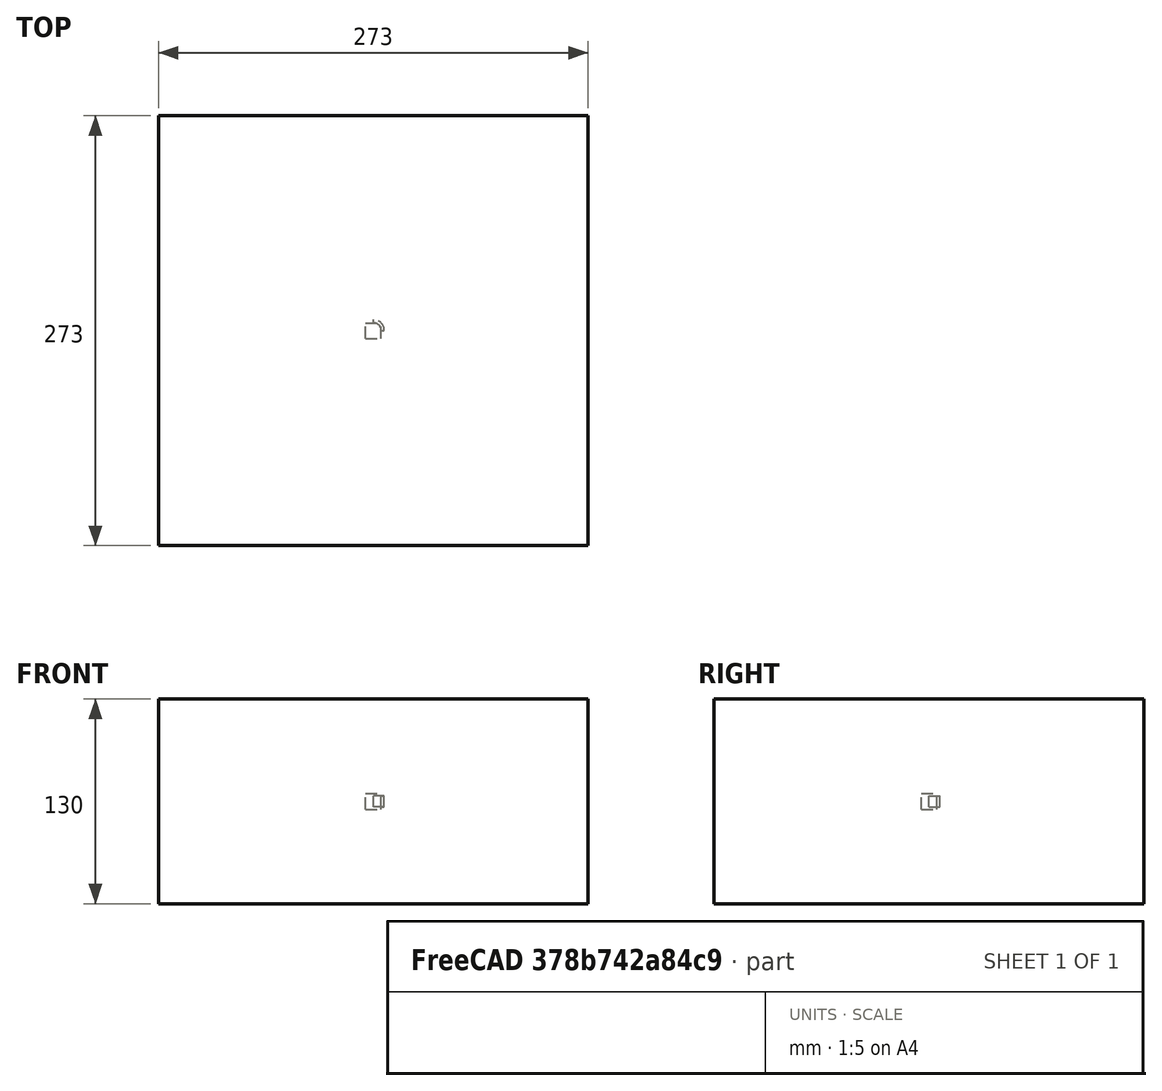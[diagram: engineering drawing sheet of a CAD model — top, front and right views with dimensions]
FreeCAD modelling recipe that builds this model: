
FCSTD DOCUMENT  (FreeCAD 0.20RUnknown)
Label: polarArray-5
License: All rights reserved
LicenseURL: http://en.wikipedia.org/wiki/All_rights_reserved
objects: App::DocumentObjectGroupPython×1251, Part::FeaturePython×4, App::Part×4
note: 3 computed .brp shape members not serialized (recipe doc carries the construction recipe); baked Part::Feature solids carry a one-line shape summary decoded from their .brp

FEATURE [App::DocumentObjectGroupPython] HALFPI  # scripted group (container) (typed FeaturePython)
  name = HALFPI
  value = pi/2.
FEATURE [App::DocumentObjectGroupPython] PI  # scripted group (container) (typed FeaturePython)
  name = PI
  value = 1.*pi
FEATURE [App::DocumentObjectGroupPython] TWOPI  # scripted group (container) (typed FeaturePython)
  name = TWOPI
  value = 2.*pi
FEATURE [App::DocumentObjectGroupPython] Constants  # scripted group (container) (typed FeaturePython)
  Group = -> [HALFPI,PI,TWOPI]
FEATURE [App::DocumentObjectGroupPython] Variables  # scripted group (container) (typed FeaturePython)
FEATURE [App::DocumentObjectGroupPython] Quantities  # scripted group (container) (typed FeaturePython)
FEATURE [App::DocumentObjectGroupPython] Isotopes  # scripted group (container) (typed FeaturePython)
FEATURE [App::DocumentObjectGroupPython] Elements  # scripted group (container) (typed FeaturePython)
FEATURE [App::DocumentObjectGroupPython] Matrix  # scripted group (container) (typed FeaturePython)
FEATURE [App::DocumentObjectGroupPython] Surfaces  # scripted group (container) (typed FeaturePython)
FEATURE [App::DocumentObjectGroupPython] Opticals  # scripted group (container) (typed FeaturePython)
  Group = -> [Matrix,Surfaces]
FEATURE [App::DocumentObjectGroupPython] G4Isotopes  # scripted group (container) (typed FeaturePython)
FEATURE [App::DocumentObjectGroupPython] H_element  # scripted group (container) (typed FeaturePython)
  Z = 1
  atom_value = 1.008
  formula = H
  name = H_element
FEATURE [App::DocumentObjectGroupPython] He_element  # scripted group (container) (typed FeaturePython)
  Z = 2
  atom_value = 4.0026
  formula = He
  name = He_element
FEATURE [App::DocumentObjectGroupPython] Li_element  # scripted group (container) (typed FeaturePython)
  Z = 3
  atom_value = 6.94
  formula = Li
  name = Li_element
FEATURE [App::DocumentObjectGroupPython] Be_element  # scripted group (container) (typed FeaturePython)
  Z = 4
  atom_value = 9.01218
  formula = Be
  name = Be_element
FEATURE [App::DocumentObjectGroupPython] B_element  # scripted group (container) (typed FeaturePython)
  Z = 5
  atom_value = 10.81
  formula = B
  name = B_element
FEATURE [App::DocumentObjectGroupPython] C_element  # scripted group (container) (typed FeaturePython)
  Z = 6
  atom_value = 12.011
  formula = C
  name = C_element
FEATURE [App::DocumentObjectGroupPython] N_element  # scripted group (container) (typed FeaturePython)
  Z = 7
  atom_value = 14.007
  formula = N
  name = N_element
FEATURE [App::DocumentObjectGroupPython] O_element  # scripted group (container) (typed FeaturePython)
  Z = 8
  atom_value = 15.999
  formula = O
  name = O_element
FEATURE [App::DocumentObjectGroupPython] F_element  # scripted group (container) (typed FeaturePython)
  Z = 9
  atom_value = 18.9984
  formula = F
  name = F_element
FEATURE [App::DocumentObjectGroupPython] Ne_element  # scripted group (container) (typed FeaturePython)
  Z = 10
  atom_value = 20.1797
  formula = Ne
  name = Ne_element
FEATURE [App::DocumentObjectGroupPython] Na_element  # scripted group (container) (typed FeaturePython)
  Z = 11
  atom_value = 22.9898
  formula = Na
  name = Na_element
FEATURE [App::DocumentObjectGroupPython] Mg_element  # scripted group (container) (typed FeaturePython)
  Z = 12
  atom_value = 24.305
  formula = Mg
  name = Mg_element
FEATURE [App::DocumentObjectGroupPython] Al_element  # scripted group (container) (typed FeaturePython)
  Z = 13
  atom_value = 26.9815
  formula = Al
  name = Al_element
FEATURE [App::DocumentObjectGroupPython] Si_element  # scripted group (container) (typed FeaturePython)
  Z = 14
  atom_value = 28.085
  formula = Si
  name = Si_element
FEATURE [App::DocumentObjectGroupPython] P_element  # scripted group (container) (typed FeaturePython)
  Z = 15
  atom_value = 30.9738
  formula = P
  name = P_element
FEATURE [App::DocumentObjectGroupPython] S_element  # scripted group (container) (typed FeaturePython)
  Z = 16
  atom_value = 32.06
  formula = S
  name = S_element
FEATURE [App::DocumentObjectGroupPython] Cl_element  # scripted group (container) (typed FeaturePython)
  Z = 17
  atom_value = 35.45
  formula = Cl
  name = Cl_element
FEATURE [App::DocumentObjectGroupPython] Ar_element  # scripted group (container) (typed FeaturePython)
  Z = 18
  atom_value = 39.95
  formula = Ar
  name = Ar_element
FEATURE [App::DocumentObjectGroupPython] K_element  # scripted group (container) (typed FeaturePython)
  Z = 19
  atom_value = 39.0983
  formula = K
  name = K_element
FEATURE [App::DocumentObjectGroupPython] Ca_element  # scripted group (container) (typed FeaturePython)
  Z = 20
  atom_value = 40.078
  formula = Ca
  name = Ca_element
FEATURE [App::DocumentObjectGroupPython] Sc_element  # scripted group (container) (typed FeaturePython)
  Z = 21
  atom_value = 44.9559
  formula = Sc
  name = Sc_element
FEATURE [App::DocumentObjectGroupPython] Ti_element  # scripted group (container) (typed FeaturePython)
  Z = 22
  atom_value = 47.867
  formula = Ti
  name = Ti_element
FEATURE [App::DocumentObjectGroupPython] V_element  # scripted group (container) (typed FeaturePython)
  Z = 23
  atom_value = 50.9415
  formula = V
  name = V_element
FEATURE [App::DocumentObjectGroupPython] Cr_element  # scripted group (container) (typed FeaturePython)
  Z = 24
  atom_value = 51.9961
  formula = Cr
  name = Cr_element
FEATURE [App::DocumentObjectGroupPython] Mn_element  # scripted group (container) (typed FeaturePython)
  Z = 25
  atom_value = 54.938
  formula = Mn
  name = Mn_element
FEATURE [App::DocumentObjectGroupPython] Fe_element  # scripted group (container) (typed FeaturePython)
  Z = 26
  atom_value = 55.845
  formula = Fe
  name = Fe_element
FEATURE [App::DocumentObjectGroupPython] Co_element  # scripted group (container) (typed FeaturePython)
  Z = 27
  atom_value = 58.9332
  formula = Co
  name = Co_element
FEATURE [App::DocumentObjectGroupPython] Ni_element  # scripted group (container) (typed FeaturePython)
  Z = 28
  atom_value = 58.6934
  formula = Ni
  name = Ni_element
FEATURE [App::DocumentObjectGroupPython] Cu_element  # scripted group (container) (typed FeaturePython)
  Z = 29
  atom_value = 63.546
  formula = Cu
  name = Cu_element
FEATURE [App::DocumentObjectGroupPython] Zn_element  # scripted group (container) (typed FeaturePython)
  Z = 30
  atom_value = 65.38
  formula = Zn
  name = Zn_element
FEATURE [App::DocumentObjectGroupPython] Ga_element  # scripted group (container) (typed FeaturePython)
  Z = 31
  atom_value = 69.723
  formula = Ga
  name = Ga_element
FEATURE [App::DocumentObjectGroupPython] Ge_element  # scripted group (container) (typed FeaturePython)
  Z = 32
  atom_value = 72.63
  formula = Ge
  name = Ge_element
FEATURE [App::DocumentObjectGroupPython] As_element  # scripted group (container) (typed FeaturePython)
  Z = 33
  atom_value = 74.9216
  formula = As
  name = As_element
FEATURE [App::DocumentObjectGroupPython] Se_element  # scripted group (container) (typed FeaturePython)
  Z = 34
  atom_value = 78.971
  formula = Se
  name = Se_element
FEATURE [App::DocumentObjectGroupPython] Br_element  # scripted group (container) (typed FeaturePython)
  Z = 35
  atom_value = 79.904
  formula = Br
  name = Br_element
FEATURE [App::DocumentObjectGroupPython] Kr_element  # scripted group (container) (typed FeaturePython)
  Z = 36
  atom_value = 83.798
  formula = Kr
  name = Kr_element
FEATURE [App::DocumentObjectGroupPython] Rb_element  # scripted group (container) (typed FeaturePython)
  Z = 37
  atom_value = 85.4678
  formula = Rb
  name = Rb_element
FEATURE [App::DocumentObjectGroupPython] Sr_element  # scripted group (container) (typed FeaturePython)
  Z = 38
  atom_value = 87.62
  formula = Sr
  name = Sr_element
FEATURE [App::DocumentObjectGroupPython] Y_element  # scripted group (container) (typed FeaturePython)
  Z = 39
  atom_value = 88.9058
  formula = Y
  name = Y_element
FEATURE [App::DocumentObjectGroupPython] Zr_element  # scripted group (container) (typed FeaturePython)
  Z = 40
  atom_value = 91.224
  formula = Zr
  name = Zr_element
FEATURE [App::DocumentObjectGroupPython] Nb_element  # scripted group (container) (typed FeaturePython)
  Z = 41
  atom_value = 92.9064
  formula = Nb
  name = Nb_element
FEATURE [App::DocumentObjectGroupPython] Mo_element  # scripted group (container) (typed FeaturePython)
  Z = 42
  atom_value = 95.95
  formula = Mo
  name = Mo_element
FEATURE [App::DocumentObjectGroupPython] Tc_element  # scripted group (container) (typed FeaturePython)
  Z = 43
  atom_value = 97
  formula = Tc
  name = Tc_element
FEATURE [App::DocumentObjectGroupPython] Ru_element  # scripted group (container) (typed FeaturePython)
  Z = 44
  atom_value = 101.07
  formula = Ru
  name = Ru_element
FEATURE [App::DocumentObjectGroupPython] Rh_element  # scripted group (container) (typed FeaturePython)
  Z = 45
  atom_value = 102.905
  formula = Rh
  name = Rh_element
FEATURE [App::DocumentObjectGroupPython] Pd_element  # scripted group (container) (typed FeaturePython)
  Z = 46
  atom_value = 106.42
  formula = Pd
  name = Pd_element
FEATURE [App::DocumentObjectGroupPython] Ag_element  # scripted group (container) (typed FeaturePython)
  Z = 47
  atom_value = 107.868
  formula = Ag
  name = Ag_element
FEATURE [App::DocumentObjectGroupPython] Cd_element  # scripted group (container) (typed FeaturePython)
  Z = 48
  atom_value = 112.414
  formula = Cd
  name = Cd_element
FEATURE [App::DocumentObjectGroupPython] In_element  # scripted group (container) (typed FeaturePython)
  Z = 49
  atom_value = 114.818
  formula = In
  name = In_element
FEATURE [App::DocumentObjectGroupPython] Sn_element  # scripted group (container) (typed FeaturePython)
  Z = 50
  atom_value = 118.71
  formula = Sn
  name = Sn_element
FEATURE [App::DocumentObjectGroupPython] Sb_element  # scripted group (container) (typed FeaturePython)
  Z = 51
  atom_value = 121.76
  formula = Sb
  name = Sb_element
FEATURE [App::DocumentObjectGroupPython] Te_element  # scripted group (container) (typed FeaturePython)
  Z = 52
  atom_value = 127.6
  formula = Te
  name = Te_element
FEATURE [App::DocumentObjectGroupPython] I_element  # scripted group (container) (typed FeaturePython)
  Z = 53
  atom_value = 126.904
  formula = I
  name = I_element
FEATURE [App::DocumentObjectGroupPython] Xe_element  # scripted group (container) (typed FeaturePython)
  Z = 54
  atom_value = 131.293
  formula = Xe
  name = Xe_element
FEATURE [App::DocumentObjectGroupPython] Cs_element  # scripted group (container) (typed FeaturePython)
  Z = 55
  atom_value = 132.905
  formula = Cs
  name = Cs_element
FEATURE [App::DocumentObjectGroupPython] Ba_element  # scripted group (container) (typed FeaturePython)
  Z = 56
  atom_value = 137.327
  formula = Ba
  name = Ba_element
FEATURE [App::DocumentObjectGroupPython] La_element  # scripted group (container) (typed FeaturePython)
  Z = 57
  atom_value = 138.905
  formula = La
  name = La_element
FEATURE [App::DocumentObjectGroupPython] Ce_element  # scripted group (container) (typed FeaturePython)
  Z = 58
  atom_value = 140.116
  formula = Ce
  name = Ce_element
FEATURE [App::DocumentObjectGroupPython] Pr_element  # scripted group (container) (typed FeaturePython)
  Z = 59
  atom_value = 140.908
  formula = Pr
  name = Pr_element
FEATURE [App::DocumentObjectGroupPython] Nd_element  # scripted group (container) (typed FeaturePython)
  Z = 60
  atom_value = 144.242
  formula = Nd
  name = Nd_element
FEATURE [App::DocumentObjectGroupPython] Pm_element  # scripted group (container) (typed FeaturePython)
  Z = 61
  atom_value = 145
  formula = Pm
  name = Pm_element
FEATURE [App::DocumentObjectGroupPython] Sm_element  # scripted group (container) (typed FeaturePython)
  Z = 62
  atom_value = 150.36
  formula = Sm
  name = Sm_element
FEATURE [App::DocumentObjectGroupPython] Eu_element  # scripted group (container) (typed FeaturePython)
  Z = 63
  atom_value = 151.964
  formula = Eu
  name = Eu_element
FEATURE [App::DocumentObjectGroupPython] Gd_element  # scripted group (container) (typed FeaturePython)
  Z = 64
  atom_value = 157.25
  formula = Gd
  name = Gd_element
FEATURE [App::DocumentObjectGroupPython] Tb_element  # scripted group (container) (typed FeaturePython)
  Z = 65
  atom_value = 158.925
  formula = Tb
  name = Tb_element
FEATURE [App::DocumentObjectGroupPython] Dy_element  # scripted group (container) (typed FeaturePython)
  Z = 66
  atom_value = 162.5
  formula = Dy
  name = Dy_element
FEATURE [App::DocumentObjectGroupPython] Ho_element  # scripted group (container) (typed FeaturePython)
  Z = 67
  atom_value = 164.93
  formula = Ho
  name = Ho_element
FEATURE [App::DocumentObjectGroupPython] Er_element  # scripted group (container) (typed FeaturePython)
  Z = 68
  atom_value = 167.259
  formula = Er
  name = Er_element
FEATURE [App::DocumentObjectGroupPython] Tm_element  # scripted group (container) (typed FeaturePython)
  Z = 69
  atom_value = 168.934
  formula = Tm
  name = Tm_element
FEATURE [App::DocumentObjectGroupPython] Yb_element  # scripted group (container) (typed FeaturePython)
  Z = 70
  atom_value = 173.045
  formula = Yb
  name = Yb_element
FEATURE [App::DocumentObjectGroupPython] Lu_element  # scripted group (container) (typed FeaturePython)
  Z = 71
  atom_value = 174.967
  formula = Lu
  name = Lu_element
FEATURE [App::DocumentObjectGroupPython] Hf_element  # scripted group (container) (typed FeaturePython)
  Z = 72
  atom_value = 178.49
  formula = Hf
  name = Hf_element
FEATURE [App::DocumentObjectGroupPython] Ta_element  # scripted group (container) (typed FeaturePython)
  Z = 73
  atom_value = 180.948
  formula = Ta
  name = Ta_element
FEATURE [App::DocumentObjectGroupPython] W_element  # scripted group (container) (typed FeaturePython)
  Z = 74
  atom_value = 183.84
  formula = W
  name = W_element
FEATURE [App::DocumentObjectGroupPython] Re_element  # scripted group (container) (typed FeaturePython)
  Z = 75
  atom_value = 186.207
  formula = Re
  name = Re_element
FEATURE [App::DocumentObjectGroupPython] Os_element  # scripted group (container) (typed FeaturePython)
  Z = 76
  atom_value = 190.23
  formula = Os
  name = Os_element
FEATURE [App::DocumentObjectGroupPython] Ir_element  # scripted group (container) (typed FeaturePython)
  Z = 77
  atom_value = 192.217
  formula = Ir
  name = Ir_element
FEATURE [App::DocumentObjectGroupPython] Pt_element  # scripted group (container) (typed FeaturePython)
  Z = 78
  atom_value = 195.084
  formula = Pt
  name = Pt_element
FEATURE [App::DocumentObjectGroupPython] Au_element  # scripted group (container) (typed FeaturePython)
  Z = 79
  atom_value = 196.967
  formula = Au
  name = Au_element
FEATURE [App::DocumentObjectGroupPython] Hg_element  # scripted group (container) (typed FeaturePython)
  Z = 80
  atom_value = 200.592
  formula = Hg
  name = Hg_element
FEATURE [App::DocumentObjectGroupPython] Tl_element  # scripted group (container) (typed FeaturePython)
  Z = 81
  atom_value = 204.38
  formula = Tl
  name = Tl_element
FEATURE [App::DocumentObjectGroupPython] Pb_element  # scripted group (container) (typed FeaturePython)
  Z = 82
  atom_value = 207.2
  formula = Pb
  name = Pb_element
FEATURE [App::DocumentObjectGroupPython] Bi_element  # scripted group (container) (typed FeaturePython)
  Z = 83
  atom_value = 208.98
  formula = Bi
  name = Bi_element
FEATURE [App::DocumentObjectGroupPython] Po_element  # scripted group (container) (typed FeaturePython)
  Z = 84
  atom_value = 209
  formula = Po
  name = Po_element
FEATURE [App::DocumentObjectGroupPython] At_element  # scripted group (container) (typed FeaturePython)
  Z = 85
  atom_value = 210
  formula = At
  name = At_element
FEATURE [App::DocumentObjectGroupPython] Rn_element  # scripted group (container) (typed FeaturePython)
  Z = 86
  atom_value = 222
  formula = Rn
  name = Rn_element
FEATURE [App::DocumentObjectGroupPython] Fr_element  # scripted group (container) (typed FeaturePython)
  Z = 87
  atom_value = 223
  formula = Fr
  name = Fr_element
FEATURE [App::DocumentObjectGroupPython] Ra_element  # scripted group (container) (typed FeaturePython)
  Z = 88
  atom_value = 226
  formula = Ra
  name = Ra_element
FEATURE [App::DocumentObjectGroupPython] Ac_element  # scripted group (container) (typed FeaturePython)
  Z = 89
  atom_value = 227
  formula = Ac
  name = Ac_element
FEATURE [App::DocumentObjectGroupPython] Th_element  # scripted group (container) (typed FeaturePython)
  Z = 90
  atom_value = 232.038
  formula = Th
  name = Th_element
FEATURE [App::DocumentObjectGroupPython] Pa_element  # scripted group (container) (typed FeaturePython)
  Z = 91
  atom_value = 231.036
  formula = Pa
  name = Pa_element
FEATURE [App::DocumentObjectGroupPython] U_element  # scripted group (container) (typed FeaturePython)
  Z = 92
  atom_value = 238.029
  formula = U
  name = U_element
FEATURE [App::DocumentObjectGroupPython] Np_element  # scripted group (container) (typed FeaturePython)
  Z = 93
  atom_value = 237
  formula = Np
  name = Np_element
FEATURE [App::DocumentObjectGroupPython] Pu_element  # scripted group (container) (typed FeaturePython)
  Z = 94
  atom_value = 244
  formula = Pu
  name = Pu_element
FEATURE [App::DocumentObjectGroupPython] Am_element  # scripted group (container) (typed FeaturePython)
  Z = 95
  atom_value = 243
  formula = Am
  name = Am_element
FEATURE [App::DocumentObjectGroupPython] Cm_element  # scripted group (container) (typed FeaturePython)
  Z = 96
  atom_value = 247
  formula = Cm
  name = Cm_element
FEATURE [App::DocumentObjectGroupPython] Bk_element  # scripted group (container) (typed FeaturePython)
  Z = 97
  atom_value = 247
  formula = Bk
  name = Bk_element
FEATURE [App::DocumentObjectGroupPython] Cf_element  # scripted group (container) (typed FeaturePython)
  Z = 98
  atom_value = 251
  formula = Cf
  name = Cf_element
FEATURE [App::DocumentObjectGroupPython] G4Elements  # scripted group (container) (typed FeaturePython)
  Group = -> [H_element,He_element,Li_element,Be_element,B_element,C_element,N_element,O_element,F_element,Ne_element,Na_element,Mg_element,Al_element,Si_element,P_element,S_element,Cl_element,Ar_element,K_element,Ca_element,Sc_element,Ti_element,V_element,Cr_element,Mn_element,Fe_element,Co_element,Ni_element,Cu_element,Zn_element,Ga_element,Ge_element,As_element,Se_element,Br_element,Kr_element,Rb_element,+61 more]
FEATURE [App::DocumentObjectGroupPython] H_element001  label="H_element : 0.101"  # scripted group (container) (typed FeaturePython)
  n = 0.101327
FEATURE [App::DocumentObjectGroupPython] C_element001  label="C_element : 0.775"  # scripted group (container) (typed FeaturePython)
  n = 0.7755
FEATURE [App::DocumentObjectGroupPython] N_element001  label="N_element : 0.035"  # scripted group (container) (typed FeaturePython)
  n = 0.035057
FEATURE [App::DocumentObjectGroupPython] O_element001  label="O_element : 0.052"  # scripted group (container) (typed FeaturePython)
  n = 0.0523159
FEATURE [App::DocumentObjectGroupPython] F_element001  label="F_element : 0.017"  # scripted group (container) (typed FeaturePython)
  n = 0.017422
FEATURE [App::DocumentObjectGroupPython] Ca_element001  label="Ca_element : 0.018"  # scripted group (container) (typed FeaturePython)
  n = 0.018378
FEATURE [App::DocumentObjectGroupPython] G4_A_150_TISSUE  label="G4_A-150_TISSUE"  # scripted group (container) (typed FeaturePython)
  Dunit = g/cm3
  Dvalue = 1.127
  Group = -> [H_element001,C_element001,N_element001,O_element001,F_element001,Ca_element001]
  conduct = 2
  density = 1
  expand = 3
  formula = G4_A-150_TISSUE
  name = G4_A-150_TISSUE
  specific = 4
FEATURE [App::DocumentObjectGroupPython] C_element002  label="C_element : 3"  # scripted group (container) (typed FeaturePython)
  n = 3
  ref = C_element
FEATURE [App::DocumentObjectGroupPython] H_element002  label="H_element : 6"  # scripted group (container) (typed FeaturePython)
  n = 6
  ref = H_element
FEATURE [App::DocumentObjectGroupPython] O_element002  label="O_element : 1"  # scripted group (container) (typed FeaturePython)
  n = 1
  ref = O_element
FEATURE [App::DocumentObjectGroupPython] G4_ACETONE  # scripted group (container) (typed FeaturePython)
  Dunit = g/cm3
  Dvalue = 0.7899
  Group = -> [C_element002,H_element002,O_element002]
  conduct = 2
  density = 1
  expand = 3
  formula = G4_ACETONE
  name = G4_ACETONE
  specific = 4
FEATURE [App::DocumentObjectGroupPython] C_element003  label="C_element : 2"  # scripted group (container) (typed FeaturePython)
  n = 2
  ref = C_element
FEATURE [App::DocumentObjectGroupPython] H_element003  label="H_element : 2"  # scripted group (container) (typed FeaturePython)
  n = 2
  ref = H_element
FEATURE [App::DocumentObjectGroupPython] G4_ACETYLENE  # scripted group (container) (typed FeaturePython)
  Dunit = g/cm3
  Dvalue = 0.0010967
  Group = -> [C_element003,H_element003]
  conduct = 2
  density = 1
  expand = 3
  formula = G4_ACETYLENE
  name = G4_ACETYLENE
  specific = 4
FEATURE [App::DocumentObjectGroupPython] C_element004  label="C_element : 5"  # scripted group (container) (typed FeaturePython)
  n = 5
  ref = C_element
FEATURE [App::DocumentObjectGroupPython] H_element004  label="H_element : 5"  # scripted group (container) (typed FeaturePython)
  n = 5
  ref = H_element
FEATURE [App::DocumentObjectGroupPython] N_element002  label="N_element : 5"  # scripted group (container) (typed FeaturePython)
  n = 5
  ref = N_element
FEATURE [App::DocumentObjectGroupPython] G4_ADENINE  # scripted group (container) (typed FeaturePython)
  Dunit = g/cm3
  Dvalue = 1.6
  Group = -> [C_element004,H_element004,N_element002]
  conduct = 2
  density = 1
  expand = 3
  formula = G4_ADENINE
  name = G4_ADENINE
  specific = 4
FEATURE [App::DocumentObjectGroupPython] H_element005  label="H_element : 0.114"  # scripted group (container) (typed FeaturePython)
  n = 0.114
FEATURE [App::DocumentObjectGroupPython] C_element005  label="C_element : 0.598"  # scripted group (container) (typed FeaturePython)
  n = 0.598
FEATURE [App::DocumentObjectGroupPython] N_element003  label="N_element : 0.007"  # scripted group (container) (typed FeaturePython)
  n = 0.007
FEATURE [App::DocumentObjectGroupPython] O_element003  label="O_element : 0.278"  # scripted group (container) (typed FeaturePython)
  n = 0.278
FEATURE [App::DocumentObjectGroupPython] Na_element001  label="Na_element : 0.001"  # scripted group (container) (typed FeaturePython)
  n = 0.001
FEATURE [App::DocumentObjectGroupPython] S_element001  label="S_element : 0.001"  # scripted group (container) (typed FeaturePython)
  n = 0.001
FEATURE [App::DocumentObjectGroupPython] Cl_element001  label="Cl_element : 0.001"  # scripted group (container) (typed FeaturePython)
  n = 0.001
FEATURE [App::DocumentObjectGroupPython] G4_ADIPOSE_TISSUE_ICRP  # scripted group (container) (typed FeaturePython)
  Dunit = g/cm3
  Dvalue = 0.95
  Group = -> [H_element005,C_element005,N_element003,O_element003,Na_element001,S_element001,Cl_element001]
  conduct = 2
  density = 1
  expand = 3
  formula = G4_ADIPOSE_TISSUE_ICRP
  name = G4_ADIPOSE_TISSUE_ICRP
  specific = 4
FEATURE [App::DocumentObjectGroupPython] C_element006  label="C_element : 0.000"  # scripted group (container) (typed FeaturePython)
  n = 0.000124
FEATURE [App::DocumentObjectGroupPython] N_element004  label="N_element : 0.755"  # scripted group (container) (typed FeaturePython)
  n = 0.755268
FEATURE [App::DocumentObjectGroupPython] O_element004  label="O_element : 0.232"  # scripted group (container) (typed FeaturePython)
  n = 0.231781
FEATURE [App::DocumentObjectGroupPython] Ar_element001  label="Ar_element : 0.013"  # scripted group (container) (typed FeaturePython)
  n = 0.012827
FEATURE [App::DocumentObjectGroupPython] G4_AIR  # scripted group (container) (typed FeaturePython)
  Dunit = g/cm3
  Dvalue = 0.00120479
  Group = -> [C_element006,N_element004,O_element004,Ar_element001]
  conduct = 2
  density = 1
  expand = 3
  formula = G4_AIR
  name = G4_AIR
  specific = 4
FEATURE [App::DocumentObjectGroupPython] C_element007  label="C_element : 006"  # scripted group (container) (typed FeaturePython)
  n = 3
  ref = C_element
FEATURE [App::DocumentObjectGroupPython] H_element006  label="H_element : 7"  # scripted group (container) (typed FeaturePython)
  n = 7
  ref = H_element
FEATURE [App::DocumentObjectGroupPython] N_element005  label="N_element : 1"  # scripted group (container) (typed FeaturePython)
  n = 1
  ref = N_element
FEATURE [App::DocumentObjectGroupPython] O_element005  label="O_element : 2"  # scripted group (container) (typed FeaturePython)
  n = 2
  ref = O_element
FEATURE [App::DocumentObjectGroupPython] G4_ALANINE  # scripted group (container) (typed FeaturePython)
  Dunit = g/cm3
  Dvalue = 1.42
  Group = -> [C_element007,H_element006,N_element005,O_element005]
  conduct = 2
  density = 1
  expand = 3
  formula = G4_ALANINE
  name = G4_ALANINE
  specific = 4
FEATURE [App::DocumentObjectGroupPython] Al_element001  label="Al_element : 2"  # scripted group (container) (typed FeaturePython)
  n = 2
  ref = Al_element
FEATURE [App::DocumentObjectGroupPython] O_element006  label="O_element : 3"  # scripted group (container) (typed FeaturePython)
  n = 3
  ref = O_element
FEATURE [App::DocumentObjectGroupPython] G4_ALUMINUM_OXIDE  # scripted group (container) (typed FeaturePython)
  Dunit = g/cm3
  Dvalue = 3.97
  Group = -> [Al_element001,O_element006]
  conduct = 2
  density = 1
  expand = 3
  formula = G4_ALUMINUM_OXIDE
  name = G4_ALUMINUM_OXIDE
  specific = 4
FEATURE [App::DocumentObjectGroupPython] H_element007  label="H_element : 0.106"  # scripted group (container) (typed FeaturePython)
  n = 0.10593
FEATURE [App::DocumentObjectGroupPython] C_element008  label="C_element : 0.789"  # scripted group (container) (typed FeaturePython)
  n = 0.788974
FEATURE [App::DocumentObjectGroupPython] O_element007  label="O_element : 0.105"  # scripted group (container) (typed FeaturePython)
  n = 0.105096
FEATURE [App::DocumentObjectGroupPython] G4_AMBER  # scripted group (container) (typed FeaturePython)
  Dunit = g/cm3
  Dvalue = 1.1
  Group = -> [H_element007,C_element008,O_element007]
  conduct = 2
  density = 1
  expand = 3
  formula = G4_AMBER
  name = G4_AMBER
  specific = 4
FEATURE [App::DocumentObjectGroupPython] N_element006  label="N_element : 006"  # scripted group (container) (typed FeaturePython)
  n = 1
  ref = N_element
FEATURE [App::DocumentObjectGroupPython] H_element008  label="H_element : 3"  # scripted group (container) (typed FeaturePython)
  n = 3
  ref = H_element
FEATURE [App::DocumentObjectGroupPython] G4_AMMONIA  # scripted group (container) (typed FeaturePython)
  Dunit = g/cm3
  Dvalue = 0.000826019
  Group = -> [N_element006,H_element008]
  conduct = 2
  density = 1
  expand = 3
  formula = G4_AMMONIA
  name = G4_AMMONIA
  specific = 4
FEATURE [App::DocumentObjectGroupPython] C_element009  label="C_element : 6"  # scripted group (container) (typed FeaturePython)
  n = 6
  ref = C_element
FEATURE [App::DocumentObjectGroupPython] H_element009  label="H_element : 008"  # scripted group (container) (typed FeaturePython)
  n = 7
  ref = H_element
FEATURE [App::DocumentObjectGroupPython] N_element007  label="N_element : 007"  # scripted group (container) (typed FeaturePython)
  n = 1
  ref = N_element
FEATURE [App::DocumentObjectGroupPython] G4_ANILINE  # scripted group (container) (typed FeaturePython)
  Dunit = g/cm3
  Dvalue = 1.0235
  Group = -> [C_element009,H_element009,N_element007]
  conduct = 2
  density = 1
  expand = 3
  formula = G4_ANILINE
  name = G4_ANILINE
  specific = 4
FEATURE [App::DocumentObjectGroupPython] C_element010  label="C_element : 14"  # scripted group (container) (typed FeaturePython)
  n = 14
  ref = C_element
FEATURE [App::DocumentObjectGroupPython] H_element010  label="H_element : 10"  # scripted group (container) (typed FeaturePython)
  n = 10
  ref = H_element
FEATURE [App::DocumentObjectGroupPython] G4_ANTHRACENE  # scripted group (container) (typed FeaturePython)
  Dunit = g/cm3
  Dvalue = 1.283
  Group = -> [C_element010,H_element010]
  conduct = 2
  density = 1
  expand = 3
  formula = G4_ANTHRACENE
  name = G4_ANTHRACENE
  specific = 4
FEATURE [App::DocumentObjectGroupPython] H_element011  label="H_element : 0.065"  # scripted group (container) (typed FeaturePython)
  n = 0.0654709
FEATURE [App::DocumentObjectGroupPython] C_element011  label="C_element : 0.537"  # scripted group (container) (typed FeaturePython)
  n = 0.536944
FEATURE [App::DocumentObjectGroupPython] N_element008  label="N_element : 0.021"  # scripted group (container) (typed FeaturePython)
  n = 0.0215
FEATURE [App::DocumentObjectGroupPython] O_element008  label="O_element : 0.032"  # scripted group (container) (typed FeaturePython)
  n = 0.032085
FEATURE [App::DocumentObjectGroupPython] F_element002  label="F_element : 0.167"  # scripted group (container) (typed FeaturePython)
  n = 0.167411
FEATURE [App::DocumentObjectGroupPython] Ca_element002  label="Ca_element : 0.177"  # scripted group (container) (typed FeaturePython)
  n = 0.176589
FEATURE [App::DocumentObjectGroupPython] G4_B_100_BONE  label="G4_B-100_BONE"  # scripted group (container) (typed FeaturePython)
  Dunit = g/cm3
  Dvalue = 1.45
  Group = -> [H_element011,C_element011,N_element008,O_element008,F_element002,Ca_element002]
  conduct = 2
  density = 1
  expand = 3
  formula = G4_B-100_BONE
  name = G4_B-100_BONE
  specific = 4
FEATURE [App::DocumentObjectGroupPython] H_element012  label="H_element : 0.057"  # scripted group (container) (typed FeaturePython)
  n = 0.057441
FEATURE [App::DocumentObjectGroupPython] C_element012  label="C_element : 0.790"  # scripted group (container) (typed FeaturePython)
  n = 0.774591
FEATURE [App::DocumentObjectGroupPython] O_element009  label="O_element : 0.168"  # scripted group (container) (typed FeaturePython)
  n = 0.167968
FEATURE [App::DocumentObjectGroupPython] G4_BAKELITE  # scripted group (container) (typed FeaturePython)
  Dunit = g/cm3
  Dvalue = 1.25
  Group = -> [H_element012,C_element012,O_element009]
  conduct = 2
  density = 1
  expand = 3
  formula = G4_BAKELITE
  name = G4_BAKELITE
  specific = 4
FEATURE [App::DocumentObjectGroupPython] Ba_element001  label="Ba_element : 1"  # scripted group (container) (typed FeaturePython)
  n = 1
  ref = Ba_element
FEATURE [App::DocumentObjectGroupPython] F_element003  label="F_element : 2"  # scripted group (container) (typed FeaturePython)
  n = 2
  ref = F_element
FEATURE [App::DocumentObjectGroupPython] G4_BARIUM_FLUORIDE  # scripted group (container) (typed FeaturePython)
  Dunit = g/cm3
  Dvalue = 4.89
  Group = -> [Ba_element001,F_element003]
  conduct = 2
  density = 1
  expand = 3
  formula = G4_BARIUM_FLUORIDE
  name = G4_BARIUM_FLUORIDE
  specific = 4
FEATURE [App::DocumentObjectGroupPython] Ba_element002  label="Ba_element : 002"  # scripted group (container) (typed FeaturePython)
  n = 1
  ref = Ba_element
FEATURE [App::DocumentObjectGroupPython] S_element002  label="S_element : 1"  # scripted group (container) (typed FeaturePython)
  n = 1
  ref = S_element
FEATURE [App::DocumentObjectGroupPython] O_element010  label="O_element : 4"  # scripted group (container) (typed FeaturePython)
  n = 4
  ref = O_element
FEATURE [App::DocumentObjectGroupPython] G4_BARIUM_SULFATE  # scripted group (container) (typed FeaturePython)
  Dunit = g/cm3
  Dvalue = 4.5
  Group = -> [Ba_element002,S_element002,O_element010]
  conduct = 2
  density = 1
  expand = 3
  formula = G4_BARIUM_SULFATE
  name = G4_BARIUM_SULFATE
  specific = 4
FEATURE [App::DocumentObjectGroupPython] C_element013  label="C_element : 007"  # scripted group (container) (typed FeaturePython)
  n = 6
  ref = C_element
FEATURE [App::DocumentObjectGroupPython] H_element013  label="H_element : 009"  # scripted group (container) (typed FeaturePython)
  n = 6
  ref = H_element
FEATURE [App::DocumentObjectGroupPython] G4_BENZENE  # scripted group (container) (typed FeaturePython)
  Dunit = g/cm3
  Dvalue = 0.87865
  Group = -> [C_element013,H_element013]
  conduct = 2
  density = 1
  expand = 3
  formula = G4_BENZENE
  name = G4_BENZENE
  specific = 4
FEATURE [App::DocumentObjectGroupPython] Be_element001  label="Be_element : 1"  # scripted group (container) (typed FeaturePython)
  n = 1
  ref = Be_element
FEATURE [App::DocumentObjectGroupPython] O_element011  label="O_element : 005"  # scripted group (container) (typed FeaturePython)
  n = 1
  ref = O_element
FEATURE [App::DocumentObjectGroupPython] G4_BERYLLIUM_OXIDE  # scripted group (container) (typed FeaturePython)
  Dunit = g/cm3
  Dvalue = 3.01
  Group = -> [Be_element001,O_element011]
  conduct = 2
  density = 1
  expand = 3
  formula = G4_BERYLLIUM_OXIDE
  name = G4_BERYLLIUM_OXIDE
  specific = 4
FEATURE [App::DocumentObjectGroupPython] Bi_element001  label="Bi_element : 4"  # scripted group (container) (typed FeaturePython)
  n = 4
  ref = Bi_element
FEATURE [App::DocumentObjectGroupPython] Ge_element001  label="Ge_element : 3"  # scripted group (container) (typed FeaturePython)
  n = 3
  ref = Ge_element
FEATURE [App::DocumentObjectGroupPython] O_element012  label="O_element : 12"  # scripted group (container) (typed FeaturePython)
  n = 12
  ref = O_element
FEATURE [App::DocumentObjectGroupPython] G4_BGO  # scripted group (container) (typed FeaturePython)
  Dunit = g/cm3
  Dvalue = 7.13
  Group = -> [Bi_element001,Ge_element001,O_element012]
  conduct = 2
  density = 1
  expand = 3
  formula = G4_BGO
  name = G4_BGO
  specific = 4
FEATURE [App::DocumentObjectGroupPython] H_element014  label="H_element : 0.102"  # scripted group (container) (typed FeaturePython)
  n = 0.102
FEATURE [App::DocumentObjectGroupPython] C_element014  label="C_element : 0.110"  # scripted group (container) (typed FeaturePython)
  n = 0.11
FEATURE [App::DocumentObjectGroupPython] N_element009  label="N_element : 0.033"  # scripted group (container) (typed FeaturePython)
  n = 0.033
FEATURE [App::DocumentObjectGroupPython] O_element013  label="O_element : 0.745"  # scripted group (container) (typed FeaturePython)
  n = 0.745
FEATURE [App::DocumentObjectGroupPython] Na_element002  label="Na_element : 0.002"  # scripted group (container) (typed FeaturePython)
  n = 0.001
FEATURE [App::DocumentObjectGroupPython] P_element001  label="P_element : 0.001"  # scripted group (container) (typed FeaturePython)
  n = 0.001
FEATURE [App::DocumentObjectGroupPython] S_element003  label="S_element : 0.002"  # scripted group (container) (typed FeaturePython)
  n = 0.002
FEATURE [App::DocumentObjectGroupPython] Cl_element002  label="Cl_element : 0.003"  # scripted group (container) (typed FeaturePython)
  n = 0.003
FEATURE [App::DocumentObjectGroupPython] K_element001  label="K_element : 0.002"  # scripted group (container) (typed FeaturePython)
  n = 0.002
FEATURE [App::DocumentObjectGroupPython] Fe_element001  label="Fe_element : 0.001"  # scripted group (container) (typed FeaturePython)
  n = 0.001
FEATURE [App::DocumentObjectGroupPython] G4_BLOOD_ICRP  # scripted group (container) (typed FeaturePython)
  Dunit = g/cm3
  Dvalue = 1.06
  Group = -> [H_element014,C_element014,N_element009,O_element013,Na_element002,P_element001,S_element003,Cl_element002,K_element001,Fe_element001]
  conduct = 2
  density = 1
  expand = 3
  formula = G4_BLOOD_ICRP
  name = G4_BLOOD_ICRP
  specific = 4
FEATURE [App::DocumentObjectGroupPython] H_element015  label="H_element : 0.064"  # scripted group (container) (typed FeaturePython)
  n = 0.064
FEATURE [App::DocumentObjectGroupPython] C_element015  label="C_element : 0.278"  # scripted group (container) (typed FeaturePython)
  n = 0.278
FEATURE [App::DocumentObjectGroupPython] N_element010  label="N_element : 0.027"  # scripted group (container) (typed FeaturePython)
  n = 0.027
FEATURE [App::DocumentObjectGroupPython] O_element014  label="O_element : 0.410"  # scripted group (container) (typed FeaturePython)
  n = 0.41
FEATURE [App::DocumentObjectGroupPython] Mg_element001  label="Mg_element : 0.002"  # scripted group (container) (typed FeaturePython)
  n = 0.002
FEATURE [App::DocumentObjectGroupPython] P_element002  label="P_element : 0.070"  # scripted group (container) (typed FeaturePython)
  n = 0.07
FEATURE [App::DocumentObjectGroupPython] S_element004  label="S_element : 0.003"  # scripted group (container) (typed FeaturePython)
  n = 0.002
FEATURE [App::DocumentObjectGroupPython] Ca_element003  label="Ca_element : 0.147"  # scripted group (container) (typed FeaturePython)
  n = 0.147
FEATURE [App::DocumentObjectGroupPython] G4_BONE_COMPACT_ICRU  # scripted group (container) (typed FeaturePython)
  Dunit = g/cm3
  Dvalue = 1.85
  Group = -> [H_element015,C_element015,N_element010,O_element014,Mg_element001,P_element002,S_element004,Ca_element003]
  conduct = 2
  density = 1
  expand = 3
  formula = G4_BONE_COMPACT_ICRU
  name = G4_BONE_COMPACT_ICRU
  specific = 4
FEATURE [App::DocumentObjectGroupPython] H_element016  label="H_element : 0.034"  # scripted group (container) (typed FeaturePython)
  n = 0.034
FEATURE [App::DocumentObjectGroupPython] C_element016  label="C_element : 0.155"  # scripted group (container) (typed FeaturePython)
  n = 0.155
FEATURE [App::DocumentObjectGroupPython] N_element011  label="N_element : 0.042"  # scripted group (container) (typed FeaturePython)
  n = 0.042
FEATURE [App::DocumentObjectGroupPython] O_element015  label="O_element : 0.435"  # scripted group (container) (typed FeaturePython)
  n = 0.435
FEATURE [App::DocumentObjectGroupPython] Na_element003  label="Na_element : 0.003"  # scripted group (container) (typed FeaturePython)
  n = 0.001
FEATURE [App::DocumentObjectGroupPython] Mg_element002  label="Mg_element : 0.003"  # scripted group (container) (typed FeaturePython)
  n = 0.002
FEATURE [App::DocumentObjectGroupPython] P_element003  label="P_element : 0.103"  # scripted group (container) (typed FeaturePython)
  n = 0.103
FEATURE [App::DocumentObjectGroupPython] S_element005  label="S_element : 0.004"  # scripted group (container) (typed FeaturePython)
  n = 0.003
FEATURE [App::DocumentObjectGroupPython] Ca_element004  label="Ca_element : 0.225"  # scripted group (container) (typed FeaturePython)
  n = 0.225
FEATURE [App::DocumentObjectGroupPython] G4_BONE_CORTICAL_ICRP  # scripted group (container) (typed FeaturePython)
  Dunit = g/cm3
  Dvalue = 1.92
  Group = -> [H_element016,C_element016,N_element011,O_element015,Na_element003,Mg_element002,P_element003,S_element005,Ca_element004]
  conduct = 2
  density = 1
  expand = 3
  formula = G4_BONE_CORTICAL_ICRP
  name = G4_BONE_CORTICAL_ICRP
  specific = 4
FEATURE [App::DocumentObjectGroupPython] B_element001  label="B_element : 4"  # scripted group (container) (typed FeaturePython)
  n = 4
  ref = B_element
FEATURE [App::DocumentObjectGroupPython] C_element017  label="C_element : 1"  # scripted group (container) (typed FeaturePython)
  n = 1
  ref = C_element
FEATURE [App::DocumentObjectGroupPython] G4_BORON_CARBIDE  # scripted group (container) (typed FeaturePython)
  Dunit = g/cm3
  Dvalue = 2.52
  Group = -> [B_element001,C_element017]
  conduct = 2
  density = 1
  expand = 3
  formula = G4_BORON_CARBIDE
  name = G4_BORON_CARBIDE
  specific = 4
FEATURE [App::DocumentObjectGroupPython] B_element002  label="B_element : 2"  # scripted group (container) (typed FeaturePython)
  n = 2
  ref = B_element
FEATURE [App::DocumentObjectGroupPython] O_element016  label="O_element : 006"  # scripted group (container) (typed FeaturePython)
  n = 3
  ref = O_element
FEATURE [App::DocumentObjectGroupPython] G4_BORON_OXIDE  # scripted group (container) (typed FeaturePython)
  Dunit = g/cm3
  Dvalue = 1.812
  Group = -> [B_element002,O_element016]
  conduct = 2
  density = 1
  expand = 3
  formula = G4_BORON_OXIDE
  name = G4_BORON_OXIDE
  specific = 4
FEATURE [App::DocumentObjectGroupPython] H_element017  label="H_element : 0.107"  # scripted group (container) (typed FeaturePython)
  n = 0.107
FEATURE [App::DocumentObjectGroupPython] C_element018  label="C_element : 0.145"  # scripted group (container) (typed FeaturePython)
  n = 0.145
FEATURE [App::DocumentObjectGroupPython] N_element012  label="N_element : 0.022"  # scripted group (container) (typed FeaturePython)
  n = 0.022
FEATURE [App::DocumentObjectGroupPython] O_element017  label="O_element : 0.712"  # scripted group (container) (typed FeaturePython)
  n = 0.712
FEATURE [App::DocumentObjectGroupPython] Na_element004  label="Na_element : 0.004"  # scripted group (container) (typed FeaturePython)
  n = 0.002
FEATURE [App::DocumentObjectGroupPython] P_element004  label="P_element : 0.004"  # scripted group (container) (typed FeaturePython)
  n = 0.004
FEATURE [App::DocumentObjectGroupPython] S_element006  label="S_element : 0.005"  # scripted group (container) (typed FeaturePython)
  n = 0.002
FEATURE [App::DocumentObjectGroupPython] Cl_element003  label="Cl_element : 0.004"  # scripted group (container) (typed FeaturePython)
  n = 0.003
FEATURE [App::DocumentObjectGroupPython] K_element002  label="K_element : 0.003"  # scripted group (container) (typed FeaturePython)
  n = 0.003
FEATURE [App::DocumentObjectGroupPython] G4_BRAIN_ICRP  # scripted group (container) (typed FeaturePython)
  Dunit = g/cm3
  Dvalue = 1.04
  Group = -> [H_element017,C_element018,N_element012,O_element017,Na_element004,P_element004,S_element006,Cl_element003,K_element002]
  conduct = 2
  density = 1
  expand = 3
  formula = G4_BRAIN_ICRP
  name = G4_BRAIN_ICRP
  specific = 4
FEATURE [App::DocumentObjectGroupPython] C_element019  label="C_element : 4"  # scripted group (container) (typed FeaturePython)
  n = 4
  ref = C_element
FEATURE [App::DocumentObjectGroupPython] H_element018  label="H_element : 010"  # scripted group (container) (typed FeaturePython)
  n = 10
  ref = H_element
FEATURE [App::DocumentObjectGroupPython] G4_BUTANE  # scripted group (container) (typed FeaturePython)
  Dunit = g/cm3
  Dvalue = 0.00249343
  Group = -> [C_element019,H_element018]
  conduct = 2
  density = 1
  expand = 3
  formula = G4_BUTANE
  name = G4_BUTANE
  specific = 4
FEATURE [App::DocumentObjectGroupPython] C_element020  label="C_element : 008"  # scripted group (container) (typed FeaturePython)
  n = 4
  ref = C_element
FEATURE [App::DocumentObjectGroupPython] H_element019  label="H_element : 011"  # scripted group (container) (typed FeaturePython)
  n = 10
  ref = H_element
FEATURE [App::DocumentObjectGroupPython] O_element018  label="O_element : 007"  # scripted group (container) (typed FeaturePython)
  n = 1
  ref = O_element
FEATURE [App::DocumentObjectGroupPython] G4_N_BUTYL_ALCOHOL  label="G4_N-BUTYL_ALCOHOL"  # scripted group (container) (typed FeaturePython)
  Dunit = g/cm3
  Dvalue = 0.8098
  Group = -> [C_element020,H_element019,O_element018]
  conduct = 2
  density = 1
  expand = 3
  formula = G4_N-BUTYL_ALCOHOL
  name = G4_N-BUTYL_ALCOHOL
  specific = 4
FEATURE [App::DocumentObjectGroupPython] H_element020  label="H_element : 0.025"  # scripted group (container) (typed FeaturePython)
  n = 0.02468
FEATURE [App::DocumentObjectGroupPython] C_element021  label="C_element : 0.502"  # scripted group (container) (typed FeaturePython)
  n = 0.501611
FEATURE [App::DocumentObjectGroupPython] O_element019  label="O_element : 0.005"  # scripted group (container) (typed FeaturePython)
  n = 0.004527
FEATURE [App::DocumentObjectGroupPython] F_element004  label="F_element : 0.465"  # scripted group (container) (typed FeaturePython)
  n = 0.465209
FEATURE [App::DocumentObjectGroupPython] Si_element001  label="Si_element : 0.004"  # scripted group (container) (typed FeaturePython)
  n = 0.003973
FEATURE [App::DocumentObjectGroupPython] G4_C_552  label="G4_C-552"  # scripted group (container) (typed FeaturePython)
  Dunit = g/cm3
  Dvalue = 1.76
  Group = -> [H_element020,C_element021,O_element019,F_element004,Si_element001]
  conduct = 2
  density = 1
  expand = 3
  formula = G4_C-552
  name = G4_C-552
  specific = 4
FEATURE [App::DocumentObjectGroupPython] Cd_element001  label="Cd_element : 1"  # scripted group (container) (typed FeaturePython)
  n = 1
  ref = Cd_element
FEATURE [App::DocumentObjectGroupPython] Te_element001  label="Te_element : 1"  # scripted group (container) (typed FeaturePython)
  n = 1
  ref = Te_element
FEATURE [App::DocumentObjectGroupPython] G4_CADMIUM_TELLURIDE  # scripted group (container) (typed FeaturePython)
  Dunit = g/cm3
  Dvalue = 6.2
  Group = -> [Cd_element001,Te_element001]
  conduct = 2
  density = 1
  expand = 3
  formula = G4_CADMIUM_TELLURIDE
  name = G4_CADMIUM_TELLURIDE
  specific = 4
FEATURE [App::DocumentObjectGroupPython] Cd_element002  label="Cd_element : 002"  # scripted group (container) (typed FeaturePython)
  n = 1
  ref = Cd_element
FEATURE [App::DocumentObjectGroupPython] W_element001  label="W_element : 1"  # scripted group (container) (typed FeaturePython)
  n = 1
  ref = W_element
FEATURE [App::DocumentObjectGroupPython] O_element020  label="O_element : 008"  # scripted group (container) (typed FeaturePython)
  n = 4
  ref = O_element
FEATURE [App::DocumentObjectGroupPython] G4_CADMIUM_TUNGSTATE  # scripted group (container) (typed FeaturePython)
  Dunit = g/cm3
  Dvalue = 7.9
  Group = -> [Cd_element002,W_element001,O_element020]
  conduct = 2
  density = 1
  expand = 3
  formula = G4_CADMIUM_TUNGSTATE
  name = G4_CADMIUM_TUNGSTATE
  specific = 4
FEATURE [App::DocumentObjectGroupPython] Ca_element005  label="Ca_element : 1"  # scripted group (container) (typed FeaturePython)
  n = 1
  ref = Ca_element
FEATURE [App::DocumentObjectGroupPython] C_element022  label="C_element : 009"  # scripted group (container) (typed FeaturePython)
  n = 1
  ref = C_element
FEATURE [App::DocumentObjectGroupPython] O_element021  label="O_element : 009"  # scripted group (container) (typed FeaturePython)
  n = 3
  ref = O_element
FEATURE [App::DocumentObjectGroupPython] G4_CALCIUM_CARBONATE  # scripted group (container) (typed FeaturePython)
  Dunit = g/cm3
  Dvalue = 2.8
  Group = -> [Ca_element005,C_element022,O_element021]
  conduct = 2
  density = 1
  expand = 3
  formula = G4_CALCIUM_CARBONATE
  name = G4_CALCIUM_CARBONATE
  specific = 4
FEATURE [App::DocumentObjectGroupPython] Ca_element006  label="Ca_element : 002"  # scripted group (container) (typed FeaturePython)
  n = 1
  ref = Ca_element
FEATURE [App::DocumentObjectGroupPython] F_element005  label="F_element : 003"  # scripted group (container) (typed FeaturePython)
  n = 2
  ref = F_element
FEATURE [App::DocumentObjectGroupPython] G4_CALCIUM_FLUORIDE  # scripted group (container) (typed FeaturePython)
  Dunit = g/cm3
  Dvalue = 3.18
  Group = -> [Ca_element006,F_element005]
  conduct = 2
  density = 1
  expand = 3
  formula = G4_CALCIUM_FLUORIDE
  name = G4_CALCIUM_FLUORIDE
  specific = 4
FEATURE [App::DocumentObjectGroupPython] Ca_element007  label="Ca_element : 003"  # scripted group (container) (typed FeaturePython)
  n = 1
  ref = Ca_element
FEATURE [App::DocumentObjectGroupPython] O_element022  label="O_element : 010"  # scripted group (container) (typed FeaturePython)
  n = 1
  ref = O_element
FEATURE [App::DocumentObjectGroupPython] G4_CALCIUM_OXIDE  # scripted group (container) (typed FeaturePython)
  Dunit = g/cm3
  Dvalue = 3.3
  Group = -> [Ca_element007,O_element022]
  conduct = 2
  density = 1
  expand = 3
  formula = G4_CALCIUM_OXIDE
  name = G4_CALCIUM_OXIDE
  specific = 4
FEATURE [App::DocumentObjectGroupPython] Ca_element008  label="Ca_element : 004"  # scripted group (container) (typed FeaturePython)
  n = 1
  ref = Ca_element
FEATURE [App::DocumentObjectGroupPython] S_element007  label="S_element : 002"  # scripted group (container) (typed FeaturePython)
  n = 1
  ref = S_element
FEATURE [App::DocumentObjectGroupPython] O_element023  label="O_element : 011"  # scripted group (container) (typed FeaturePython)
  n = 4
  ref = O_element
FEATURE [App::DocumentObjectGroupPython] G4_CALCIUM_SULFATE  # scripted group (container) (typed FeaturePython)
  Dunit = g/cm3
  Dvalue = 2.96
  Group = -> [Ca_element008,S_element007,O_element023]
  conduct = 2
  density = 1
  expand = 3
  formula = G4_CALCIUM_SULFATE
  name = G4_CALCIUM_SULFATE
  specific = 4
FEATURE [App::DocumentObjectGroupPython] Ca_element009  label="Ca_element : 005"  # scripted group (container) (typed FeaturePython)
  n = 1
  ref = Ca_element
FEATURE [App::DocumentObjectGroupPython] W_element002  label="W_element : 002"  # scripted group (container) (typed FeaturePython)
  n = 1
  ref = W_element
FEATURE [App::DocumentObjectGroupPython] O_element024  label="O_element : 012"  # scripted group (container) (typed FeaturePython)
  n = 4
  ref = O_element
FEATURE [App::DocumentObjectGroupPython] G4_CALCIUM_TUNGSTATE  # scripted group (container) (typed FeaturePython)
  Dunit = g/cm3
  Dvalue = 6.062
  Group = -> [Ca_element009,W_element002,O_element024]
  conduct = 2
  density = 1
  expand = 3
  formula = G4_CALCIUM_TUNGSTATE
  name = G4_CALCIUM_TUNGSTATE
  specific = 4
FEATURE [App::DocumentObjectGroupPython] C_element023  label="C_element : 010"  # scripted group (container) (typed FeaturePython)
  n = 1
  ref = C_element
FEATURE [App::DocumentObjectGroupPython] O_element025  label="O_element : 013"  # scripted group (container) (typed FeaturePython)
  n = 2
  ref = O_element
FEATURE [App::DocumentObjectGroupPython] G4_CARBON_DIOXIDE  # scripted group (container) (typed FeaturePython)
  Dunit = g/cm3
  Dvalue = 0.00184212
  Group = -> [C_element023,O_element025]
  conduct = 2
  density = 1
  expand = 3
  formula = G4_CARBON_DIOXIDE
  name = G4_CARBON_DIOXIDE
  specific = 4
FEATURE [App::DocumentObjectGroupPython] C_element024  label="C_element : 011"  # scripted group (container) (typed FeaturePython)
  n = 1
  ref = C_element
FEATURE [App::DocumentObjectGroupPython] Cl_element004  label="Cl_element : 4"  # scripted group (container) (typed FeaturePython)
  n = 4
  ref = Cl_element
FEATURE [App::DocumentObjectGroupPython] G4_CARBON_TETRACHLORIDE  # scripted group (container) (typed FeaturePython)
  Dunit = g/cm3
  Dvalue = 1.594
  Group = -> [C_element024,Cl_element004]
  conduct = 2
  density = 1
  expand = 3
  formula = G4_CARBON_TETRACHLORIDE
  name = G4_CARBON_TETRACHLORIDE
  specific = 4
FEATURE [App::DocumentObjectGroupPython] C_element025  label="C_element : 012"  # scripted group (container) (typed FeaturePython)
  n = 6
  ref = C_element
FEATURE [App::DocumentObjectGroupPython] H_element021  label="H_element : 012"  # scripted group (container) (typed FeaturePython)
  n = 10
  ref = H_element
FEATURE [App::DocumentObjectGroupPython] O_element026  label="O_element : 5"  # scripted group (container) (typed FeaturePython)
  n = 5
  ref = O_element
FEATURE [App::DocumentObjectGroupPython] G4_CELLULOSE_CELLOPHANE  # scripted group (container) (typed FeaturePython)
  Dunit = g/cm3
  Dvalue = 1.42
  Group = -> [C_element025,H_element021,O_element026]
  conduct = 2
  density = 1
  expand = 3
  formula = G4_CELLULOSE_CELLOPHANE
  name = G4_CELLULOSE_CELLOPHANE
  specific = 4
FEATURE [App::DocumentObjectGroupPython] H_element022  label="H_element : 0.067"  # scripted group (container) (typed FeaturePython)
  n = 0.067125
FEATURE [App::DocumentObjectGroupPython] C_element026  label="C_element : 0.545"  # scripted group (container) (typed FeaturePython)
  n = 0.545403
FEATURE [App::DocumentObjectGroupPython] O_element027  label="O_element : 0.387"  # scripted group (container) (typed FeaturePython)
  n = 0.387472
FEATURE [App::DocumentObjectGroupPython] G4_CELLULOSE_BUTYRATE  # scripted group (container) (typed FeaturePython)
  Dunit = g/cm3
  Dvalue = 1.2
  Group = -> [H_element022,C_element026,O_element027]
  conduct = 2
  density = 1
  expand = 3
  formula = G4_CELLULOSE_BUTYRATE
  name = G4_CELLULOSE_BUTYRATE
  specific = 4
FEATURE [App::DocumentObjectGroupPython] H_element023  label="H_element : 0.029"  # scripted group (container) (typed FeaturePython)
  n = 0.029216
FEATURE [App::DocumentObjectGroupPython] C_element027  label="C_element : 0.271"  # scripted group (container) (typed FeaturePython)
  n = 0.271296
FEATURE [App::DocumentObjectGroupPython] N_element013  label="N_element : 0.121"  # scripted group (container) (typed FeaturePython)
  n = 0.121276
FEATURE [App::DocumentObjectGroupPython] O_element028  label="O_element : 0.578"  # scripted group (container) (typed FeaturePython)
  n = 0.578212
FEATURE [App::DocumentObjectGroupPython] G4_CELLULOSE_NITRATE  # scripted group (container) (typed FeaturePython)
  Dunit = g/cm3
  Dvalue = 1.49
  Group = -> [H_element023,C_element027,N_element013,O_element028]
  conduct = 2
  density = 1
  expand = 3
  formula = G4_CELLULOSE_NITRATE
  name = G4_CELLULOSE_NITRATE
  specific = 4
FEATURE [App::DocumentObjectGroupPython] H_element024  label="H_element : 0.108"  # scripted group (container) (typed FeaturePython)
  n = 0.107596
FEATURE [App::DocumentObjectGroupPython] N_element014  label="N_element : 0.001"  # scripted group (container) (typed FeaturePython)
  n = 0.0008
FEATURE [App::DocumentObjectGroupPython] O_element029  label="O_element : 0.875"  # scripted group (container) (typed FeaturePython)
  n = 0.874976
FEATURE [App::DocumentObjectGroupPython] S_element008  label="S_element : 0.015"  # scripted group (container) (typed FeaturePython)
  n = 0.014627
FEATURE [App::DocumentObjectGroupPython] Ce_element001  label="Ce_element : 0.002"  # scripted group (container) (typed FeaturePython)
  n = 0.002001
FEATURE [App::DocumentObjectGroupPython] G4_CERIC_SULFATE  # scripted group (container) (typed FeaturePython)
  Dunit = g/cm3
  Dvalue = 1.03
  Group = -> [H_element024,N_element014,O_element029,S_element008,Ce_element001]
  conduct = 2
  density = 1
  expand = 3
  formula = G4_CERIC_SULFATE
  name = G4_CERIC_SULFATE
  specific = 4
FEATURE [App::DocumentObjectGroupPython] Cs_element001  label="Cs_element : 1"  # scripted group (container) (typed FeaturePython)
  n = 1
  ref = Cs_element
FEATURE [App::DocumentObjectGroupPython] F_element006  label="F_element : 1"  # scripted group (container) (typed FeaturePython)
  n = 1
  ref = F_element
FEATURE [App::DocumentObjectGroupPython] G4_CESIUM_FLUORIDE  # scripted group (container) (typed FeaturePython)
  Dunit = g/cm3
  Dvalue = 4.115
  Group = -> [Cs_element001,F_element006]
  conduct = 2
  density = 1
  expand = 3
  formula = G4_CESIUM_FLUORIDE
  name = G4_CESIUM_FLUORIDE
  specific = 4
FEATURE [App::DocumentObjectGroupPython] Cs_element002  label="Cs_element : 002"  # scripted group (container) (typed FeaturePython)
  n = 1
  ref = Cs_element
FEATURE [App::DocumentObjectGroupPython] I_element001  label="I_element : 1"  # scripted group (container) (typed FeaturePython)
  n = 1
  ref = I_element
FEATURE [App::DocumentObjectGroupPython] G4_CESIUM_IODIDE  # scripted group (container) (typed FeaturePython)
  Dunit = g/cm3
  Dvalue = 4.51
  Group = -> [Cs_element002,I_element001]
  conduct = 2
  density = 1
  expand = 3
  formula = G4_CESIUM_IODIDE
  name = G4_CESIUM_IODIDE
  specific = 4
FEATURE [App::DocumentObjectGroupPython] C_element028  label="C_element : 013"  # scripted group (container) (typed FeaturePython)
  n = 6
  ref = C_element
FEATURE [App::DocumentObjectGroupPython] H_element025  label="H_element : 013"  # scripted group (container) (typed FeaturePython)
  n = 5
  ref = H_element
FEATURE [App::DocumentObjectGroupPython] Cl_element005  label="Cl_element : 1"  # scripted group (container) (typed FeaturePython)
  n = 1
  ref = Cl_element
FEATURE [App::DocumentObjectGroupPython] G4_CHLOROBENZENE  # scripted group (container) (typed FeaturePython)
  Dunit = g/cm3
  Dvalue = 1.1058
  Group = -> [C_element028,H_element025,Cl_element005]
  conduct = 2
  density = 1
  expand = 3
  formula = G4_CHLOROBENZENE
  name = G4_CHLOROBENZENE
  specific = 4
FEATURE [App::DocumentObjectGroupPython] C_element029  label="C_element : 014"  # scripted group (container) (typed FeaturePython)
  n = 1
  ref = C_element
FEATURE [App::DocumentObjectGroupPython] H_element026  label="H_element : 1"  # scripted group (container) (typed FeaturePython)
  n = 1
  ref = H_element
FEATURE [App::DocumentObjectGroupPython] Cl_element006  label="Cl_element : 3"  # scripted group (container) (typed FeaturePython)
  n = 3
  ref = Cl_element
FEATURE [App::DocumentObjectGroupPython] G4_CHLOROFORM  # scripted group (container) (typed FeaturePython)
  Dunit = g/cm3
  Dvalue = 1.4832
  Group = -> [C_element029,H_element026,Cl_element006]
  conduct = 2
  density = 1
  expand = 3
  formula = G4_CHLOROFORM
  name = G4_CHLOROFORM
  specific = 4
FEATURE [App::DocumentObjectGroupPython] H_element027  label="H_element : 0.010"  # scripted group (container) (typed FeaturePython)
  n = 0.01
FEATURE [App::DocumentObjectGroupPython] C_element030  label="C_element : 0.001"  # scripted group (container) (typed FeaturePython)
  n = 0.001
FEATURE [App::DocumentObjectGroupPython] O_element030  label="O_element : 0.529"  # scripted group (container) (typed FeaturePython)
  n = 0.529107
FEATURE [App::DocumentObjectGroupPython] Na_element005  label="Na_element : 0.016"  # scripted group (container) (typed FeaturePython)
  n = 0.016
FEATURE [App::DocumentObjectGroupPython] Mg_element003  label="Mg_element : 0.004"  # scripted group (container) (typed FeaturePython)
  n = 0.002
FEATURE [App::DocumentObjectGroupPython] Al_element002  label="Al_element : 0.034"  # scripted group (container) (typed FeaturePython)
  n = 0.033872
FEATURE [App::DocumentObjectGroupPython] Si_element002  label="Si_element : 0.337"  # scripted group (container) (typed FeaturePython)
  n = 0.337021
FEATURE [App::DocumentObjectGroupPython] K_element003  label="K_element : 0.013"  # scripted group (container) (typed FeaturePython)
  n = 0.013
FEATURE [App::DocumentObjectGroupPython] Ca_element010  label="Ca_element : 0.044"  # scripted group (container) (typed FeaturePython)
  n = 0.044
FEATURE [App::DocumentObjectGroupPython] Fe_element002  label="Fe_element : 0.014"  # scripted group (container) (typed FeaturePython)
  n = 0.014
FEATURE [App::DocumentObjectGroupPython] G4_CONCRETE  # scripted group (container) (typed FeaturePython)
  Dunit = g/cm3
  Dvalue = 2.3
  Group = -> [H_element027,C_element030,O_element030,Na_element005,Mg_element003,Al_element002,Si_element002,K_element003,Ca_element010,Fe_element002]
  conduct = 2
  density = 1
  expand = 3
  formula = G4_CONCRETE
  name = G4_CONCRETE
  specific = 4
FEATURE [App::DocumentObjectGroupPython] C_element031  label="C_element : 015"  # scripted group (container) (typed FeaturePython)
  n = 6
  ref = C_element
FEATURE [App::DocumentObjectGroupPython] H_element028  label="H_element : 12"  # scripted group (container) (typed FeaturePython)
  n = 12
  ref = H_element
FEATURE [App::DocumentObjectGroupPython] G4_CYCLOHEXANE  # scripted group (container) (typed FeaturePython)
  Dunit = g/cm3
  Dvalue = 0.779
  Group = -> [C_element031,H_element028]
  conduct = 2
  density = 1
  expand = 3
  formula = G4_CYCLOHEXANE
  name = G4_CYCLOHEXANE
  specific = 4
FEATURE [App::DocumentObjectGroupPython] C_element032  label="C_element : 016"  # scripted group (container) (typed FeaturePython)
  n = 6
  ref = C_element
FEATURE [App::DocumentObjectGroupPython] H_element029  label="H_element : 4"  # scripted group (container) (typed FeaturePython)
  n = 4
  ref = H_element
FEATURE [App::DocumentObjectGroupPython] Cl_element007  label="Cl_element : 2"  # scripted group (container) (typed FeaturePython)
  n = 2
  ref = Cl_element
FEATURE [App::DocumentObjectGroupPython] G4_1_2_DICHLOROBENZENE  label="G4_1.2-DICHLOROBENZENE"  # scripted group (container) (typed FeaturePython)
  Dunit = g/cm3
  Dvalue = 1.3048
  Group = -> [C_element032,H_element029,Cl_element007]
  conduct = 2
  density = 1
  expand = 3
  formula = G4_1.2-DICHLOROBENZENE
  name = G4_1.2-DICHLOROBENZENE
  specific = 4
FEATURE [App::DocumentObjectGroupPython] C_element033  label="C_element : 017"  # scripted group (container) (typed FeaturePython)
  n = 4
  ref = C_element
FEATURE [App::DocumentObjectGroupPython] H_element030  label="H_element : 8"  # scripted group (container) (typed FeaturePython)
  n = 8
  ref = H_element
FEATURE [App::DocumentObjectGroupPython] O_element031  label="O_element : 014"  # scripted group (container) (typed FeaturePython)
  n = 1
  ref = O_element
FEATURE [App::DocumentObjectGroupPython] Cl_element008  label="Cl_element : 005"  # scripted group (container) (typed FeaturePython)
  n = 2
  ref = Cl_element
FEATURE [App::DocumentObjectGroupPython] G4_DICHLORODIETHYL_ETHER  # scripted group (container) (typed FeaturePython)
  Dunit = g/cm3
  Dvalue = 1.2199
  Group = -> [C_element033,H_element030,O_element031,Cl_element008]
  conduct = 2
  density = 1
  expand = 3
  formula = G4_DICHLORODIETHYL_ETHER
  name = G4_DICHLORODIETHYL_ETHER
  specific = 4
FEATURE [App::DocumentObjectGroupPython] C_element034  label="C_element : 018"  # scripted group (container) (typed FeaturePython)
  n = 2
  ref = C_element
FEATURE [App::DocumentObjectGroupPython] H_element031  label="H_element : 014"  # scripted group (container) (typed FeaturePython)
  n = 4
  ref = H_element
FEATURE [App::DocumentObjectGroupPython] Cl_element009  label="Cl_element : 006"  # scripted group (container) (typed FeaturePython)
  n = 2
  ref = Cl_element
FEATURE [App::DocumentObjectGroupPython] G4_1_2_DICHLOROETHANE  label="G4_1.2-DICHLOROETHANE"  # scripted group (container) (typed FeaturePython)
  Dunit = g/cm3
  Dvalue = 1.2351
  Group = -> [C_element034,H_element031,Cl_element009]
  conduct = 2
  density = 1
  expand = 3
  formula = G4_1.2-DICHLOROETHANE
  name = G4_1.2-DICHLOROETHANE
  specific = 4
FEATURE [App::DocumentObjectGroupPython] C_element035  label="C_element : 019"  # scripted group (container) (typed FeaturePython)
  n = 4
  ref = C_element
FEATURE [App::DocumentObjectGroupPython] H_element032  label="H_element : 015"  # scripted group (container) (typed FeaturePython)
  n = 10
  ref = H_element
FEATURE [App::DocumentObjectGroupPython] O_element032  label="O_element : 015"  # scripted group (container) (typed FeaturePython)
  n = 1
  ref = O_element
FEATURE [App::DocumentObjectGroupPython] G4_DIETHYL_ETHER  # scripted group (container) (typed FeaturePython)
  Dunit = g/cm3
  Dvalue = 0.71378
  Group = -> [C_element035,H_element032,O_element032]
  conduct = 2
  density = 1
  expand = 3
  formula = G4_DIETHYL_ETHER
  name = G4_DIETHYL_ETHER
  specific = 4
FEATURE [App::DocumentObjectGroupPython] C_element036  label="C_element : 020"  # scripted group (container) (typed FeaturePython)
  n = 3
  ref = C_element
FEATURE [App::DocumentObjectGroupPython] H_element033  label="H_element : 016"  # scripted group (container) (typed FeaturePython)
  n = 7
  ref = H_element
FEATURE [App::DocumentObjectGroupPython] N_element015  label="N_element : 008"  # scripted group (container) (typed FeaturePython)
  n = 1
  ref = N_element
FEATURE [App::DocumentObjectGroupPython] O_element033  label="O_element : 016"  # scripted group (container) (typed FeaturePython)
  n = 1
  ref = O_element
FEATURE [App::DocumentObjectGroupPython] G4_N_N_DIMETHYL_FORMAMIDE  label="G4_N.N-DIMETHYL_FORMAMIDE"  # scripted group (container) (typed FeaturePython)
  Dunit = g/cm3
  Dvalue = 0.9487
  Group = -> [C_element036,H_element033,N_element015,O_element033]
  conduct = 2
  density = 1
  expand = 3
  formula = G4_N.N-DIMETHYL_FORMAMIDE
  name = G4_N.N-DIMETHYL_FORMAMIDE
  specific = 4
FEATURE [App::DocumentObjectGroupPython] C_element037  label="C_element : 021"  # scripted group (container) (typed FeaturePython)
  n = 2
  ref = C_element
FEATURE [App::DocumentObjectGroupPython] H_element034  label="H_element : 017"  # scripted group (container) (typed FeaturePython)
  n = 6
  ref = H_element
FEATURE [App::DocumentObjectGroupPython] O_element034  label="O_element : 017"  # scripted group (container) (typed FeaturePython)
  n = 1
  ref = O_element
FEATURE [App::DocumentObjectGroupPython] S_element009  label="S_element : 003"  # scripted group (container) (typed FeaturePython)
  n = 1
  ref = S_element
FEATURE [App::DocumentObjectGroupPython] G4_DIMETHYL_SULFOXIDE  # scripted group (container) (typed FeaturePython)
  Dunit = g/cm3
  Dvalue = 1.1014
  Group = -> [C_element037,H_element034,O_element034,S_element009]
  conduct = 2
  density = 1
  expand = 3
  formula = G4_DIMETHYL_SULFOXIDE
  name = G4_DIMETHYL_SULFOXIDE
  specific = 4
FEATURE [App::DocumentObjectGroupPython] C_element038  label="C_element : 022"  # scripted group (container) (typed FeaturePython)
  n = 2
  ref = C_element
FEATURE [App::DocumentObjectGroupPython] H_element035  label="H_element : 018"  # scripted group (container) (typed FeaturePython)
  n = 6
  ref = H_element
FEATURE [App::DocumentObjectGroupPython] G4_ETHANE  # scripted group (container) (typed FeaturePython)
  Dunit = g/cm3
  Dvalue = 0.00125324
  Group = -> [C_element038,H_element035]
  conduct = 2
  density = 1
  expand = 3
  formula = G4_ETHANE
  name = G4_ETHANE
  specific = 4
FEATURE [App::DocumentObjectGroupPython] C_element039  label="C_element : 023"  # scripted group (container) (typed FeaturePython)
  n = 2
  ref = C_element
FEATURE [App::DocumentObjectGroupPython] H_element036  label="H_element : 019"  # scripted group (container) (typed FeaturePython)
  n = 6
  ref = H_element
FEATURE [App::DocumentObjectGroupPython] O_element035  label="O_element : 018"  # scripted group (container) (typed FeaturePython)
  n = 1
  ref = O_element
FEATURE [App::DocumentObjectGroupPython] G4_ETHYL_ALCOHOL  # scripted group (container) (typed FeaturePython)
  Dunit = g/cm3
  Dvalue = 0.7893
  Group = -> [C_element039,H_element036,O_element035]
  conduct = 2
  density = 1
  expand = 3
  formula = G4_ETHYL_ALCOHOL
  name = G4_ETHYL_ALCOHOL
  specific = 4
FEATURE [App::DocumentObjectGroupPython] H_element037  label="H_element : 0.090"  # scripted group (container) (typed FeaturePython)
  n = 0.090027
FEATURE [App::DocumentObjectGroupPython] C_element040  label="C_element : 0.585"  # scripted group (container) (typed FeaturePython)
  n = 0.585182
FEATURE [App::DocumentObjectGroupPython] O_element036  label="O_element : 0.325"  # scripted group (container) (typed FeaturePython)
  n = 0.324791
FEATURE [App::DocumentObjectGroupPython] G4_ETHYL_CELLULOSE  # scripted group (container) (typed FeaturePython)
  Dunit = g/cm3
  Dvalue = 1.13
  Group = -> [H_element037,C_element040,O_element036]
  conduct = 2
  density = 1
  expand = 3
  formula = G4_ETHYL_CELLULOSE
  name = G4_ETHYL_CELLULOSE
  specific = 4
FEATURE [App::DocumentObjectGroupPython] C_element041  label="C_element : 024"  # scripted group (container) (typed FeaturePython)
  n = 2
  ref = C_element
FEATURE [App::DocumentObjectGroupPython] H_element038  label="H_element : 020"  # scripted group (container) (typed FeaturePython)
  n = 4
  ref = H_element
FEATURE [App::DocumentObjectGroupPython] G4_ETHYLENE  # scripted group (container) (typed FeaturePython)
  Dunit = g/cm3
  Dvalue = 0.00117497
  Group = -> [C_element041,H_element038]
  conduct = 2
  density = 1
  expand = 3
  formula = G4_ETHYLENE
  name = G4_ETHYLENE
  specific = 4
FEATURE [App::DocumentObjectGroupPython] H_element039  label="H_element : 0.096"  # scripted group (container) (typed FeaturePython)
  n = 0.096
FEATURE [App::DocumentObjectGroupPython] C_element042  label="C_element : 0.195"  # scripted group (container) (typed FeaturePython)
  n = 0.195
FEATURE [App::DocumentObjectGroupPython] N_element016  label="N_element : 0.057"  # scripted group (container) (typed FeaturePython)
  n = 0.057
FEATURE [App::DocumentObjectGroupPython] O_element037  label="O_element : 0.646"  # scripted group (container) (typed FeaturePython)
  n = 0.646
FEATURE [App::DocumentObjectGroupPython] Na_element006  label="Na_element : 0.017"  # scripted group (container) (typed FeaturePython)
  n = 0.001
FEATURE [App::DocumentObjectGroupPython] P_element005  label="P_element : 0.104"  # scripted group (container) (typed FeaturePython)
  n = 0.001
FEATURE [App::DocumentObjectGroupPython] S_element010  label="S_element : 0.016"  # scripted group (container) (typed FeaturePython)
  n = 0.003
FEATURE [App::DocumentObjectGroupPython] Cl_element010  label="Cl_element : 0.005"  # scripted group (container) (typed FeaturePython)
  n = 0.001
FEATURE [App::DocumentObjectGroupPython] G4_EYE_LENS_ICRP  # scripted group (container) (typed FeaturePython)
  Dunit = g/cm3
  Dvalue = 1.07
  Group = -> [H_element039,C_element042,N_element016,O_element037,Na_element006,P_element005,S_element010,Cl_element010]
  conduct = 2
  density = 1
  expand = 3
  formula = G4_EYE_LENS_ICRP
  name = G4_EYE_LENS_ICRP
  specific = 4
FEATURE [App::DocumentObjectGroupPython] Fe_element003  label="Fe_element : 2"  # scripted group (container) (typed FeaturePython)
  n = 2
  ref = Fe_element
FEATURE [App::DocumentObjectGroupPython] O_element038  label="O_element : 019"  # scripted group (container) (typed FeaturePython)
  n = 3
  ref = O_element
FEATURE [App::DocumentObjectGroupPython] G4_FERRIC_OXIDE  # scripted group (container) (typed FeaturePython)
  Dunit = g/cm3
  Dvalue = 5.2
  Group = -> [Fe_element003,O_element038]
  conduct = 2
  density = 1
  expand = 3
  formula = G4_FERRIC_OXIDE
  name = G4_FERRIC_OXIDE
  specific = 4
FEATURE [App::DocumentObjectGroupPython] Fe_element004  label="Fe_element : 1"  # scripted group (container) (typed FeaturePython)
  n = 1
  ref = Fe_element
FEATURE [App::DocumentObjectGroupPython] B_element003  label="B_element : 1"  # scripted group (container) (typed FeaturePython)
  n = 1
  ref = B_element
FEATURE [App::DocumentObjectGroupPython] G4_FERROBORIDE  # scripted group (container) (typed FeaturePython)
  Dunit = g/cm3
  Dvalue = 7.15
  Group = -> [Fe_element004,B_element003]
  conduct = 2
  density = 1
  expand = 3
  formula = G4_FERROBORIDE
  name = G4_FERROBORIDE
  specific = 4
FEATURE [App::DocumentObjectGroupPython] Fe_element005  label="Fe_element : 003"  # scripted group (container) (typed FeaturePython)
  n = 1
  ref = Fe_element
FEATURE [App::DocumentObjectGroupPython] O_element039  label="O_element : 020"  # scripted group (container) (typed FeaturePython)
  n = 1
  ref = O_element
FEATURE [App::DocumentObjectGroupPython] G4_FERROUS_OXIDE  # scripted group (container) (typed FeaturePython)
  Dunit = g/cm3
  Dvalue = 5.7
  Group = -> [Fe_element005,O_element039]
  conduct = 2
  density = 1
  expand = 3
  formula = G4_FERROUS_OXIDE
  name = G4_FERROUS_OXIDE
  specific = 4
FEATURE [App::DocumentObjectGroupPython] H_element040  label="H_element : 0.115"  # scripted group (container) (typed FeaturePython)
  n = 0.108259
FEATURE [App::DocumentObjectGroupPython] N_element017  label="N_element : 0.000"  # scripted group (container) (typed FeaturePython)
  n = 2.7e-05
FEATURE [App::DocumentObjectGroupPython] O_element040  label="O_element : 0.879"  # scripted group (container) (typed FeaturePython)
  n = 0.878636
FEATURE [App::DocumentObjectGroupPython] Na_element007  label="Na_element : 0.000"  # scripted group (container) (typed FeaturePython)
  n = 2.2e-05
FEATURE [App::DocumentObjectGroupPython] S_element011  label="S_element : 0.013"  # scripted group (container) (typed FeaturePython)
  n = 0.012968
FEATURE [App::DocumentObjectGroupPython] Cl_element011  label="Cl_element : 0.000"  # scripted group (container) (typed FeaturePython)
  n = 3.4e-05
FEATURE [App::DocumentObjectGroupPython] Fe_element006  label="Fe_element : 0.000"  # scripted group (container) (typed FeaturePython)
  n = 5.4e-05
FEATURE [App::DocumentObjectGroupPython] G4_FERROUS_SULFATE  # scripted group (container) (typed FeaturePython)
  Dunit = g/cm3
  Dvalue = 1.024
  Group = -> [H_element040,N_element017,O_element040,Na_element007,S_element011,Cl_element011,Fe_element006]
  conduct = 2
  density = 1
  expand = 3
  formula = G4_FERROUS_SULFATE
  name = G4_FERROUS_SULFATE
  specific = 4
FEATURE [App::DocumentObjectGroupPython] C_element043  label="C_element : 0.099"  # scripted group (container) (typed FeaturePython)
  n = 0.099335
FEATURE [App::DocumentObjectGroupPython] F_element007  label="F_element : 0.314"  # scripted group (container) (typed FeaturePython)
  n = 0.314247
FEATURE [App::DocumentObjectGroupPython] Cl_element012  label="Cl_element : 0.586"  # scripted group (container) (typed FeaturePython)
  n = 0.586418
FEATURE [App::DocumentObjectGroupPython] G4_FREON_12  label="G4_FREON-12"  # scripted group (container) (typed FeaturePython)
  Dunit = g/cm3
  Dvalue = 1.12
  Group = -> [C_element043,F_element007,Cl_element012]
  conduct = 2
  density = 1
  expand = 3
  formula = G4_FREON-12
  name = G4_FREON-12
  specific = 4
FEATURE [App::DocumentObjectGroupPython] C_element044  label="C_element : 0.057"  # scripted group (container) (typed FeaturePython)
  n = 0.057245
FEATURE [App::DocumentObjectGroupPython] F_element008  label="F_element : 0.181"  # scripted group (container) (typed FeaturePython)
  n = 0.181096
FEATURE [App::DocumentObjectGroupPython] Br_element001  label="Br_element : 0.762"  # scripted group (container) (typed FeaturePython)
  n = 0.761659
FEATURE [App::DocumentObjectGroupPython] G4_FREON_12B2  label="G4_FREON-12B2"  # scripted group (container) (typed FeaturePython)
  Dunit = g/cm3
  Dvalue = 1.8
  Group = -> [C_element044,F_element008,Br_element001]
  conduct = 2
  density = 1
  expand = 3
  formula = G4_FREON-12B2
  name = G4_FREON-12B2
  specific = 4
FEATURE [App::DocumentObjectGroupPython] C_element045  label="C_element : 0.115"  # scripted group (container) (typed FeaturePython)
  n = 0.114983
FEATURE [App::DocumentObjectGroupPython] F_element009  label="F_element : 0.546"  # scripted group (container) (typed FeaturePython)
  n = 0.545621
FEATURE [App::DocumentObjectGroupPython] Cl_element013  label="Cl_element : 0.339"  # scripted group (container) (typed FeaturePython)
  n = 0.339396
FEATURE [App::DocumentObjectGroupPython] G4_FREON_13  label="G4_FREON-13"  # scripted group (container) (typed FeaturePython)
  Dunit = g/cm3
  Dvalue = 0.95
  Group = -> [C_element045,F_element009,Cl_element013]
  conduct = 2
  density = 1
  expand = 3
  formula = G4_FREON-13
  name = G4_FREON-13
  specific = 4
FEATURE [App::DocumentObjectGroupPython] C_element046  label="C_element : 025"  # scripted group (container) (typed FeaturePython)
  n = 1
  ref = C_element
FEATURE [App::DocumentObjectGroupPython] F_element010  label="F_element : 3"  # scripted group (container) (typed FeaturePython)
  n = 3
  ref = F_element
FEATURE [App::DocumentObjectGroupPython] Br_element002  label="Br_element : 1"  # scripted group (container) (typed FeaturePython)
  n = 1
  ref = Br_element
FEATURE [App::DocumentObjectGroupPython] G4_FREON_13B1  label="G4_FREON-13B1"  # scripted group (container) (typed FeaturePython)
  Dunit = g/cm3
  Dvalue = 1.5
  Group = -> [C_element046,F_element010,Br_element002]
  conduct = 2
  density = 1
  expand = 3
  formula = G4_FREON-13B1
  name = G4_FREON-13B1
  specific = 4
FEATURE [App::DocumentObjectGroupPython] C_element047  label="C_element : 0.061"  # scripted group (container) (typed FeaturePython)
  n = 0.061309
FEATURE [App::DocumentObjectGroupPython] F_element011  label="F_element : 0.291"  # scripted group (container) (typed FeaturePython)
  n = 0.290924
FEATURE [App::DocumentObjectGroupPython] I_element002  label="I_element : 0.648"  # scripted group (container) (typed FeaturePython)
  n = 0.647767
FEATURE [App::DocumentObjectGroupPython] G4_FREON_13I1  label="G4_FREON-13I1"  # scripted group (container) (typed FeaturePython)
  Dunit = g/cm3
  Dvalue = 1.8
  Group = -> [C_element047,F_element011,I_element002]
  conduct = 2
  density = 1
  expand = 3
  formula = G4_FREON-13I1
  name = G4_FREON-13I1
  specific = 4
FEATURE [App::DocumentObjectGroupPython] Gd_element001  label="Gd_element : 2"  # scripted group (container) (typed FeaturePython)
  n = 2
  ref = Gd_element
FEATURE [App::DocumentObjectGroupPython] O_element041  label="O_element : 021"  # scripted group (container) (typed FeaturePython)
  n = 2
  ref = O_element
FEATURE [App::DocumentObjectGroupPython] S_element012  label="S_element : 004"  # scripted group (container) (typed FeaturePython)
  n = 1
  ref = S_element
FEATURE [App::DocumentObjectGroupPython] G4_GADOLINIUM_OXYSULFIDE  # scripted group (container) (typed FeaturePython)
  Dunit = g/cm3
  Dvalue = 7.44
  Group = -> [Gd_element001,O_element041,S_element012]
  conduct = 2
  density = 1
  expand = 3
  formula = G4_GADOLINIUM_OXYSULFIDE
  name = G4_GADOLINIUM_OXYSULFIDE
  specific = 4
FEATURE [App::DocumentObjectGroupPython] Ga_element001  label="Ga_element : 1"  # scripted group (container) (typed FeaturePython)
  n = 1
  ref = Ga_element
FEATURE [App::DocumentObjectGroupPython] As_element001  label="As_element : 1"  # scripted group (container) (typed FeaturePython)
  n = 1
  ref = As_element
FEATURE [App::DocumentObjectGroupPython] G4_GALLIUM_ARSENIDE  # scripted group (container) (typed FeaturePython)
  Dunit = g/cm3
  Dvalue = 5.31
  Group = -> [Ga_element001,As_element001]
  conduct = 2
  density = 1
  expand = 3
  formula = G4_GALLIUM_ARSENIDE
  name = G4_GALLIUM_ARSENIDE
  specific = 4
FEATURE [App::DocumentObjectGroupPython] H_element041  label="H_element : 0.081"  # scripted group (container) (typed FeaturePython)
  n = 0.08118
FEATURE [App::DocumentObjectGroupPython] C_element048  label="C_element : 0.416"  # scripted group (container) (typed FeaturePython)
  n = 0.41606
FEATURE [App::DocumentObjectGroupPython] N_element018  label="N_element : 0.111"  # scripted group (container) (typed FeaturePython)
  n = 0.11124
FEATURE [App::DocumentObjectGroupPython] O_element042  label="O_element : 0.381"  # scripted group (container) (typed FeaturePython)
  n = 0.38064
FEATURE [App::DocumentObjectGroupPython] S_element013  label="S_element : 0.011"  # scripted group (container) (typed FeaturePython)
  n = 0.01088
FEATURE [App::DocumentObjectGroupPython] G4_GEL_PHOTO_EMULSION  # scripted group (container) (typed FeaturePython)
  Dunit = g/cm3
  Dvalue = 1.2914
  Group = -> [H_element041,C_element048,N_element018,O_element042,S_element013]
  conduct = 2
  density = 1
  expand = 3
  formula = G4_GEL_PHOTO_EMULSION
  name = G4_GEL_PHOTO_EMULSION
  specific = 4
FEATURE [App::DocumentObjectGroupPython] B_element004  label="B_element : 0.040"  # scripted group (container) (typed FeaturePython)
  n = 0.0400639
FEATURE [App::DocumentObjectGroupPython] O_element043  label="O_element : 0.540"  # scripted group (container) (typed FeaturePython)
  n = 0.539561
FEATURE [App::DocumentObjectGroupPython] Na_element008  label="Na_element : 0.028"  # scripted group (container) (typed FeaturePython)
  n = 0.0281909
FEATURE [App::DocumentObjectGroupPython] Al_element003  label="Al_element : 0.012"  # scripted group (container) (typed FeaturePython)
  n = 0.011644
FEATURE [App::DocumentObjectGroupPython] Si_element003  label="Si_element : 0.377"  # scripted group (container) (typed FeaturePython)
  n = 0.377219
FEATURE [App::DocumentObjectGroupPython] K_element004  label="K_element : 0.014"  # scripted group (container) (typed FeaturePython)
  n = 0.00332099
FEATURE [App::DocumentObjectGroupPython] G4_Pyrex_Glass  # scripted group (container) (typed FeaturePython)
  Dunit = g/cm3
  Dvalue = 2.23
  Group = -> [B_element004,O_element043,Na_element008,Al_element003,Si_element003,K_element004]
  conduct = 2
  density = 1
  expand = 3
  formula = G4_Pyrex_Glass
  name = G4_Pyrex_Glass
  specific = 4
FEATURE [App::DocumentObjectGroupPython] O_element044  label="O_element : 0.156"  # scripted group (container) (typed FeaturePython)
  n = 0.156453
FEATURE [App::DocumentObjectGroupPython] Si_element004  label="Si_element : 0.081"  # scripted group (container) (typed FeaturePython)
  n = 0.080866
FEATURE [App::DocumentObjectGroupPython] Ti_element001  label="Ti_element : 0.008"  # scripted group (container) (typed FeaturePython)
  n = 0.008092
FEATURE [App::DocumentObjectGroupPython] As_element002  label="As_element : 0.003"  # scripted group (container) (typed FeaturePython)
  n = 0.002651
FEATURE [App::DocumentObjectGroupPython] Pb_element001  label="Pb_element : 0.752"  # scripted group (container) (typed FeaturePython)
  n = 0.751938
FEATURE [App::DocumentObjectGroupPython] G4_GLASS_LEAD  # scripted group (container) (typed FeaturePython)
  Dunit = g/cm3
  Dvalue = 6.22
  Group = -> [O_element044,Si_element004,Ti_element001,As_element002,Pb_element001]
  conduct = 2
  density = 1
  expand = 3
  formula = G4_GLASS_LEAD
  name = G4_GLASS_LEAD
  specific = 4
FEATURE [App::DocumentObjectGroupPython] O_element045  label="O_element : 0.460"  # scripted group (container) (typed FeaturePython)
  n = 0.4598
FEATURE [App::DocumentObjectGroupPython] Na_element009  label="Na_element : 0.096"  # scripted group (container) (typed FeaturePython)
  n = 0.0964411
FEATURE [App::DocumentObjectGroupPython] Si_element005  label="Si_element : 0.378"  # scripted group (container) (typed FeaturePython)
  n = 0.336553
FEATURE [App::DocumentObjectGroupPython] Ca_element011  label="Ca_element : 0.107"  # scripted group (container) (typed FeaturePython)
  n = 0.107205
FEATURE [App::DocumentObjectGroupPython] G4_GLASS_PLATE  # scripted group (container) (typed FeaturePython)
  Dunit = g/cm3
  Dvalue = 2.4
  Group = -> [O_element045,Na_element009,Si_element005,Ca_element011]
  conduct = 2
  density = 1
  expand = 3
  formula = G4_GLASS_PLATE
  name = G4_GLASS_PLATE
  specific = 4
FEATURE [App::DocumentObjectGroupPython] C_element049  label="C_element : 026"  # scripted group (container) (typed FeaturePython)
  n = 5
  ref = C_element
FEATURE [App::DocumentObjectGroupPython] H_element042  label="H_element : 021"  # scripted group (container) (typed FeaturePython)
  n = 10
  ref = H_element
FEATURE [App::DocumentObjectGroupPython] N_element019  label="N_element : 2"  # scripted group (container) (typed FeaturePython)
  n = 2
  ref = N_element
FEATURE [App::DocumentObjectGroupPython] O_element046  label="O_element : 022"  # scripted group (container) (typed FeaturePython)
  n = 3
  ref = O_element
FEATURE [App::DocumentObjectGroupPython] G4_GLUTAMINE  # scripted group (container) (typed FeaturePython)
  Dunit = g/cm3
  Dvalue = 1.46
  Group = -> [C_element049,H_element042,N_element019,O_element046]
  conduct = 2
  density = 1
  expand = 3
  formula = G4_GLUTAMINE
  name = G4_GLUTAMINE
  specific = 4
FEATURE [App::DocumentObjectGroupPython] C_element050  label="C_element : 027"  # scripted group (container) (typed FeaturePython)
  n = 3
  ref = C_element
FEATURE [App::DocumentObjectGroupPython] H_element043  label="H_element : 022"  # scripted group (container) (typed FeaturePython)
  n = 8
  ref = H_element
FEATURE [App::DocumentObjectGroupPython] O_element047  label="O_element : 023"  # scripted group (container) (typed FeaturePython)
  n = 3
  ref = O_element
FEATURE [App::DocumentObjectGroupPython] G4_GLYCEROL  # scripted group (container) (typed FeaturePython)
  Dunit = g/cm3
  Dvalue = 1.2613
  Group = -> [C_element050,H_element043,O_element047]
  conduct = 2
  density = 1
  expand = 3
  formula = G4_GLYCEROL
  name = G4_GLYCEROL
  specific = 4
FEATURE [App::DocumentObjectGroupPython] C_element051  label="C_element : 028"  # scripted group (container) (typed FeaturePython)
  n = 5
  ref = C_element
FEATURE [App::DocumentObjectGroupPython] H_element044  label="H_element : 023"  # scripted group (container) (typed FeaturePython)
  n = 5
  ref = H_element
FEATURE [App::DocumentObjectGroupPython] N_element020  label="N_element : 009"  # scripted group (container) (typed FeaturePython)
  n = 5
  ref = N_element
FEATURE [App::DocumentObjectGroupPython] O_element048  label="O_element : 024"  # scripted group (container) (typed FeaturePython)
  n = 1
  ref = O_element
FEATURE [App::DocumentObjectGroupPython] G4_GUANINE  # scripted group (container) (typed FeaturePython)
  Dunit = g/cm3
  Dvalue = 2.2
  Group = -> [C_element051,H_element044,N_element020,O_element048]
  conduct = 2
  density = 1
  expand = 3
  formula = G4_GUANINE
  name = G4_GUANINE
  specific = 4
FEATURE [App::DocumentObjectGroupPython] Ca_element012  label="Ca_element : 006"  # scripted group (container) (typed FeaturePython)
  n = 1
  ref = Ca_element
FEATURE [App::DocumentObjectGroupPython] S_element014  label="S_element : 005"  # scripted group (container) (typed FeaturePython)
  n = 1
  ref = S_element
FEATURE [App::DocumentObjectGroupPython] O_element049  label="O_element : 6"  # scripted group (container) (typed FeaturePython)
  n = 6
  ref = O_element
FEATURE [App::DocumentObjectGroupPython] H_element045  label="H_element : 024"  # scripted group (container) (typed FeaturePython)
  n = 4
  ref = H_element
FEATURE [App::DocumentObjectGroupPython] G4_GYPSUM  # scripted group (container) (typed FeaturePython)
  Dunit = g/cm3
  Dvalue = 2.32
  Group = -> [Ca_element012,S_element014,O_element049,H_element045]
  conduct = 2
  density = 1
  expand = 3
  formula = G4_GYPSUM
  name = G4_GYPSUM
  specific = 4
FEATURE [App::DocumentObjectGroupPython] C_element052  label="C_element : 7"  # scripted group (container) (typed FeaturePython)
  n = 7
  ref = C_element
FEATURE [App::DocumentObjectGroupPython] H_element046  label="H_element : 16"  # scripted group (container) (typed FeaturePython)
  n = 16
  ref = H_element
FEATURE [App::DocumentObjectGroupPython] G4_N_HEPTANE  label="G4_N-HEPTANE"  # scripted group (container) (typed FeaturePython)
  Dunit = g/cm3
  Dvalue = 0.68376
  Group = -> [C_element052,H_element046]
  conduct = 2
  density = 1
  expand = 3
  formula = G4_N-HEPTANE
  name = G4_N-HEPTANE
  specific = 4
FEATURE [App::DocumentObjectGroupPython] C_element053  label="C_element : 029"  # scripted group (container) (typed FeaturePython)
  n = 6
  ref = C_element
FEATURE [App::DocumentObjectGroupPython] H_element047  label="H_element : 14"  # scripted group (container) (typed FeaturePython)
  n = 14
  ref = H_element
FEATURE [App::DocumentObjectGroupPython] G4_N_HEXANE  label="G4_N-HEXANE"  # scripted group (container) (typed FeaturePython)
  Dunit = g/cm3
  Dvalue = 0.6603
  Group = -> [C_element053,H_element047]
  conduct = 2
  density = 1
  expand = 3
  formula = G4_N-HEXANE
  name = G4_N-HEXANE
  specific = 4
FEATURE [App::DocumentObjectGroupPython] C_element054  label="C_element : 22"  # scripted group (container) (typed FeaturePython)
  n = 22
  ref = C_element
FEATURE [App::DocumentObjectGroupPython] H_element048  label="H_element : 025"  # scripted group (container) (typed FeaturePython)
  n = 10
  ref = H_element
FEATURE [App::DocumentObjectGroupPython] N_element021  label="N_element : 010"  # scripted group (container) (typed FeaturePython)
  n = 2
  ref = N_element
FEATURE [App::DocumentObjectGroupPython] O_element050  label="O_element : 025"  # scripted group (container) (typed FeaturePython)
  n = 5
  ref = O_element
FEATURE [App::DocumentObjectGroupPython] G4_KAPTON  # scripted group (container) (typed FeaturePython)
  Dunit = g/cm3
  Dvalue = 1.42
  Group = -> [C_element054,H_element048,N_element021,O_element050]
  conduct = 2
  density = 1
  expand = 3
  formula = G4_KAPTON
  name = G4_KAPTON
  specific = 4
FEATURE [App::DocumentObjectGroupPython] La_element001  label="La_element : 1"  # scripted group (container) (typed FeaturePython)
  n = 1
  ref = La_element
FEATURE [App::DocumentObjectGroupPython] Br_element003  label="Br_element : 002"  # scripted group (container) (typed FeaturePython)
  n = 1
  ref = Br_element
FEATURE [App::DocumentObjectGroupPython] O_element051  label="O_element : 026"  # scripted group (container) (typed FeaturePython)
  n = 1
  ref = O_element
FEATURE [App::DocumentObjectGroupPython] G4_LANTHANUM_OXYBROMIDE  # scripted group (container) (typed FeaturePython)
  Dunit = g/cm3
  Dvalue = 6.28
  Group = -> [La_element001,Br_element003,O_element051]
  conduct = 2
  density = 1
  expand = 3
  formula = G4_LANTHANUM_OXYBROMIDE
  name = G4_LANTHANUM_OXYBROMIDE
  specific = 4
FEATURE [App::DocumentObjectGroupPython] La_element002  label="La_element : 2"  # scripted group (container) (typed FeaturePython)
  n = 2
  ref = La_element
FEATURE [App::DocumentObjectGroupPython] O_element052  label="O_element : 027"  # scripted group (container) (typed FeaturePython)
  n = 2
  ref = O_element
FEATURE [App::DocumentObjectGroupPython] S_element015  label="S_element : 006"  # scripted group (container) (typed FeaturePython)
  n = 1
  ref = S_element
FEATURE [App::DocumentObjectGroupPython] G4_LANTHANUM_OXYSULFIDE  # scripted group (container) (typed FeaturePython)
  Dunit = g/cm3
  Dvalue = 5.86
  Group = -> [La_element002,O_element052,S_element015]
  conduct = 2
  density = 1
  expand = 3
  formula = G4_LANTHANUM_OXYSULFIDE
  name = G4_LANTHANUM_OXYSULFIDE
  specific = 4
FEATURE [App::DocumentObjectGroupPython] O_element053  label="O_element : 0.072"  # scripted group (container) (typed FeaturePython)
  n = 0.071682
FEATURE [App::DocumentObjectGroupPython] Pb_element002  label="Pb_element : 0.928"  # scripted group (container) (typed FeaturePython)
  n = 0.928318
FEATURE [App::DocumentObjectGroupPython] G4_LEAD_OXIDE  # scripted group (container) (typed FeaturePython)
  Dunit = g/cm3
  Dvalue = 9.53
  Group = -> [O_element053,Pb_element002]
  conduct = 2
  density = 1
  expand = 3
  formula = G4_LEAD_OXIDE
  name = G4_LEAD_OXIDE
  specific = 4
FEATURE [App::DocumentObjectGroupPython] Li_element001  label="Li_element : 1"  # scripted group (container) (typed FeaturePython)
  n = 1
  ref = Li_element
FEATURE [App::DocumentObjectGroupPython] N_element022  label="N_element : 011"  # scripted group (container) (typed FeaturePython)
  n = 1
  ref = N_element
FEATURE [App::DocumentObjectGroupPython] H_element049  label="H_element : 026"  # scripted group (container) (typed FeaturePython)
  n = 2
  ref = H_element
FEATURE [App::DocumentObjectGroupPython] G4_LITHIUM_AMIDE  # scripted group (container) (typed FeaturePython)
  Dunit = g/cm3
  Dvalue = 1.178
  Group = -> [Li_element001,N_element022,H_element049]
  conduct = 2
  density = 1
  expand = 3
  formula = G4_LITHIUM_AMIDE
  name = G4_LITHIUM_AMIDE
  specific = 4
FEATURE [App::DocumentObjectGroupPython] Li_element002  label="Li_element : 2"  # scripted group (container) (typed FeaturePython)
  n = 2
  ref = Li_element
FEATURE [App::DocumentObjectGroupPython] C_element055  label="C_element : 030"  # scripted group (container) (typed FeaturePython)
  n = 1
  ref = C_element
FEATURE [App::DocumentObjectGroupPython] O_element054  label="O_element : 028"  # scripted group (container) (typed FeaturePython)
  n = 3
  ref = O_element
FEATURE [App::DocumentObjectGroupPython] G4_LITHIUM_CARBONATE  # scripted group (container) (typed FeaturePython)
  Dunit = g/cm3
  Dvalue = 2.11
  Group = -> [Li_element002,C_element055,O_element054]
  conduct = 2
  density = 1
  expand = 3
  formula = G4_LITHIUM_CARBONATE
  name = G4_LITHIUM_CARBONATE
  specific = 4
FEATURE [App::DocumentObjectGroupPython] Li_element003  label="Li_element : 003"  # scripted group (container) (typed FeaturePython)
  n = 1
  ref = Li_element
FEATURE [App::DocumentObjectGroupPython] F_element012  label="F_element : 004"  # scripted group (container) (typed FeaturePython)
  n = 1
  ref = F_element
FEATURE [App::DocumentObjectGroupPython] G4_LITHIUM_FLUORIDE  # scripted group (container) (typed FeaturePython)
  Dunit = g/cm3
  Dvalue = 2.635
  Group = -> [Li_element003,F_element012]
  conduct = 2
  density = 1
  expand = 3
  formula = G4_LITHIUM_FLUORIDE
  name = G4_LITHIUM_FLUORIDE
  specific = 4
FEATURE [App::DocumentObjectGroupPython] Li_element004  label="Li_element : 004"  # scripted group (container) (typed FeaturePython)
  n = 1
  ref = Li_element
FEATURE [App::DocumentObjectGroupPython] H_element050  label="H_element : 027"  # scripted group (container) (typed FeaturePython)
  n = 1
  ref = H_element
FEATURE [App::DocumentObjectGroupPython] G4_LITHIUM_HYDRIDE  # scripted group (container) (typed FeaturePython)
  Dunit = g/cm3
  Dvalue = 0.82
  Group = -> [Li_element004,H_element050]
  conduct = 2
  density = 1
  expand = 3
  formula = G4_LITHIUM_HYDRIDE
  name = G4_LITHIUM_HYDRIDE
  specific = 4
FEATURE [App::DocumentObjectGroupPython] Li_element005  label="Li_element : 005"  # scripted group (container) (typed FeaturePython)
  n = 1
  ref = Li_element
FEATURE [App::DocumentObjectGroupPython] I_element003  label="I_element : 002"  # scripted group (container) (typed FeaturePython)
  n = 1
  ref = I_element
FEATURE [App::DocumentObjectGroupPython] G4_LITHIUM_IODIDE  # scripted group (container) (typed FeaturePython)
  Dunit = g/cm3
  Dvalue = 3.494
  Group = -> [Li_element005,I_element003]
  conduct = 2
  density = 1
  expand = 3
  formula = G4_LITHIUM_IODIDE
  name = G4_LITHIUM_IODIDE
  specific = 4
FEATURE [App::DocumentObjectGroupPython] Li_element006  label="Li_element : 006"  # scripted group (container) (typed FeaturePython)
  n = 2
  ref = Li_element
FEATURE [App::DocumentObjectGroupPython] O_element055  label="O_element : 029"  # scripted group (container) (typed FeaturePython)
  n = 1
  ref = O_element
FEATURE [App::DocumentObjectGroupPython] G4_LITHIUM_OXIDE  # scripted group (container) (typed FeaturePython)
  Dunit = g/cm3
  Dvalue = 2.013
  Group = -> [Li_element006,O_element055]
  conduct = 2
  density = 1
  expand = 3
  formula = G4_LITHIUM_OXIDE
  name = G4_LITHIUM_OXIDE
  specific = 4
FEATURE [App::DocumentObjectGroupPython] Li_element007  label="Li_element : 007"  # scripted group (container) (typed FeaturePython)
  n = 2
  ref = Li_element
FEATURE [App::DocumentObjectGroupPython] B_element005  label="B_element : 005"  # scripted group (container) (typed FeaturePython)
  n = 4
  ref = B_element
FEATURE [App::DocumentObjectGroupPython] O_element056  label="O_element : 7"  # scripted group (container) (typed FeaturePython)
  n = 7
  ref = O_element
FEATURE [App::DocumentObjectGroupPython] G4_LITHIUM_TETRABORATE  # scripted group (container) (typed FeaturePython)
  Dunit = g/cm3
  Dvalue = 2.44
  Group = -> [Li_element007,B_element005,O_element056]
  conduct = 2
  density = 1
  expand = 3
  formula = G4_LITHIUM_TETRABORATE
  name = G4_LITHIUM_TETRABORATE
  specific = 4
FEATURE [App::DocumentObjectGroupPython] H_element051  label="H_element : 0.105"  # scripted group (container) (typed FeaturePython)
  n = 0.105
FEATURE [App::DocumentObjectGroupPython] C_element056  label="C_element : 0.083"  # scripted group (container) (typed FeaturePython)
  n = 0.083
FEATURE [App::DocumentObjectGroupPython] N_element023  label="N_element : 0.023"  # scripted group (container) (typed FeaturePython)
  n = 0.023
FEATURE [App::DocumentObjectGroupPython] O_element057  label="O_element : 0.779"  # scripted group (container) (typed FeaturePython)
  n = 0.779
FEATURE [App::DocumentObjectGroupPython] Na_element010  label="Na_element : 0.097"  # scripted group (container) (typed FeaturePython)
  n = 0.002
FEATURE [App::DocumentObjectGroupPython] P_element006  label="P_element : 0.105"  # scripted group (container) (typed FeaturePython)
  n = 0.001
FEATURE [App::DocumentObjectGroupPython] S_element016  label="S_element : 0.017"  # scripted group (container) (typed FeaturePython)
  n = 0.002
FEATURE [App::DocumentObjectGroupPython] Cl_element014  label="Cl_element : 0.587"  # scripted group (container) (typed FeaturePython)
  n = 0.003
FEATURE [App::DocumentObjectGroupPython] K_element005  label="K_element : 0.015"  # scripted group (container) (typed FeaturePython)
  n = 0.002
FEATURE [App::DocumentObjectGroupPython] G4_LUNG_ICRP  # scripted group (container) (typed FeaturePython)
  Dunit = g/cm3
  Dvalue = 1.04
  Group = -> [H_element051,C_element056,N_element023,O_element057,Na_element010,P_element006,S_element016,Cl_element014,K_element005]
  conduct = 2
  density = 1
  expand = 3
  formula = G4_LUNG_ICRP
  name = G4_LUNG_ICRP
  specific = 4
FEATURE [App::DocumentObjectGroupPython] H_element052  label="H_element : 0.116"  # scripted group (container) (typed FeaturePython)
  n = 0.114318
FEATURE [App::DocumentObjectGroupPython] C_element057  label="C_element : 0.656"  # scripted group (container) (typed FeaturePython)
  n = 0.655824
FEATURE [App::DocumentObjectGroupPython] O_element058  label="O_element : 0.092"  # scripted group (container) (typed FeaturePython)
  n = 0.0921831
FEATURE [App::DocumentObjectGroupPython] Mg_element004  label="Mg_element : 0.135"  # scripted group (container) (typed FeaturePython)
  n = 0.134792
FEATURE [App::DocumentObjectGroupPython] Ca_element013  label="Ca_element : 0.003"  # scripted group (container) (typed FeaturePython)
  n = 0.002883
FEATURE [App::DocumentObjectGroupPython] G4_M3_WAX  # scripted group (container) (typed FeaturePython)
  Dunit = g/cm3
  Dvalue = 1.05
  Group = -> [H_element052,C_element057,O_element058,Mg_element004,Ca_element013]
  conduct = 2
  density = 1
  expand = 3
  formula = G4_M3_WAX
  name = G4_M3_WAX
  specific = 4
FEATURE [App::DocumentObjectGroupPython] Mg_element005  label="Mg_element : 1"  # scripted group (container) (typed FeaturePython)
  n = 1
  ref = Mg_element
FEATURE [App::DocumentObjectGroupPython] C_element058  label="C_element : 031"  # scripted group (container) (typed FeaturePython)
  n = 1
  ref = C_element
FEATURE [App::DocumentObjectGroupPython] O_element059  label="O_element : 030"  # scripted group (container) (typed FeaturePython)
  n = 3
  ref = O_element
FEATURE [App::DocumentObjectGroupPython] G4_MAGNESIUM_CARBONATE  # scripted group (container) (typed FeaturePython)
  Dunit = g/cm3
  Dvalue = 2.958
  Group = -> [Mg_element005,C_element058,O_element059]
  conduct = 2
  density = 1
  expand = 3
  formula = G4_MAGNESIUM_CARBONATE
  name = G4_MAGNESIUM_CARBONATE
  specific = 4
FEATURE [App::DocumentObjectGroupPython] Mg_element006  label="Mg_element : 002"  # scripted group (container) (typed FeaturePython)
  n = 1
  ref = Mg_element
FEATURE [App::DocumentObjectGroupPython] F_element013  label="F_element : 005"  # scripted group (container) (typed FeaturePython)
  n = 2
  ref = F_element
FEATURE [App::DocumentObjectGroupPython] G4_MAGNESIUM_FLUORIDE  # scripted group (container) (typed FeaturePython)
  Dunit = g/cm3
  Dvalue = 3
  Group = -> [Mg_element006,F_element013]
  conduct = 2
  density = 1
  expand = 3
  formula = G4_MAGNESIUM_FLUORIDE
  name = G4_MAGNESIUM_FLUORIDE
  specific = 4
FEATURE [App::DocumentObjectGroupPython] Mg_element007  label="Mg_element : 003"  # scripted group (container) (typed FeaturePython)
  n = 1
  ref = Mg_element
FEATURE [App::DocumentObjectGroupPython] O_element060  label="O_element : 031"  # scripted group (container) (typed FeaturePython)
  n = 1
  ref = O_element
FEATURE [App::DocumentObjectGroupPython] G4_MAGNESIUM_OXIDE  # scripted group (container) (typed FeaturePython)
  Dunit = g/cm3
  Dvalue = 3.58
  Group = -> [Mg_element007,O_element060]
  conduct = 2
  density = 1
  expand = 3
  formula = G4_MAGNESIUM_OXIDE
  name = G4_MAGNESIUM_OXIDE
  specific = 4
FEATURE [App::DocumentObjectGroupPython] Mg_element008  label="Mg_element : 004"  # scripted group (container) (typed FeaturePython)
  n = 1
  ref = Mg_element
FEATURE [App::DocumentObjectGroupPython] B_element006  label="B_element : 006"  # scripted group (container) (typed FeaturePython)
  n = 4
  ref = B_element
FEATURE [App::DocumentObjectGroupPython] O_element061  label="O_element : 032"  # scripted group (container) (typed FeaturePython)
  n = 7
  ref = O_element
FEATURE [App::DocumentObjectGroupPython] G4_MAGNESIUM_TETRABORATE  # scripted group (container) (typed FeaturePython)
  Dunit = g/cm3
  Dvalue = 2.53
  Group = -> [Mg_element008,B_element006,O_element061]
  conduct = 2
  density = 1
  expand = 3
  formula = G4_MAGNESIUM_TETRABORATE
  name = G4_MAGNESIUM_TETRABORATE
  specific = 4
FEATURE [App::DocumentObjectGroupPython] Hg_element001  label="Hg_element : 1"  # scripted group (container) (typed FeaturePython)
  n = 1
  ref = Hg_element
FEATURE [App::DocumentObjectGroupPython] I_element004  label="I_element : 2"  # scripted group (container) (typed FeaturePython)
  n = 2
  ref = I_element
FEATURE [App::DocumentObjectGroupPython] G4_MERCURIC_IODIDE  # scripted group (container) (typed FeaturePython)
  Dunit = g/cm3
  Dvalue = 6.36
  Group = -> [Hg_element001,I_element004]
  conduct = 2
  density = 1
  expand = 3
  formula = G4_MERCURIC_IODIDE
  name = G4_MERCURIC_IODIDE
  specific = 4
FEATURE [App::DocumentObjectGroupPython] C_element059  label="C_element : 032"  # scripted group (container) (typed FeaturePython)
  n = 1
  ref = C_element
FEATURE [App::DocumentObjectGroupPython] H_element053  label="H_element : 028"  # scripted group (container) (typed FeaturePython)
  n = 4
  ref = H_element
FEATURE [App::DocumentObjectGroupPython] G4_METHANE  # scripted group (container) (typed FeaturePython)
  Dunit = g/cm3
  Dvalue = 0.000667151
  Group = -> [C_element059,H_element053]
  conduct = 2
  density = 1
  expand = 3
  formula = G4_METHANE
  name = G4_METHANE
  specific = 4
FEATURE [App::DocumentObjectGroupPython] C_element060  label="C_element : 033"  # scripted group (container) (typed FeaturePython)
  n = 1
  ref = C_element
FEATURE [App::DocumentObjectGroupPython] H_element054  label="H_element : 029"  # scripted group (container) (typed FeaturePython)
  n = 4
  ref = H_element
FEATURE [App::DocumentObjectGroupPython] O_element062  label="O_element : 033"  # scripted group (container) (typed FeaturePython)
  n = 1
  ref = O_element
FEATURE [App::DocumentObjectGroupPython] G4_METHANOL  # scripted group (container) (typed FeaturePython)
  Dunit = g/cm3
  Dvalue = 0.7914
  Group = -> [C_element060,H_element054,O_element062]
  conduct = 2
  density = 1
  expand = 3
  formula = G4_METHANOL
  name = G4_METHANOL
  specific = 4
FEATURE [App::DocumentObjectGroupPython] H_element055  label="H_element : 0.134"  # scripted group (container) (typed FeaturePython)
  n = 0.13404
FEATURE [App::DocumentObjectGroupPython] C_element061  label="C_element : 0.778"  # scripted group (container) (typed FeaturePython)
  n = 0.77796
FEATURE [App::DocumentObjectGroupPython] O_element063  label="O_element : 0.035"  # scripted group (container) (typed FeaturePython)
  n = 0.03502
FEATURE [App::DocumentObjectGroupPython] Mg_element009  label="Mg_element : 0.039"  # scripted group (container) (typed FeaturePython)
  n = 0.038594
FEATURE [App::DocumentObjectGroupPython] Ti_element002  label="Ti_element : 0.014"  # scripted group (container) (typed FeaturePython)
  n = 0.014386
FEATURE [App::DocumentObjectGroupPython] G4_MIX_D_WAX  # scripted group (container) (typed FeaturePython)
  Dunit = g/cm3
  Dvalue = 0.99
  Group = -> [H_element055,C_element061,O_element063,Mg_element009,Ti_element002]
  conduct = 2
  density = 1
  expand = 3
  formula = G4_MIX_D_WAX
  name = G4_MIX_D_WAX
  specific = 4
FEATURE [App::DocumentObjectGroupPython] H_element056  label="H_element : 0.135"  # scripted group (container) (typed FeaturePython)
  n = 0.081192
FEATURE [App::DocumentObjectGroupPython] C_element062  label="C_element : 0.583"  # scripted group (container) (typed FeaturePython)
  n = 0.583442
FEATURE [App::DocumentObjectGroupPython] N_element024  label="N_element : 0.018"  # scripted group (container) (typed FeaturePython)
  n = 0.017798
FEATURE [App::DocumentObjectGroupPython] O_element064  label="O_element : 0.186"  # scripted group (container) (typed FeaturePython)
  n = 0.186381
FEATURE [App::DocumentObjectGroupPython] Mg_element010  label="Mg_element : 0.130"  # scripted group (container) (typed FeaturePython)
  n = 0.130287
FEATURE [App::DocumentObjectGroupPython] Cl_element015  label="Cl_element : 0.588"  # scripted group (container) (typed FeaturePython)
  n = 0.0009
FEATURE [App::DocumentObjectGroupPython] G4_MS20_TISSUE  # scripted group (container) (typed FeaturePython)
  Dunit = g/cm3
  Dvalue = 1
  Group = -> [H_element056,C_element062,N_element024,O_element064,Mg_element010,Cl_element015]
  conduct = 2
  density = 1
  expand = 3
  formula = G4_MS20_TISSUE
  name = G4_MS20_TISSUE
  specific = 4
FEATURE [App::DocumentObjectGroupPython] H_element057  label="H_element : 0.136"  # scripted group (container) (typed FeaturePython)
  n = 0.102
FEATURE [App::DocumentObjectGroupPython] C_element063  label="C_element : 0.143"  # scripted group (container) (typed FeaturePython)
  n = 0.143
FEATURE [App::DocumentObjectGroupPython] N_element025  label="N_element : 0.034"  # scripted group (container) (typed FeaturePython)
  n = 0.034
FEATURE [App::DocumentObjectGroupPython] O_element065  label="O_element : 0.710"  # scripted group (container) (typed FeaturePython)
  n = 0.71
FEATURE [App::DocumentObjectGroupPython] Na_element011  label="Na_element : 0.098"  # scripted group (container) (typed FeaturePython)
  n = 0.001
FEATURE [App::DocumentObjectGroupPython] P_element007  label="P_element : 0.002"  # scripted group (container) (typed FeaturePython)
  n = 0.002
FEATURE [App::DocumentObjectGroupPython] S_element017  label="S_element : 0.018"  # scripted group (container) (typed FeaturePython)
  n = 0.003
FEATURE [App::DocumentObjectGroupPython] Cl_element016  label="Cl_element : 0.589"  # scripted group (container) (typed FeaturePython)
  n = 0.001
FEATURE [App::DocumentObjectGroupPython] K_element006  label="K_element : 0.004"  # scripted group (container) (typed FeaturePython)
  n = 0.004
FEATURE [App::DocumentObjectGroupPython] G4_MUSCLE_SKELETAL_ICRP  # scripted group (container) (typed FeaturePython)
  Dunit = g/cm3
  Dvalue = 1.05
  Group = -> [H_element057,C_element063,N_element025,O_element065,Na_element011,P_element007,S_element017,Cl_element016,K_element006]
  conduct = 2
  density = 1
  expand = 3
  formula = G4_MUSCLE_SKELETAL_ICRP
  name = G4_MUSCLE_SKELETAL_ICRP
  specific = 4
FEATURE [App::DocumentObjectGroupPython] H_element058  label="H_element : 0.137"  # scripted group (container) (typed FeaturePython)
  n = 0.102102
FEATURE [App::DocumentObjectGroupPython] C_element064  label="C_element : 0.123"  # scripted group (container) (typed FeaturePython)
  n = 0.123123
FEATURE [App::DocumentObjectGroupPython] N_element026  label="N_element : 0.756"  # scripted group (container) (typed FeaturePython)
  n = 0.035035
FEATURE [App::DocumentObjectGroupPython] O_element066  label="O_element : 0.730"  # scripted group (container) (typed FeaturePython)
  n = 0.72973
FEATURE [App::DocumentObjectGroupPython] Na_element012  label="Na_element : 0.099"  # scripted group (container) (typed FeaturePython)
  n = 0.001001
FEATURE [App::DocumentObjectGroupPython] P_element008  label="P_element : 0.106"  # scripted group (container) (typed FeaturePython)
  n = 0.002002
FEATURE [App::DocumentObjectGroupPython] S_element018  label="S_element : 0.019"  # scripted group (container) (typed FeaturePython)
  n = 0.004004
FEATURE [App::DocumentObjectGroupPython] K_element007  label="K_element : 0.016"  # scripted group (container) (typed FeaturePython)
  n = 0.003003
FEATURE [App::DocumentObjectGroupPython] G4_MUSCLE_STRIATED_ICRU  # scripted group (container) (typed FeaturePython)
  Dunit = g/cm3
  Dvalue = 1.04
  Group = -> [H_element058,C_element064,N_element026,O_element066,Na_element012,P_element008,S_element018,K_element007]
  conduct = 2
  density = 1
  expand = 3
  formula = G4_MUSCLE_STRIATED_ICRU
  name = G4_MUSCLE_STRIATED_ICRU
  specific = 4
FEATURE [App::DocumentObjectGroupPython] H_element059  label="H_element : 0.098"  # scripted group (container) (typed FeaturePython)
  n = 0.0982341
FEATURE [App::DocumentObjectGroupPython] C_element065  label="C_element : 0.156"  # scripted group (container) (typed FeaturePython)
  n = 0.156214
FEATURE [App::DocumentObjectGroupPython] N_element027  label="N_element : 0.757"  # scripted group (container) (typed FeaturePython)
  n = 0.035451
FEATURE [App::DocumentObjectGroupPython] O_element067  label="O_element : 0.880"  # scripted group (container) (typed FeaturePython)
  n = 0.710101
FEATURE [App::DocumentObjectGroupPython] G4_MUSCLE_WITH_SUCROSE  # scripted group (container) (typed FeaturePython)
  Dunit = g/cm3
  Dvalue = 1.11
  Group = -> [H_element059,C_element065,N_element027,O_element067]
  conduct = 2
  density = 1
  expand = 3
  formula = G4_MUSCLE_WITH_SUCROSE
  name = G4_MUSCLE_WITH_SUCROSE
  specific = 4
FEATURE [App::DocumentObjectGroupPython] H_element060  label="H_element : 0.138"  # scripted group (container) (typed FeaturePython)
  n = 0.101969
FEATURE [App::DocumentObjectGroupPython] C_element066  label="C_element : 0.120"  # scripted group (container) (typed FeaturePython)
  n = 0.120058
FEATURE [App::DocumentObjectGroupPython] N_element028  label="N_element : 0.758"  # scripted group (container) (typed FeaturePython)
  n = 0.035451
FEATURE [App::DocumentObjectGroupPython] O_element068  label="O_element : 0.743"  # scripted group (container) (typed FeaturePython)
  n = 0.742522
FEATURE [App::DocumentObjectGroupPython] G4_MUSCLE_WITHOUT_SUCROSE  # scripted group (container) (typed FeaturePython)
  Dunit = g/cm3
  Dvalue = 1.07
  Group = -> [H_element060,C_element066,N_element028,O_element068]
  conduct = 2
  density = 1
  expand = 3
  formula = G4_MUSCLE_WITHOUT_SUCROSE
  name = G4_MUSCLE_WITHOUT_SUCROSE
  specific = 4
FEATURE [App::DocumentObjectGroupPython] C_element067  label="C_element : 10"  # scripted group (container) (typed FeaturePython)
  n = 10
  ref = C_element
FEATURE [App::DocumentObjectGroupPython] H_element061  label="H_element : 030"  # scripted group (container) (typed FeaturePython)
  n = 8
  ref = H_element
FEATURE [App::DocumentObjectGroupPython] G4_NAPHTHALENE  # scripted group (container) (typed FeaturePython)
  Dunit = g/cm3
  Dvalue = 1.145
  Group = -> [C_element067,H_element061]
  conduct = 2
  density = 1
  expand = 3
  formula = G4_NAPHTHALENE
  name = G4_NAPHTHALENE
  specific = 4
FEATURE [App::DocumentObjectGroupPython] C_element068  label="C_element : 034"  # scripted group (container) (typed FeaturePython)
  n = 6
  ref = C_element
FEATURE [App::DocumentObjectGroupPython] H_element062  label="H_element : 031"  # scripted group (container) (typed FeaturePython)
  n = 5
  ref = H_element
FEATURE [App::DocumentObjectGroupPython] N_element029  label="N_element : 012"  # scripted group (container) (typed FeaturePython)
  n = 1
  ref = N_element
FEATURE [App::DocumentObjectGroupPython] O_element069  label="O_element : 034"  # scripted group (container) (typed FeaturePython)
  n = 2
  ref = O_element
FEATURE [App::DocumentObjectGroupPython] G4_NITROBENZENE  # scripted group (container) (typed FeaturePython)
  Dunit = g/cm3
  Dvalue = 1.19867
  Group = -> [C_element068,H_element062,N_element029,O_element069]
  conduct = 2
  density = 1
  expand = 3
  formula = G4_NITROBENZENE
  name = G4_NITROBENZENE
  specific = 4
FEATURE [App::DocumentObjectGroupPython] N_element030  label="N_element : 013"  # scripted group (container) (typed FeaturePython)
  n = 2
  ref = N_element
FEATURE [App::DocumentObjectGroupPython] O_element070  label="O_element : 035"  # scripted group (container) (typed FeaturePython)
  n = 1
  ref = O_element
FEATURE [App::DocumentObjectGroupPython] G4_NITROUS_OXIDE  # scripted group (container) (typed FeaturePython)
  Dunit = g/cm3
  Dvalue = 0.00183094
  Group = -> [N_element030,O_element070]
  conduct = 2
  density = 1
  expand = 3
  formula = G4_NITROUS_OXIDE
  name = G4_NITROUS_OXIDE
  specific = 4
FEATURE [App::DocumentObjectGroupPython] H_element063  label="H_element : 0.104"  # scripted group (container) (typed FeaturePython)
  n = 0.103509
FEATURE [App::DocumentObjectGroupPython] C_element069  label="C_element : 0.648"  # scripted group (container) (typed FeaturePython)
  n = 0.648416
FEATURE [App::DocumentObjectGroupPython] N_element031  label="N_element : 0.100"  # scripted group (container) (typed FeaturePython)
  n = 0.0995361
FEATURE [App::DocumentObjectGroupPython] O_element071  label="O_element : 0.149"  # scripted group (container) (typed FeaturePython)
  n = 0.148539
FEATURE [App::DocumentObjectGroupPython] G4_NYLON_8062  label="G4_NYLON-8062"  # scripted group (container) (typed FeaturePython)
  Dunit = g/cm3
  Dvalue = 1.08
  Group = -> [H_element063,C_element069,N_element031,O_element071]
  conduct = 2
  density = 1
  expand = 3
  formula = G4_NYLON-8062
  name = G4_NYLON-8062
  specific = 4
FEATURE [App::DocumentObjectGroupPython] C_element070  label="C_element : 035"  # scripted group (container) (typed FeaturePython)
  n = 6
  ref = C_element
FEATURE [App::DocumentObjectGroupPython] H_element064  label="H_element : 11"  # scripted group (container) (typed FeaturePython)
  n = 11
  ref = H_element
FEATURE [App::DocumentObjectGroupPython] N_element032  label="N_element : 014"  # scripted group (container) (typed FeaturePython)
  n = 1
  ref = N_element
FEATURE [App::DocumentObjectGroupPython] O_element072  label="O_element : 036"  # scripted group (container) (typed FeaturePython)
  n = 1
  ref = O_element
FEATURE [App::DocumentObjectGroupPython] G4_NYLON_6_6  label="G4_NYLON-6-6"  # scripted group (container) (typed FeaturePython)
  Dunit = g/cm3
  Dvalue = 1.14
  Group = -> [C_element070,H_element064,N_element032,O_element072]
  conduct = 2
  density = 1
  expand = 3
  formula = G4_NYLON-6-6
  name = G4_NYLON-6-6
  specific = 4
FEATURE [App::DocumentObjectGroupPython] H_element065  label="H_element : 0.139"  # scripted group (container) (typed FeaturePython)
  n = 0.107062
FEATURE [App::DocumentObjectGroupPython] C_element071  label="C_element : 0.680"  # scripted group (container) (typed FeaturePython)
  n = 0.680449
FEATURE [App::DocumentObjectGroupPython] N_element033  label="N_element : 0.099"  # scripted group (container) (typed FeaturePython)
  n = 0.099189
FEATURE [App::DocumentObjectGroupPython] O_element073  label="O_element : 0.113"  # scripted group (container) (typed FeaturePython)
  n = 0.1133
FEATURE [App::DocumentObjectGroupPython] G4_NYLON_6_10  label="G4_NYLON-6-10"  # scripted group (container) (typed FeaturePython)
  Dunit = g/cm3
  Dvalue = 1.14
  Group = -> [H_element065,C_element071,N_element033,O_element073]
  conduct = 2
  density = 1
  expand = 3
  formula = G4_NYLON-6-10
  name = G4_NYLON-6-10
  specific = 4
FEATURE [App::DocumentObjectGroupPython] H_element066  label="H_element : 0.140"  # scripted group (container) (typed FeaturePython)
  n = 0.115476
FEATURE [App::DocumentObjectGroupPython] C_element072  label="C_element : 0.721"  # scripted group (container) (typed FeaturePython)
  n = 0.720818
FEATURE [App::DocumentObjectGroupPython] N_element034  label="N_element : 0.076"  # scripted group (container) (typed FeaturePython)
  n = 0.0764169
FEATURE [App::DocumentObjectGroupPython] O_element074  label="O_element : 0.087"  # scripted group (container) (typed FeaturePython)
  n = 0.0872889
FEATURE [App::DocumentObjectGroupPython] G4_NYLON_11_RILSAN  label="G4_NYLON-11_RILSAN"  # scripted group (container) (typed FeaturePython)
  Dunit = g/cm3
  Dvalue = 1.425
  Group = -> [H_element066,C_element072,N_element034,O_element074]
  conduct = 2
  density = 1
  expand = 3
  formula = G4_NYLON-11_RILSAN
  name = G4_NYLON-11_RILSAN
  specific = 4
FEATURE [App::DocumentObjectGroupPython] C_element073  label="C_element : 8"  # scripted group (container) (typed FeaturePython)
  n = 8
  ref = C_element
FEATURE [App::DocumentObjectGroupPython] H_element067  label="H_element : 18"  # scripted group (container) (typed FeaturePython)
  n = 18
  ref = H_element
FEATURE [App::DocumentObjectGroupPython] G4_OCTANE  # scripted group (container) (typed FeaturePython)
  Dunit = g/cm3
  Dvalue = 0.7026
  Group = -> [C_element073,H_element067]
  conduct = 2
  density = 1
  expand = 3
  formula = G4_OCTANE
  name = G4_OCTANE
  specific = 4
FEATURE [App::DocumentObjectGroupPython] C_element074  label="C_element : 25"  # scripted group (container) (typed FeaturePython)
  n = 25
  ref = C_element
FEATURE [App::DocumentObjectGroupPython] H_element068  label="H_element : 52"  # scripted group (container) (typed FeaturePython)
  n = 52
  ref = H_element
FEATURE [App::DocumentObjectGroupPython] G4_PARAFFIN  # scripted group (container) (typed FeaturePython)
  Dunit = g/cm3
  Dvalue = 0.93
  Group = -> [C_element074,H_element068]
  conduct = 2
  density = 1
  expand = 3
  formula = G4_PARAFFIN
  name = G4_PARAFFIN
  specific = 4
FEATURE [App::DocumentObjectGroupPython] C_element075  label="C_element : 036"  # scripted group (container) (typed FeaturePython)
  n = 5
  ref = C_element
FEATURE [App::DocumentObjectGroupPython] H_element069  label="H_element : 032"  # scripted group (container) (typed FeaturePython)
  n = 12
  ref = H_element
FEATURE [App::DocumentObjectGroupPython] G4_N_PENTANE  label="G4_N-PENTANE"  # scripted group (container) (typed FeaturePython)
  Dunit = g/cm3
  Dvalue = 0.6262
  Group = -> [C_element075,H_element069]
  conduct = 2
  density = 1
  expand = 3
  formula = G4_N-PENTANE
  name = G4_N-PENTANE
  specific = 4
FEATURE [App::DocumentObjectGroupPython] H_element070  label="H_element : 0.014"  # scripted group (container) (typed FeaturePython)
  n = 0.0141
FEATURE [App::DocumentObjectGroupPython] C_element076  label="C_element : 0.072"  # scripted group (container) (typed FeaturePython)
  n = 0.072261
FEATURE [App::DocumentObjectGroupPython] N_element035  label="N_element : 0.019"  # scripted group (container) (typed FeaturePython)
  n = 0.01932
FEATURE [App::DocumentObjectGroupPython] O_element075  label="O_element : 0.066"  # scripted group (container) (typed FeaturePython)
  n = 0.066101
FEATURE [App::DocumentObjectGroupPython] S_element019  label="S_element : 0.020"  # scripted group (container) (typed FeaturePython)
  n = 0.00189
FEATURE [App::DocumentObjectGroupPython] Br_element004  label="Br_element : 0.349"  # scripted group (container) (typed FeaturePython)
  n = 0.349103
FEATURE [App::DocumentObjectGroupPython] Ag_element001  label="Ag_element : 0.474"  # scripted group (container) (typed FeaturePython)
  n = 0.474105
FEATURE [App::DocumentObjectGroupPython] I_element005  label="I_element : 0.003"  # scripted group (container) (typed FeaturePython)
  n = 0.00312
FEATURE [App::DocumentObjectGroupPython] G4_PHOTO_EMULSION  # scripted group (container) (typed FeaturePython)
  Dunit = g/cm3
  Dvalue = 3.815
  Group = -> [H_element070,C_element076,N_element035,O_element075,S_element019,Br_element004,Ag_element001,I_element005]
  conduct = 2
  density = 1
  expand = 3
  formula = G4_PHOTO_EMULSION
  name = G4_PHOTO_EMULSION
  specific = 4
FEATURE [App::DocumentObjectGroupPython] C_element077  label="C_element : 9"  # scripted group (container) (typed FeaturePython)
  n = 9
  ref = C_element
FEATURE [App::DocumentObjectGroupPython] H_element071  label="H_element : 033"  # scripted group (container) (typed FeaturePython)
  n = 10
  ref = H_element
FEATURE [App::DocumentObjectGroupPython] G4_PLASTIC_SC_VINYLTOLUENE  # scripted group (container) (typed FeaturePython)
  Dunit = g/cm3
  Dvalue = 1.032
  Group = -> [C_element077,H_element071]
  conduct = 2
  density = 1
  expand = 3
  formula = G4_PLASTIC_SC_VINYLTOLUENE
  name = G4_PLASTIC_SC_VINYLTOLUENE
  specific = 4
FEATURE [App::DocumentObjectGroupPython] Pu_element001  label="Pu_element : 1"  # scripted group (container) (typed FeaturePython)
  n = 1
  ref = Pu_element
FEATURE [App::DocumentObjectGroupPython] O_element076  label="O_element : 037"  # scripted group (container) (typed FeaturePython)
  n = 2
  ref = O_element
FEATURE [App::DocumentObjectGroupPython] G4_PLUTONIUM_DIOXIDE  # scripted group (container) (typed FeaturePython)
  Dunit = g/cm3
  Dvalue = 11.46
  Group = -> [Pu_element001,O_element076]
  conduct = 2
  density = 1
  expand = 3
  formula = G4_PLUTONIUM_DIOXIDE
  name = G4_PLUTONIUM_DIOXIDE
  specific = 4
FEATURE [App::DocumentObjectGroupPython] C_element078  label="C_element : 037"  # scripted group (container) (typed FeaturePython)
  n = 3
  ref = C_element
FEATURE [App::DocumentObjectGroupPython] H_element072  label="H_element : 034"  # scripted group (container) (typed FeaturePython)
  n = 3
  ref = H_element
FEATURE [App::DocumentObjectGroupPython] N_element036  label="N_element : 015"  # scripted group (container) (typed FeaturePython)
  n = 1
  ref = N_element
FEATURE [App::DocumentObjectGroupPython] G4_POLYACRYLONITRILE  # scripted group (container) (typed FeaturePython)
  Dunit = g/cm3
  Dvalue = 1.17
  Group = -> [C_element078,H_element072,N_element036]
  conduct = 2
  density = 1
  expand = 3
  formula = G4_POLYACRYLONITRILE
  name = G4_POLYACRYLONITRILE
  specific = 4
FEATURE [App::DocumentObjectGroupPython] C_element079  label="C_element : 16"  # scripted group (container) (typed FeaturePython)
  n = 16
  ref = C_element
FEATURE [App::DocumentObjectGroupPython] H_element073  label="H_element : 035"  # scripted group (container) (typed FeaturePython)
  n = 14
  ref = H_element
FEATURE [App::DocumentObjectGroupPython] O_element077  label="O_element : 038"  # scripted group (container) (typed FeaturePython)
  n = 3
  ref = O_element
FEATURE [App::DocumentObjectGroupPython] G4_POLYCARBONATE  # scripted group (container) (typed FeaturePython)
  Dunit = g/cm3
  Dvalue = 1.2
  Group = -> [C_element079,H_element073,O_element077]
  conduct = 2
  density = 1
  expand = 3
  formula = G4_POLYCARBONATE
  name = G4_POLYCARBONATE
  specific = 4
FEATURE [App::DocumentObjectGroupPython] C_element080  label="C_element : 038"  # scripted group (container) (typed FeaturePython)
  n = 8
  ref = C_element
FEATURE [App::DocumentObjectGroupPython] H_element074  label="H_element : 036"  # scripted group (container) (typed FeaturePython)
  n = 7
  ref = H_element
FEATURE [App::DocumentObjectGroupPython] Cl_element017  label="Cl_element : 007"  # scripted group (container) (typed FeaturePython)
  n = 1
  ref = Cl_element
FEATURE [App::DocumentObjectGroupPython] G4_POLYCHLOROSTYRENE  # scripted group (container) (typed FeaturePython)
  Dunit = g/cm3
  Dvalue = 1.3
  Group = -> [C_element080,H_element074,Cl_element017]
  conduct = 2
  density = 1
  expand = 3
  formula = G4_POLYCHLOROSTYRENE
  name = G4_POLYCHLOROSTYRENE
  specific = 4
FEATURE [App::DocumentObjectGroupPython] C_element081  label="C_element : 039"  # scripted group (container) (typed FeaturePython)
  n = 1
  ref = C_element
FEATURE [App::DocumentObjectGroupPython] H_element075  label="H_element : 037"  # scripted group (container) (typed FeaturePython)
  n = 2
  ref = H_element
FEATURE [App::DocumentObjectGroupPython] G4_POLYETHYLENE  # scripted group (container) (typed FeaturePython)
  Dunit = g/cm3
  Dvalue = 0.94
  Group = -> [C_element081,H_element075]
  conduct = 2
  density = 1
  expand = 3
  formula = G4_POLYETHYLENE
  name = G4_POLYETHYLENE
  specific = 4
FEATURE [App::DocumentObjectGroupPython] C_element082  label="C_element : 040"  # scripted group (container) (typed FeaturePython)
  n = 10
  ref = C_element
FEATURE [App::DocumentObjectGroupPython] H_element076  label="H_element : 038"  # scripted group (container) (typed FeaturePython)
  n = 8
  ref = H_element
FEATURE [App::DocumentObjectGroupPython] O_element078  label="O_element : 039"  # scripted group (container) (typed FeaturePython)
  n = 4
  ref = O_element
FEATURE [App::DocumentObjectGroupPython] G4_MYLAR  # scripted group (container) (typed FeaturePython)
  Dunit = g/cm3
  Dvalue = 1.4
  Group = -> [C_element082,H_element076,O_element078]
  conduct = 2
  density = 1
  expand = 3
  formula = G4_MYLAR
  name = G4_MYLAR
  specific = 4
FEATURE [App::DocumentObjectGroupPython] C_element083  label="C_element : 041"  # scripted group (container) (typed FeaturePython)
  n = 5
  ref = C_element
FEATURE [App::DocumentObjectGroupPython] H_element077  label="H_element : 039"  # scripted group (container) (typed FeaturePython)
  n = 8
  ref = H_element
FEATURE [App::DocumentObjectGroupPython] O_element079  label="O_element : 040"  # scripted group (container) (typed FeaturePython)
  n = 2
  ref = O_element
FEATURE [App::DocumentObjectGroupPython] G4_PLEXIGLASS  # scripted group (container) (typed FeaturePython)
  Dunit = g/cm3
  Dvalue = 1.19
  Group = -> [C_element083,H_element077,O_element079]
  conduct = 2
  density = 1
  expand = 3
  formula = G4_PLEXIGLASS
  name = G4_PLEXIGLASS
  specific = 4
FEATURE [App::DocumentObjectGroupPython] C_element084  label="C_element : 042"  # scripted group (container) (typed FeaturePython)
  n = 1
  ref = C_element
FEATURE [App::DocumentObjectGroupPython] H_element078  label="H_element : 040"  # scripted group (container) (typed FeaturePython)
  n = 2
  ref = H_element
FEATURE [App::DocumentObjectGroupPython] O_element080  label="O_element : 041"  # scripted group (container) (typed FeaturePython)
  n = 1
  ref = O_element
FEATURE [App::DocumentObjectGroupPython] G4_POLYOXYMETHYLENE  # scripted group (container) (typed FeaturePython)
  Dunit = g/cm3
  Dvalue = 1.425
  Group = -> [C_element084,H_element078,O_element080]
  conduct = 2
  density = 1
  expand = 3
  formula = G4_POLYOXYMETHYLENE
  name = G4_POLYOXYMETHYLENE
  specific = 4
FEATURE [App::DocumentObjectGroupPython] C_element085  label="C_element : 043"  # scripted group (container) (typed FeaturePython)
  n = 2
  ref = C_element
FEATURE [App::DocumentObjectGroupPython] H_element079  label="H_element : 041"  # scripted group (container) (typed FeaturePython)
  n = 4
  ref = H_element
FEATURE [App::DocumentObjectGroupPython] G4_POLYPROPYLENE  # scripted group (container) (typed FeaturePython)
  Dunit = g/cm3
  Dvalue = 0.9
  Group = -> [C_element085,H_element079]
  conduct = 2
  density = 1
  expand = 3
  formula = G4_POLYPROPYLENE
  name = G4_POLYPROPYLENE
  specific = 4
FEATURE [App::DocumentObjectGroupPython] C_element086  label="C_element : 044"  # scripted group (container) (typed FeaturePython)
  n = 8
  ref = C_element
FEATURE [App::DocumentObjectGroupPython] H_element080  label="H_element : 042"  # scripted group (container) (typed FeaturePython)
  n = 8
  ref = H_element
FEATURE [App::DocumentObjectGroupPython] G4_POLYSTYRENE  # scripted group (container) (typed FeaturePython)
  Dunit = g/cm3
  Dvalue = 1.06
  Group = -> [C_element086,H_element080]
  conduct = 2
  density = 1
  expand = 3
  formula = G4_POLYSTYRENE
  name = G4_POLYSTYRENE
  specific = 4
FEATURE [App::DocumentObjectGroupPython] C_element087  label="C_element : 045"  # scripted group (container) (typed FeaturePython)
  n = 2
  ref = C_element
FEATURE [App::DocumentObjectGroupPython] F_element014  label="F_element : 4"  # scripted group (container) (typed FeaturePython)
  n = 4
  ref = F_element
FEATURE [App::DocumentObjectGroupPython] G4_TEFLON  # scripted group (container) (typed FeaturePython)
  Dunit = g/cm3
  Dvalue = 2.2
  Group = -> [C_element087,F_element014]
  conduct = 2
  density = 1
  expand = 3
  formula = G4_TEFLON
  name = G4_TEFLON
  specific = 4
FEATURE [App::DocumentObjectGroupPython] C_element088  label="C_element : 046"  # scripted group (container) (typed FeaturePython)
  n = 2
  ref = C_element
FEATURE [App::DocumentObjectGroupPython] F_element015  label="F_element : 006"  # scripted group (container) (typed FeaturePython)
  n = 3
  ref = F_element
FEATURE [App::DocumentObjectGroupPython] Cl_element018  label="Cl_element : 008"  # scripted group (container) (typed FeaturePython)
  n = 1
  ref = Cl_element
FEATURE [App::DocumentObjectGroupPython] G4_POLYTRIFLUOROCHLOROETHYLENE  # scripted group (container) (typed FeaturePython)
  Dunit = g/cm3
  Dvalue = 2.1
  Group = -> [C_element088,F_element015,Cl_element018]
  conduct = 2
  density = 1
  expand = 3
  formula = G4_POLYTRIFLUOROCHLOROETHYLENE
  name = G4_POLYTRIFLUOROCHLOROETHYLENE
  specific = 4
FEATURE [App::DocumentObjectGroupPython] C_element089  label="C_element : 047"  # scripted group (container) (typed FeaturePython)
  n = 4
  ref = C_element
FEATURE [App::DocumentObjectGroupPython] H_element081  label="H_element : 043"  # scripted group (container) (typed FeaturePython)
  n = 6
  ref = H_element
FEATURE [App::DocumentObjectGroupPython] O_element081  label="O_element : 042"  # scripted group (container) (typed FeaturePython)
  n = 2
  ref = O_element
FEATURE [App::DocumentObjectGroupPython] G4_POLYVINYL_ACETATE  # scripted group (container) (typed FeaturePython)
  Dunit = g/cm3
  Dvalue = 1.19
  Group = -> [C_element089,H_element081,O_element081]
  conduct = 2
  density = 1
  expand = 3
  formula = G4_POLYVINYL_ACETATE
  name = G4_POLYVINYL_ACETATE
  specific = 4
FEATURE [App::DocumentObjectGroupPython] C_element090  label="C_element : 048"  # scripted group (container) (typed FeaturePython)
  n = 2
  ref = C_element
FEATURE [App::DocumentObjectGroupPython] H_element082  label="H_element : 044"  # scripted group (container) (typed FeaturePython)
  n = 4
  ref = H_element
FEATURE [App::DocumentObjectGroupPython] O_element082  label="O_element : 043"  # scripted group (container) (typed FeaturePython)
  n = 1
  ref = O_element
FEATURE [App::DocumentObjectGroupPython] G4_POLYVINYL_ALCOHOL  # scripted group (container) (typed FeaturePython)
  Dunit = g/cm3
  Dvalue = 1.3
  Group = -> [C_element090,H_element082,O_element082]
  conduct = 2
  density = 1
  expand = 3
  formula = G4_POLYVINYL_ALCOHOL
  name = G4_POLYVINYL_ALCOHOL
  specific = 4
FEATURE [App::DocumentObjectGroupPython] C_element091  label="C_element : 049"  # scripted group (container) (typed FeaturePython)
  n = 8
  ref = C_element
FEATURE [App::DocumentObjectGroupPython] H_element083  label="H_element : 045"  # scripted group (container) (typed FeaturePython)
  n = 14
  ref = H_element
FEATURE [App::DocumentObjectGroupPython] O_element083  label="O_element : 044"  # scripted group (container) (typed FeaturePython)
  n = 2
  ref = O_element
FEATURE [App::DocumentObjectGroupPython] G4_POLYVINYL_BUTYRAL  # scripted group (container) (typed FeaturePython)
  Dunit = g/cm3
  Dvalue = 1.12
  Group = -> [C_element091,H_element083,O_element083]
  conduct = 2
  density = 1
  expand = 3
  formula = G4_POLYVINYL_BUTYRAL
  name = G4_POLYVINYL_BUTYRAL
  specific = 4
FEATURE [App::DocumentObjectGroupPython] C_element092  label="C_element : 050"  # scripted group (container) (typed FeaturePython)
  n = 2
  ref = C_element
FEATURE [App::DocumentObjectGroupPython] H_element084  label="H_element : 046"  # scripted group (container) (typed FeaturePython)
  n = 3
  ref = H_element
FEATURE [App::DocumentObjectGroupPython] Cl_element019  label="Cl_element : 009"  # scripted group (container) (typed FeaturePython)
  n = 1
  ref = Cl_element
FEATURE [App::DocumentObjectGroupPython] G4_POLYVINYL_CHLORIDE  # scripted group (container) (typed FeaturePython)
  Dunit = g/cm3
  Dvalue = 1.3
  Group = -> [C_element092,H_element084,Cl_element019]
  conduct = 2
  density = 1
  expand = 3
  formula = G4_POLYVINYL_CHLORIDE
  name = G4_POLYVINYL_CHLORIDE
  specific = 4
FEATURE [App::DocumentObjectGroupPython] C_element093  label="C_element : 051"  # scripted group (container) (typed FeaturePython)
  n = 2
  ref = C_element
FEATURE [App::DocumentObjectGroupPython] H_element085  label="H_element : 047"  # scripted group (container) (typed FeaturePython)
  n = 2
  ref = H_element
FEATURE [App::DocumentObjectGroupPython] Cl_element020  label="Cl_element : 010"  # scripted group (container) (typed FeaturePython)
  n = 2
  ref = Cl_element
FEATURE [App::DocumentObjectGroupPython] G4_POLYVINYLIDENE_CHLORIDE  # scripted group (container) (typed FeaturePython)
  Dunit = g/cm3
  Dvalue = 1.7
  Group = -> [C_element093,H_element085,Cl_element020]
  conduct = 2
  density = 1
  expand = 3
  formula = G4_POLYVINYLIDENE_CHLORIDE
  name = G4_POLYVINYLIDENE_CHLORIDE
  specific = 4
FEATURE [App::DocumentObjectGroupPython] C_element094  label="C_element : 052"  # scripted group (container) (typed FeaturePython)
  n = 2
  ref = C_element
FEATURE [App::DocumentObjectGroupPython] H_element086  label="H_element : 048"  # scripted group (container) (typed FeaturePython)
  n = 2
  ref = H_element
FEATURE [App::DocumentObjectGroupPython] F_element016  label="F_element : 007"  # scripted group (container) (typed FeaturePython)
  n = 2
  ref = F_element
FEATURE [App::DocumentObjectGroupPython] G4_POLYVINYLIDENE_FLUORIDE  # scripted group (container) (typed FeaturePython)
  Dunit = g/cm3
  Dvalue = 1.76
  Group = -> [C_element094,H_element086,F_element016]
  conduct = 2
  density = 1
  expand = 3
  formula = G4_POLYVINYLIDENE_FLUORIDE
  name = G4_POLYVINYLIDENE_FLUORIDE
  specific = 4
FEATURE [App::DocumentObjectGroupPython] C_element095  label="C_element : 053"  # scripted group (container) (typed FeaturePython)
  n = 6
  ref = C_element
FEATURE [App::DocumentObjectGroupPython] H_element087  label="H_element : 9"  # scripted group (container) (typed FeaturePython)
  n = 9
  ref = H_element
FEATURE [App::DocumentObjectGroupPython] N_element037  label="N_element : 016"  # scripted group (container) (typed FeaturePython)
  n = 1
  ref = N_element
FEATURE [App::DocumentObjectGroupPython] O_element084  label="O_element : 045"  # scripted group (container) (typed FeaturePython)
  n = 1
  ref = O_element
FEATURE [App::DocumentObjectGroupPython] G4_POLYVINYL_PYRROLIDONE  # scripted group (container) (typed FeaturePython)
  Dunit = g/cm3
  Dvalue = 1.25
  Group = -> [C_element095,H_element087,N_element037,O_element084]
  conduct = 2
  density = 1
  expand = 3
  formula = G4_POLYVINYL_PYRROLIDONE
  name = G4_POLYVINYL_PYRROLIDONE
  specific = 4
FEATURE [App::DocumentObjectGroupPython] K_element008  label="K_element : 1"  # scripted group (container) (typed FeaturePython)
  n = 1
  ref = K_element
FEATURE [App::DocumentObjectGroupPython] I_element006  label="I_element : 003"  # scripted group (container) (typed FeaturePython)
  n = 1
  ref = I_element
FEATURE [App::DocumentObjectGroupPython] G4_POTASSIUM_IODIDE  # scripted group (container) (typed FeaturePython)
  Dunit = g/cm3
  Dvalue = 3.13
  Group = -> [K_element008,I_element006]
  conduct = 2
  density = 1
  expand = 3
  formula = G4_POTASSIUM_IODIDE
  name = G4_POTASSIUM_IODIDE
  specific = 4
FEATURE [App::DocumentObjectGroupPython] K_element009  label="K_element : 2"  # scripted group (container) (typed FeaturePython)
  n = 2
  ref = K_element
FEATURE [App::DocumentObjectGroupPython] O_element085  label="O_element : 046"  # scripted group (container) (typed FeaturePython)
  n = 1
  ref = O_element
FEATURE [App::DocumentObjectGroupPython] G4_POTASSIUM_OXIDE  # scripted group (container) (typed FeaturePython)
  Dunit = g/cm3
  Dvalue = 2.32
  Group = -> [K_element009,O_element085]
  conduct = 2
  density = 1
  expand = 3
  formula = G4_POTASSIUM_OXIDE
  name = G4_POTASSIUM_OXIDE
  specific = 4
FEATURE [App::DocumentObjectGroupPython] C_element096  label="C_element : 054"  # scripted group (container) (typed FeaturePython)
  n = 3
  ref = C_element
FEATURE [App::DocumentObjectGroupPython] H_element088  label="H_element : 049"  # scripted group (container) (typed FeaturePython)
  n = 8
  ref = H_element
FEATURE [App::DocumentObjectGroupPython] G4_PROPANE  # scripted group (container) (typed FeaturePython)
  Dunit = g/cm3
  Dvalue = 0.00187939
  Group = -> [C_element096,H_element088]
  conduct = 2
  density = 1
  expand = 3
  formula = G4_PROPANE
  name = G4_PROPANE
  specific = 4
FEATURE [App::DocumentObjectGroupPython] C_element097  label="C_element : 055"  # scripted group (container) (typed FeaturePython)
  n = 3
  ref = C_element
FEATURE [App::DocumentObjectGroupPython] H_element089  label="H_element : 050"  # scripted group (container) (typed FeaturePython)
  n = 8
  ref = H_element
FEATURE [App::DocumentObjectGroupPython] G4_lPROPANE  # scripted group (container) (typed FeaturePython)
  Dunit = g/cm3
  Dvalue = 0.43
  Group = -> [C_element097,H_element089]
  conduct = 2
  density = 1
  expand = 3
  formula = G4_lPROPANE
  name = G4_lPROPANE
  specific = 4
FEATURE [App::DocumentObjectGroupPython] C_element098  label="C_element : 056"  # scripted group (container) (typed FeaturePython)
  n = 3
  ref = C_element
FEATURE [App::DocumentObjectGroupPython] H_element090  label="H_element : 051"  # scripted group (container) (typed FeaturePython)
  n = 8
  ref = H_element
FEATURE [App::DocumentObjectGroupPython] O_element086  label="O_element : 047"  # scripted group (container) (typed FeaturePython)
  n = 1
  ref = O_element
FEATURE [App::DocumentObjectGroupPython] G4_N_PROPYL_ALCOHOL  label="G4_N-PROPYL_ALCOHOL"  # scripted group (container) (typed FeaturePython)
  Dunit = g/cm3
  Dvalue = 0.8035
  Group = -> [C_element098,H_element090,O_element086]
  conduct = 2
  density = 1
  expand = 3
  formula = G4_N-PROPYL_ALCOHOL
  name = G4_N-PROPYL_ALCOHOL
  specific = 4
FEATURE [App::DocumentObjectGroupPython] C_element099  label="C_element : 057"  # scripted group (container) (typed FeaturePython)
  n = 5
  ref = C_element
FEATURE [App::DocumentObjectGroupPython] H_element091  label="H_element : 052"  # scripted group (container) (typed FeaturePython)
  n = 5
  ref = H_element
FEATURE [App::DocumentObjectGroupPython] N_element038  label="N_element : 017"  # scripted group (container) (typed FeaturePython)
  n = 1
  ref = N_element
FEATURE [App::DocumentObjectGroupPython] G4_PYRIDINE  # scripted group (container) (typed FeaturePython)
  Dunit = g/cm3
  Dvalue = 0.9819
  Group = -> [C_element099,H_element091,N_element038]
  conduct = 2
  density = 1
  expand = 3
  formula = G4_PYRIDINE
  name = G4_PYRIDINE
  specific = 4
FEATURE [App::DocumentObjectGroupPython] H_element092  label="H_element : 0.144"  # scripted group (container) (typed FeaturePython)
  n = 0.143711
FEATURE [App::DocumentObjectGroupPython] C_element100  label="C_element : 0.856"  # scripted group (container) (typed FeaturePython)
  n = 0.856289
FEATURE [App::DocumentObjectGroupPython] G4_RUBBER_BUTYL  # scripted group (container) (typed FeaturePython)
  Dunit = g/cm3
  Dvalue = 0.92
  Group = -> [H_element092,C_element100]
  conduct = 2
  density = 1
  expand = 3
  formula = G4_RUBBER_BUTYL
  name = G4_RUBBER_BUTYL
  specific = 4
FEATURE [App::DocumentObjectGroupPython] H_element093  label="H_element : 0.118"  # scripted group (container) (typed FeaturePython)
  n = 0.118371
FEATURE [App::DocumentObjectGroupPython] C_element101  label="C_element : 0.882"  # scripted group (container) (typed FeaturePython)
  n = 0.881629
FEATURE [App::DocumentObjectGroupPython] G4_RUBBER_NATURAL  # scripted group (container) (typed FeaturePython)
  Dunit = g/cm3
  Dvalue = 0.92
  Group = -> [H_element093,C_element101]
  conduct = 2
  density = 1
  expand = 3
  formula = G4_RUBBER_NATURAL
  name = G4_RUBBER_NATURAL
  specific = 4
FEATURE [App::DocumentObjectGroupPython] H_element094  label="H_element : 0.145"  # scripted group (container) (typed FeaturePython)
  n = 0.05692
FEATURE [App::DocumentObjectGroupPython] C_element102  label="C_element : 0.543"  # scripted group (container) (typed FeaturePython)
  n = 0.542646
FEATURE [App::DocumentObjectGroupPython] Cl_element021  label="Cl_element : 0.400"  # scripted group (container) (typed FeaturePython)
  n = 0.400434
FEATURE [App::DocumentObjectGroupPython] G4_RUBBER_NEOPRENE  # scripted group (container) (typed FeaturePython)
  Dunit = g/cm3
  Dvalue = 1.23
  Group = -> [H_element094,C_element102,Cl_element021]
  conduct = 2
  density = 1
  expand = 3
  formula = G4_RUBBER_NEOPRENE
  name = G4_RUBBER_NEOPRENE
  specific = 4
FEATURE [App::DocumentObjectGroupPython] Si_element006  label="Si_element : 1"  # scripted group (container) (typed FeaturePython)
  n = 1
  ref = Si_element
FEATURE [App::DocumentObjectGroupPython] O_element087  label="O_element : 048"  # scripted group (container) (typed FeaturePython)
  n = 2
  ref = O_element
FEATURE [App::DocumentObjectGroupPython] G4_SILICON_DIOXIDE  # scripted group (container) (typed FeaturePython)
  Dunit = g/cm3
  Dvalue = 2.32
  Group = -> [Si_element006,O_element087]
  conduct = 2
  density = 1
  expand = 3
  formula = G4_SILICON_DIOXIDE
  name = G4_SILICON_DIOXIDE
  specific = 4
FEATURE [App::DocumentObjectGroupPython] Ag_element002  label="Ag_element : 1"  # scripted group (container) (typed FeaturePython)
  n = 1
  ref = Ag_element
FEATURE [App::DocumentObjectGroupPython] Br_element005  label="Br_element : 003"  # scripted group (container) (typed FeaturePython)
  n = 1
  ref = Br_element
FEATURE [App::DocumentObjectGroupPython] G4_SILVER_BROMIDE  # scripted group (container) (typed FeaturePython)
  Dunit = g/cm3
  Dvalue = 6.473
  Group = -> [Ag_element002,Br_element005]
  conduct = 2
  density = 1
  expand = 3
  formula = G4_SILVER_BROMIDE
  name = G4_SILVER_BROMIDE
  specific = 4
FEATURE [App::DocumentObjectGroupPython] Ag_element003  label="Ag_element : 002"  # scripted group (container) (typed FeaturePython)
  n = 1
  ref = Ag_element
FEATURE [App::DocumentObjectGroupPython] Cl_element022  label="Cl_element : 011"  # scripted group (container) (typed FeaturePython)
  n = 1
  ref = Cl_element
FEATURE [App::DocumentObjectGroupPython] G4_SILVER_CHLORIDE  # scripted group (container) (typed FeaturePython)
  Dunit = g/cm3
  Dvalue = 5.56
  Group = -> [Ag_element003,Cl_element022]
  conduct = 2
  density = 1
  expand = 3
  formula = G4_SILVER_CHLORIDE
  name = G4_SILVER_CHLORIDE
  specific = 4
FEATURE [App::DocumentObjectGroupPython] Br_element006  label="Br_element : 0.423"  # scripted group (container) (typed FeaturePython)
  n = 0.422895
FEATURE [App::DocumentObjectGroupPython] Ag_element004  label="Ag_element : 0.574"  # scripted group (container) (typed FeaturePython)
  n = 0.573748
FEATURE [App::DocumentObjectGroupPython] I_element007  label="I_element : 0.649"  # scripted group (container) (typed FeaturePython)
  n = 0.003357
FEATURE [App::DocumentObjectGroupPython] G4_SILVER_HALIDES  # scripted group (container) (typed FeaturePython)
  Dunit = g/cm3
  Dvalue = 6.47
  Group = -> [Br_element006,Ag_element004,I_element007]
  conduct = 2
  density = 1
  expand = 3
  formula = G4_SILVER_HALIDES
  name = G4_SILVER_HALIDES
  specific = 4
FEATURE [App::DocumentObjectGroupPython] Ag_element005  label="Ag_element : 003"  # scripted group (container) (typed FeaturePython)
  n = 1
  ref = Ag_element
FEATURE [App::DocumentObjectGroupPython] I_element008  label="I_element : 004"  # scripted group (container) (typed FeaturePython)
  n = 1
  ref = I_element
FEATURE [App::DocumentObjectGroupPython] G4_SILVER_IODIDE  # scripted group (container) (typed FeaturePython)
  Dunit = g/cm3
  Dvalue = 6.01
  Group = -> [Ag_element005,I_element008]
  conduct = 2
  density = 1
  expand = 3
  formula = G4_SILVER_IODIDE
  name = G4_SILVER_IODIDE
  specific = 4
FEATURE [App::DocumentObjectGroupPython] H_element095  label="H_element : 0.100"  # scripted group (container) (typed FeaturePython)
  n = 0.1
FEATURE [App::DocumentObjectGroupPython] C_element103  label="C_element : 0.204"  # scripted group (container) (typed FeaturePython)
  n = 0.204
FEATURE [App::DocumentObjectGroupPython] N_element039  label="N_element : 0.759"  # scripted group (container) (typed FeaturePython)
  n = 0.042
FEATURE [App::DocumentObjectGroupPython] O_element088  label="O_element : 0.645"  # scripted group (container) (typed FeaturePython)
  n = 0.645
FEATURE [App::DocumentObjectGroupPython] Na_element013  label="Na_element : 0.100"  # scripted group (container) (typed FeaturePython)
  n = 0.002
FEATURE [App::DocumentObjectGroupPython] P_element009  label="P_element : 0.107"  # scripted group (container) (typed FeaturePython)
  n = 0.001
FEATURE [App::DocumentObjectGroupPython] S_element020  label="S_element : 0.021"  # scripted group (container) (typed FeaturePython)
  n = 0.002
FEATURE [App::DocumentObjectGroupPython] Cl_element023  label="Cl_element : 0.590"  # scripted group (container) (typed FeaturePython)
  n = 0.003
FEATURE [App::DocumentObjectGroupPython] K_element010  label="K_element : 0.001"  # scripted group (container) (typed FeaturePython)
  n = 0.001
FEATURE [App::DocumentObjectGroupPython] G4_SKIN_ICRP  # scripted group (container) (typed FeaturePython)
  Dunit = g/cm3
  Dvalue = 1.09
  Group = -> [H_element095,C_element103,N_element039,O_element088,Na_element013,P_element009,S_element020,Cl_element023,K_element010]
  conduct = 2
  density = 1
  expand = 3
  formula = G4_SKIN_ICRP
  name = G4_SKIN_ICRP
  specific = 4
FEATURE [App::DocumentObjectGroupPython] Na_element014  label="Na_element : 2"  # scripted group (container) (typed FeaturePython)
  n = 2
  ref = Na_element
FEATURE [App::DocumentObjectGroupPython] C_element104  label="C_element : 058"  # scripted group (container) (typed FeaturePython)
  n = 1
  ref = C_element
FEATURE [App::DocumentObjectGroupPython] O_element089  label="O_element : 049"  # scripted group (container) (typed FeaturePython)
  n = 3
  ref = O_element
FEATURE [App::DocumentObjectGroupPython] G4_SODIUM_CARBONATE  # scripted group (container) (typed FeaturePython)
  Dunit = g/cm3
  Dvalue = 2.532
  Group = -> [Na_element014,C_element104,O_element089]
  conduct = 2
  density = 1
  expand = 3
  formula = G4_SODIUM_CARBONATE
  name = G4_SODIUM_CARBONATE
  specific = 4
FEATURE [App::DocumentObjectGroupPython] Na_element015  label="Na_element : 1"  # scripted group (container) (typed FeaturePython)
  n = 1
  ref = Na_element
FEATURE [App::DocumentObjectGroupPython] I_element009  label="I_element : 005"  # scripted group (container) (typed FeaturePython)
  n = 1
  ref = I_element
FEATURE [App::DocumentObjectGroupPython] G4_SODIUM_IODIDE  # scripted group (container) (typed FeaturePython)
  Dunit = g/cm3
  Dvalue = 3.667
  Group = -> [Na_element015,I_element009]
  conduct = 2
  density = 1
  expand = 3
  formula = G4_SODIUM_IODIDE
  name = G4_SODIUM_IODIDE
  specific = 4
FEATURE [App::DocumentObjectGroupPython] Na_element016  label="Na_element : 003"  # scripted group (container) (typed FeaturePython)
  n = 2
  ref = Na_element
FEATURE [App::DocumentObjectGroupPython] O_element090  label="O_element : 050"  # scripted group (container) (typed FeaturePython)
  n = 1
  ref = O_element
FEATURE [App::DocumentObjectGroupPython] G4_SODIUM_MONOXIDE  # scripted group (container) (typed FeaturePython)
  Dunit = g/cm3
  Dvalue = 2.27
  Group = -> [Na_element016,O_element090]
  conduct = 2
  density = 1
  expand = 3
  formula = G4_SODIUM_MONOXIDE
  name = G4_SODIUM_MONOXIDE
  specific = 4
FEATURE [App::DocumentObjectGroupPython] Na_element017  label="Na_element : 004"  # scripted group (container) (typed FeaturePython)
  n = 1
  ref = Na_element
FEATURE [App::DocumentObjectGroupPython] N_element040  label="N_element : 018"  # scripted group (container) (typed FeaturePython)
  n = 1
  ref = N_element
FEATURE [App::DocumentObjectGroupPython] O_element091  label="O_element : 051"  # scripted group (container) (typed FeaturePython)
  n = 3
  ref = O_element
FEATURE [App::DocumentObjectGroupPython] G4_SODIUM_NITRATE  # scripted group (container) (typed FeaturePython)
  Dunit = g/cm3
  Dvalue = 2.261
  Group = -> [Na_element017,N_element040,O_element091]
  conduct = 2
  density = 1
  expand = 3
  formula = G4_SODIUM_NITRATE
  name = G4_SODIUM_NITRATE
  specific = 4
FEATURE [App::DocumentObjectGroupPython] C_element105  label="C_element : 059"  # scripted group (container) (typed FeaturePython)
  n = 14
  ref = C_element
FEATURE [App::DocumentObjectGroupPython] H_element096  label="H_element : 053"  # scripted group (container) (typed FeaturePython)
  n = 12
  ref = H_element
FEATURE [App::DocumentObjectGroupPython] G4_STILBENE  # scripted group (container) (typed FeaturePython)
  Dunit = g/cm3
  Dvalue = 0.9707
  Group = -> [C_element105,H_element096]
  conduct = 2
  density = 1
  expand = 3
  formula = G4_STILBENE
  name = G4_STILBENE
  specific = 4
FEATURE [App::DocumentObjectGroupPython] C_element106  label="C_element : 12"  # scripted group (container) (typed FeaturePython)
  n = 12
  ref = C_element
FEATURE [App::DocumentObjectGroupPython] H_element097  label="H_element : 22"  # scripted group (container) (typed FeaturePython)
  n = 22
  ref = H_element
FEATURE [App::DocumentObjectGroupPython] O_element092  label="O_element : 11"  # scripted group (container) (typed FeaturePython)
  n = 11
  ref = O_element
FEATURE [App::DocumentObjectGroupPython] G4_SUCROSE  # scripted group (container) (typed FeaturePython)
  Dunit = g/cm3
  Dvalue = 1.5805
  Group = -> [C_element106,H_element097,O_element092]
  conduct = 2
  density = 1
  expand = 3
  formula = G4_SUCROSE
  name = G4_SUCROSE
  specific = 4
FEATURE [App::DocumentObjectGroupPython] C_element107  label="C_element : 18"  # scripted group (container) (typed FeaturePython)
  n = 18
  ref = C_element
FEATURE [App::DocumentObjectGroupPython] H_element098  label="H_element : 054"  # scripted group (container) (typed FeaturePython)
  n = 14
  ref = H_element
FEATURE [App::DocumentObjectGroupPython] G4_TERPHENYL  # scripted group (container) (typed FeaturePython)
  Dunit = g/cm3
  Dvalue = 1.24
  Group = -> [C_element107,H_element098]
  conduct = 2
  density = 1
  expand = 3
  formula = G4_TERPHENYL
  name = G4_TERPHENYL
  specific = 4
FEATURE [App::DocumentObjectGroupPython] H_element099  label="H_element : 0.146"  # scripted group (container) (typed FeaturePython)
  n = 0.106
FEATURE [App::DocumentObjectGroupPython] C_element108  label="C_element : 0.883"  # scripted group (container) (typed FeaturePython)
  n = 0.099
FEATURE [App::DocumentObjectGroupPython] N_element041  label="N_element : 0.020"  # scripted group (container) (typed FeaturePython)
  n = 0.02
FEATURE [App::DocumentObjectGroupPython] O_element093  label="O_element : 0.766"  # scripted group (container) (typed FeaturePython)
  n = 0.766
FEATURE [App::DocumentObjectGroupPython] Na_element018  label="Na_element : 0.101"  # scripted group (container) (typed FeaturePython)
  n = 0.002
FEATURE [App::DocumentObjectGroupPython] P_element010  label="P_element : 0.108"  # scripted group (container) (typed FeaturePython)
  n = 0.001
FEATURE [App::DocumentObjectGroupPython] S_element021  label="S_element : 0.022"  # scripted group (container) (typed FeaturePython)
  n = 0.002
FEATURE [App::DocumentObjectGroupPython] Cl_element024  label="Cl_element : 0.002"  # scripted group (container) (typed FeaturePython)
  n = 0.002
FEATURE [App::DocumentObjectGroupPython] K_element011  label="K_element : 0.017"  # scripted group (container) (typed FeaturePython)
  n = 0.002
FEATURE [App::DocumentObjectGroupPython] G4_TESTIS_ICRP  # scripted group (container) (typed FeaturePython)
  Dunit = g/cm3
  Dvalue = 1.04
  Group = -> [H_element099,C_element108,N_element041,O_element093,Na_element018,P_element010,S_element021,Cl_element024,K_element011]
  conduct = 2
  density = 1
  expand = 3
  formula = G4_TESTIS_ICRP
  name = G4_TESTIS_ICRP
  specific = 4
FEATURE [App::DocumentObjectGroupPython] C_element109  label="C_element : 060"  # scripted group (container) (typed FeaturePython)
  n = 2
  ref = C_element
FEATURE [App::DocumentObjectGroupPython] Cl_element025  label="Cl_element : 012"  # scripted group (container) (typed FeaturePython)
  n = 4
  ref = Cl_element
FEATURE [App::DocumentObjectGroupPython] G4_TETRACHLOROETHYLENE  # scripted group (container) (typed FeaturePython)
  Dunit = g/cm3
  Dvalue = 1.625
  Group = -> [C_element109,Cl_element025]
  conduct = 2
  density = 1
  expand = 3
  formula = G4_TETRACHLOROETHYLENE
  name = G4_TETRACHLOROETHYLENE
  specific = 4
FEATURE [App::DocumentObjectGroupPython] Tl_element001  label="Tl_element : 1"  # scripted group (container) (typed FeaturePython)
  n = 1
  ref = Tl_element
FEATURE [App::DocumentObjectGroupPython] Cl_element026  label="Cl_element : 013"  # scripted group (container) (typed FeaturePython)
  n = 1
  ref = Cl_element
FEATURE [App::DocumentObjectGroupPython] G4_THALLIUM_CHLORIDE  # scripted group (container) (typed FeaturePython)
  Dunit = g/cm3
  Dvalue = 7.004
  Group = -> [Tl_element001,Cl_element026]
  conduct = 2
  density = 1
  expand = 3
  formula = G4_THALLIUM_CHLORIDE
  name = G4_THALLIUM_CHLORIDE
  specific = 4
FEATURE [App::DocumentObjectGroupPython] H_element100  label="H_element : 0.147"  # scripted group (container) (typed FeaturePython)
  n = 0.105
FEATURE [App::DocumentObjectGroupPython] C_element110  label="C_element : 0.256"  # scripted group (container) (typed FeaturePython)
  n = 0.256
FEATURE [App::DocumentObjectGroupPython] N_element042  label="N_element : 0.760"  # scripted group (container) (typed FeaturePython)
  n = 0.027
FEATURE [App::DocumentObjectGroupPython] O_element094  label="O_element : 0.602"  # scripted group (container) (typed FeaturePython)
  n = 0.602
FEATURE [App::DocumentObjectGroupPython] Na_element019  label="Na_element : 0.102"  # scripted group (container) (typed FeaturePython)
  n = 0.001
FEATURE [App::DocumentObjectGroupPython] P_element011  label="P_element : 0.109"  # scripted group (container) (typed FeaturePython)
  n = 0.002
FEATURE [App::DocumentObjectGroupPython] S_element022  label="S_element : 0.023"  # scripted group (container) (typed FeaturePython)
  n = 0.003
FEATURE [App::DocumentObjectGroupPython] Cl_element027  label="Cl_element : 0.591"  # scripted group (container) (typed FeaturePython)
  n = 0.002
FEATURE [App::DocumentObjectGroupPython] K_element012  label="K_element : 0.018"  # scripted group (container) (typed FeaturePython)
  n = 0.002
FEATURE [App::DocumentObjectGroupPython] G4_TISSUE_SOFT_ICRP  # scripted group (container) (typed FeaturePython)
  Dunit = g/cm3
  Dvalue = 1.03
  Group = -> [H_element100,C_element110,N_element042,O_element094,Na_element019,P_element011,S_element022,Cl_element027,K_element012]
  conduct = 2
  density = 1
  expand = 3
  formula = G4_TISSUE_SOFT_ICRP
  name = G4_TISSUE_SOFT_ICRP
  specific = 4
FEATURE [App::DocumentObjectGroupPython] H_element101  label="H_element : 0.148"  # scripted group (container) (typed FeaturePython)
  n = 0.101
FEATURE [App::DocumentObjectGroupPython] C_element111  label="C_element : 0.111"  # scripted group (container) (typed FeaturePython)
  n = 0.111
FEATURE [App::DocumentObjectGroupPython] N_element043  label="N_element : 0.026"  # scripted group (container) (typed FeaturePython)
  n = 0.026
FEATURE [App::DocumentObjectGroupPython] O_element095  label="O_element : 0.762"  # scripted group (container) (typed FeaturePython)
  n = 0.762
FEATURE [App::DocumentObjectGroupPython] G4_TISSUE_SOFT_ICRU_4  label="G4_TISSUE_SOFT_ICRU-4"  # scripted group (container) (typed FeaturePython)
  Dunit = g/cm3
  Dvalue = 1
  Group = -> [H_element101,C_element111,N_element043,O_element095]
  conduct = 2
  density = 1
  expand = 3
  formula = G4_TISSUE_SOFT_ICRU-4
  name = G4_TISSUE_SOFT_ICRU-4
  specific = 4
FEATURE [App::DocumentObjectGroupPython] H_element102  label="H_element : 0.149"  # scripted group (container) (typed FeaturePython)
  n = 0.101869
FEATURE [App::DocumentObjectGroupPython] C_element112  label="C_element : 0.456"  # scripted group (container) (typed FeaturePython)
  n = 0.456179
FEATURE [App::DocumentObjectGroupPython] N_element044  label="N_element : 0.761"  # scripted group (container) (typed FeaturePython)
  n = 0.035172
FEATURE [App::DocumentObjectGroupPython] O_element096  label="O_element : 0.407"  # scripted group (container) (typed FeaturePython)
  n = 0.40678
FEATURE [App::DocumentObjectGroupPython] G4_TISSUE_METHANE  label="G4_TISSUE-METHANE"  # scripted group (container) (typed FeaturePython)
  Dunit = g/cm3
  Dvalue = 0.00106409
  Group = -> [H_element102,C_element112,N_element044,O_element096]
  conduct = 2
  density = 1
  expand = 3
  formula = G4_TISSUE-METHANE
  name = G4_TISSUE-METHANE
  specific = 4
FEATURE [App::DocumentObjectGroupPython] H_element103  label="H_element : 0.103"  # scripted group (container) (typed FeaturePython)
  n = 0.102672
FEATURE [App::DocumentObjectGroupPython] C_element113  label="C_element : 0.569"  # scripted group (container) (typed FeaturePython)
  n = 0.56894
FEATURE [App::DocumentObjectGroupPython] N_element045  label="N_element : 0.762"  # scripted group (container) (typed FeaturePython)
  n = 0.035022
FEATURE [App::DocumentObjectGroupPython] O_element097  label="O_element : 0.293"  # scripted group (container) (typed FeaturePython)
  n = 0.293366
FEATURE [App::DocumentObjectGroupPython] G4_TISSUE_PROPANE  label="G4_TISSUE-PROPANE"  # scripted group (container) (typed FeaturePython)
  Dunit = g/cm3
  Dvalue = 0.00182628
  Group = -> [H_element103,C_element113,N_element045,O_element097]
  conduct = 2
  density = 1
  expand = 3
  formula = G4_TISSUE-PROPANE
  name = G4_TISSUE-PROPANE
  specific = 4
FEATURE [App::DocumentObjectGroupPython] Ti_element003  label="Ti_element : 1"  # scripted group (container) (typed FeaturePython)
  n = 1
  ref = Ti_element
FEATURE [App::DocumentObjectGroupPython] O_element098  label="O_element : 052"  # scripted group (container) (typed FeaturePython)
  n = 2
  ref = O_element
FEATURE [App::DocumentObjectGroupPython] G4_TITANIUM_DIOXIDE  # scripted group (container) (typed FeaturePython)
  Dunit = g/cm3
  Dvalue = 4.26
  Group = -> [Ti_element003,O_element098]
  conduct = 2
  density = 1
  expand = 3
  formula = G4_TITANIUM_DIOXIDE
  name = G4_TITANIUM_DIOXIDE
  specific = 4
FEATURE [App::DocumentObjectGroupPython] C_element114  label="C_element : 061"  # scripted group (container) (typed FeaturePython)
  n = 7
  ref = C_element
FEATURE [App::DocumentObjectGroupPython] H_element104  label="H_element : 055"  # scripted group (container) (typed FeaturePython)
  n = 8
  ref = H_element
FEATURE [App::DocumentObjectGroupPython] G4_TOLUENE  # scripted group (container) (typed FeaturePython)
  Dunit = g/cm3
  Dvalue = 0.8669
  Group = -> [C_element114,H_element104]
  conduct = 2
  density = 1
  expand = 3
  formula = G4_TOLUENE
  name = G4_TOLUENE
  specific = 4
FEATURE [App::DocumentObjectGroupPython] C_element115  label="C_element : 062"  # scripted group (container) (typed FeaturePython)
  n = 2
  ref = C_element
FEATURE [App::DocumentObjectGroupPython] H_element105  label="H_element : 056"  # scripted group (container) (typed FeaturePython)
  n = 1
  ref = H_element
FEATURE [App::DocumentObjectGroupPython] Cl_element028  label="Cl_element : 014"  # scripted group (container) (typed FeaturePython)
  n = 3
  ref = Cl_element
FEATURE [App::DocumentObjectGroupPython] G4_TRICHLOROETHYLENE  # scripted group (container) (typed FeaturePython)
  Dunit = g/cm3
  Dvalue = 1.46
  Group = -> [C_element115,H_element105,Cl_element028]
  conduct = 2
  density = 1
  expand = 3
  formula = G4_TRICHLOROETHYLENE
  name = G4_TRICHLOROETHYLENE
  specific = 4
FEATURE [App::DocumentObjectGroupPython] C_element116  label="C_element : 063"  # scripted group (container) (typed FeaturePython)
  n = 6
  ref = C_element
FEATURE [App::DocumentObjectGroupPython] H_element106  label="H_element : 15"  # scripted group (container) (typed FeaturePython)
  n = 15
  ref = H_element
FEATURE [App::DocumentObjectGroupPython] O_element099  label="O_element : 053"  # scripted group (container) (typed FeaturePython)
  n = 4
  ref = O_element
FEATURE [App::DocumentObjectGroupPython] P_element012  label="P_element : 1"  # scripted group (container) (typed FeaturePython)
  n = 1
  ref = P_element
FEATURE [App::DocumentObjectGroupPython] G4_TRIETHYL_PHOSPHATE  # scripted group (container) (typed FeaturePython)
  Dunit = g/cm3
  Dvalue = 1.07
  Group = -> [C_element116,H_element106,O_element099,P_element012]
  conduct = 2
  density = 1
  expand = 3
  formula = G4_TRIETHYL_PHOSPHATE
  name = G4_TRIETHYL_PHOSPHATE
  specific = 4
FEATURE [App::DocumentObjectGroupPython] W_element003  label="W_element : 003"  # scripted group (container) (typed FeaturePython)
  n = 1
  ref = W_element
FEATURE [App::DocumentObjectGroupPython] F_element017  label="F_element : 6"  # scripted group (container) (typed FeaturePython)
  n = 6
  ref = F_element
FEATURE [App::DocumentObjectGroupPython] G4_TUNGSTEN_HEXAFLUORIDE  # scripted group (container) (typed FeaturePython)
  Dunit = g/cm3
  Dvalue = 2.4
  Group = -> [W_element003,F_element017]
  conduct = 2
  density = 1
  expand = 3
  formula = G4_TUNGSTEN_HEXAFLUORIDE
  name = G4_TUNGSTEN_HEXAFLUORIDE
  specific = 4
FEATURE [App::DocumentObjectGroupPython] U_element001  label="U_element : 1"  # scripted group (container) (typed FeaturePython)
  n = 1
  ref = U_element
FEATURE [App::DocumentObjectGroupPython] C_element117  label="C_element : 064"  # scripted group (container) (typed FeaturePython)
  n = 2
  ref = C_element
FEATURE [App::DocumentObjectGroupPython] G4_URANIUM_DICARBIDE  # scripted group (container) (typed FeaturePython)
  Dunit = g/cm3
  Dvalue = 11.28
  Group = -> [U_element001,C_element117]
  conduct = 2
  density = 1
  expand = 3
  formula = G4_URANIUM_DICARBIDE
  name = G4_URANIUM_DICARBIDE
  specific = 4
FEATURE [App::DocumentObjectGroupPython] U_element002  label="U_element : 002"  # scripted group (container) (typed FeaturePython)
  n = 1
  ref = U_element
FEATURE [App::DocumentObjectGroupPython] C_element118  label="C_element : 065"  # scripted group (container) (typed FeaturePython)
  n = 1
  ref = C_element
FEATURE [App::DocumentObjectGroupPython] G4_URANIUM_MONOCARBIDE  # scripted group (container) (typed FeaturePython)
  Dunit = g/cm3
  Dvalue = 13.63
  Group = -> [U_element002,C_element118]
  conduct = 2
  density = 1
  expand = 3
  formula = G4_URANIUM_MONOCARBIDE
  name = G4_URANIUM_MONOCARBIDE
  specific = 4
FEATURE [App::DocumentObjectGroupPython] U_element003  label="U_element : 003"  # scripted group (container) (typed FeaturePython)
  n = 1
  ref = U_element
FEATURE [App::DocumentObjectGroupPython] O_element100  label="O_element : 054"  # scripted group (container) (typed FeaturePython)
  n = 2
  ref = O_element
FEATURE [App::DocumentObjectGroupPython] G4_URANIUM_OXIDE  # scripted group (container) (typed FeaturePython)
  Dunit = g/cm3
  Dvalue = 10.96
  Group = -> [U_element003,O_element100]
  conduct = 2
  density = 1
  expand = 3
  formula = G4_URANIUM_OXIDE
  name = G4_URANIUM_OXIDE
  specific = 4
FEATURE [App::DocumentObjectGroupPython] C_element119  label="C_element : 066"  # scripted group (container) (typed FeaturePython)
  n = 1
  ref = C_element
FEATURE [App::DocumentObjectGroupPython] H_element107  label="H_element : 057"  # scripted group (container) (typed FeaturePython)
  n = 4
  ref = H_element
FEATURE [App::DocumentObjectGroupPython] N_element046  label="N_element : 019"  # scripted group (container) (typed FeaturePython)
  n = 2
  ref = N_element
FEATURE [App::DocumentObjectGroupPython] O_element101  label="O_element : 055"  # scripted group (container) (typed FeaturePython)
  n = 1
  ref = O_element
FEATURE [App::DocumentObjectGroupPython] G4_UREA  # scripted group (container) (typed FeaturePython)
  Dunit = g/cm3
  Dvalue = 1.323
  Group = -> [C_element119,H_element107,N_element046,O_element101]
  conduct = 2
  density = 1
  expand = 3
  formula = G4_UREA
  name = G4_UREA
  specific = 4
FEATURE [App::DocumentObjectGroupPython] C_element120  label="C_element : 067"  # scripted group (container) (typed FeaturePython)
  n = 5
  ref = C_element
FEATURE [App::DocumentObjectGroupPython] H_element108  label="H_element : 058"  # scripted group (container) (typed FeaturePython)
  n = 11
  ref = H_element
FEATURE [App::DocumentObjectGroupPython] N_element047  label="N_element : 020"  # scripted group (container) (typed FeaturePython)
  n = 1
  ref = N_element
FEATURE [App::DocumentObjectGroupPython] O_element102  label="O_element : 056"  # scripted group (container) (typed FeaturePython)
  n = 2
  ref = O_element
FEATURE [App::DocumentObjectGroupPython] G4_VALINE  # scripted group (container) (typed FeaturePython)
  Dunit = g/cm3
  Dvalue = 1.23
  Group = -> [C_element120,H_element108,N_element047,O_element102]
  conduct = 2
  density = 1
  expand = 3
  formula = G4_VALINE
  name = G4_VALINE
  specific = 4
FEATURE [App::DocumentObjectGroupPython] H_element109  label="H_element : 0.009"  # scripted group (container) (typed FeaturePython)
  n = 0.009417
FEATURE [App::DocumentObjectGroupPython] C_element121  label="C_element : 0.281"  # scripted group (container) (typed FeaturePython)
  n = 0.280555
FEATURE [App::DocumentObjectGroupPython] F_element018  label="F_element : 0.710"  # scripted group (container) (typed FeaturePython)
  n = 0.710028
FEATURE [App::DocumentObjectGroupPython] G4_VITON  # scripted group (container) (typed FeaturePython)
  Dunit = g/cm3
  Dvalue = 1.8
  Group = -> [H_element109,C_element121,F_element018]
  conduct = 2
  density = 1
  expand = 3
  formula = G4_VITON
  name = G4_VITON
  specific = 4
FEATURE [App::DocumentObjectGroupPython] H_element110  label="H_element : 059"  # scripted group (container) (typed FeaturePython)
  n = 2
  ref = H_element
FEATURE [App::DocumentObjectGroupPython] O_element103  label="O_element : 057"  # scripted group (container) (typed FeaturePython)
  n = 1
  ref = O_element
FEATURE [App::DocumentObjectGroupPython] G4_WATER  # scripted group (container) (typed FeaturePython)
  Dunit = g/cm3
  Dvalue = 1
  Group = -> [H_element110,O_element103]
  conduct = 2
  density = 1
  expand = 3
  formula = G4_WATER
  name = G4_WATER
  specific = 4
FEATURE [App::DocumentObjectGroupPython] H_element111  label="H_element : 060"  # scripted group (container) (typed FeaturePython)
  n = 2
  ref = H_element
FEATURE [App::DocumentObjectGroupPython] O_element104  label="O_element : 058"  # scripted group (container) (typed FeaturePython)
  n = 1
  ref = O_element
FEATURE [App::DocumentObjectGroupPython] G4_WATER_VAPOR  # scripted group (container) (typed FeaturePython)
  Dunit = g/cm3
  Dvalue = 0.000756182
  Group = -> [H_element111,O_element104]
  conduct = 2
  density = 1
  expand = 3
  formula = G4_WATER_VAPOR
  name = G4_WATER_VAPOR
  specific = 4
FEATURE [App::DocumentObjectGroupPython] C_element122  label="C_element : 068"  # scripted group (container) (typed FeaturePython)
  n = 8
  ref = C_element
FEATURE [App::DocumentObjectGroupPython] H_element112  label="H_element : 061"  # scripted group (container) (typed FeaturePython)
  n = 10
  ref = H_element
FEATURE [App::DocumentObjectGroupPython] G4_XYLENE  # scripted group (container) (typed FeaturePython)
  Dunit = g/cm3
  Dvalue = 0.87
  Group = -> [C_element122,H_element112]
  conduct = 2
  density = 1
  expand = 3
  formula = G4_XYLENE
  name = G4_XYLENE
  specific = 4
FEATURE [App::DocumentObjectGroupPython] C_element123  label="C_element : 069"  # scripted group (container) (typed FeaturePython)
  n = 1
  ref = C_element
FEATURE [App::DocumentObjectGroupPython] G4_GRAPHITE  # scripted group (container) (typed FeaturePython)
  Dunit = g/cm3
  Dvalue = 2.21
  Group = -> [C_element123]
  conduct = 2
  density = 1
  expand = 3
  formula = G4_GRAPHITE
  name = G4_GRAPHITE
  specific = 4
FEATURE [App::DocumentObjectGroupPython] NIST  # scripted group (container) (typed FeaturePython)
  Group = -> [G4_A_150_TISSUE,G4_ACETONE,G4_ACETYLENE,G4_ADENINE,G4_ADIPOSE_TISSUE_ICRP,G4_AIR,G4_ALANINE,G4_ALUMINUM_OXIDE,G4_AMBER,G4_AMMONIA,G4_ANILINE,G4_ANTHRACENE,G4_B_100_BONE,G4_BAKELITE,G4_BARIUM_FLUORIDE,G4_BARIUM_SULFATE,G4_BENZENE,G4_BERYLLIUM_OXIDE,G4_BGO,G4_BLOOD_ICRP,G4_BONE_COMPACT_ICRU,G4_BONE_CORTICAL_ICRP,G4_BORON_CARBIDE,G4_BORON_OXIDE,G4_BRAIN_ICRP,G4_BUTANE,G4_N_BUTYL_ALCOHOL,G4_C_552,+152 more]
FEATURE [App::DocumentObjectGroupPython] H_element113  label="H_element : 062"  # scripted group (container) (typed FeaturePython)
  n = 1
  ref = H_element
FEATURE [App::DocumentObjectGroupPython] G4_H  # scripted group (container) (typed FeaturePython)
  Dunit = g/cm3
  Dvalue = 8.3748e-05
  Group = -> [H_element113]
  conduct = 2
  density = 1
  expand = 3
  formula = H
  name = G4_H
  specific = 4
FEATURE [App::DocumentObjectGroupPython] He_element001  label="He_element : 1"  # scripted group (container) (typed FeaturePython)
  n = 1
  ref = He_element
FEATURE [App::DocumentObjectGroupPython] G4_He  # scripted group (container) (typed FeaturePython)
  Dunit = g/cm3
  Dvalue = 0.000166322
  Group = -> [He_element001]
  conduct = 2
  density = 1
  expand = 3
  formula = He
  name = G4_He
  specific = 4
FEATURE [App::DocumentObjectGroupPython] Li_element008  label="Li_element : 008"  # scripted group (container) (typed FeaturePython)
  n = 1
  ref = Li_element
FEATURE [App::DocumentObjectGroupPython] G4_Li  # scripted group (container) (typed FeaturePython)
  Dunit = g/cm3
  Dvalue = 0.534
  Group = -> [Li_element008]
  conduct = 2
  density = 1
  expand = 3
  formula = Li
  name = G4_Li
  specific = 4
FEATURE [App::DocumentObjectGroupPython] Be_element002  label="Be_element : 002"  # scripted group (container) (typed FeaturePython)
  n = 1
  ref = Be_element
FEATURE [App::DocumentObjectGroupPython] G4_Be  # scripted group (container) (typed FeaturePython)
  Dunit = g/cm3
  Dvalue = 1.848
  Group = -> [Be_element002]
  conduct = 2
  density = 1
  expand = 3
  formula = Be
  name = G4_Be
  specific = 4
FEATURE [App::DocumentObjectGroupPython] B_element007  label="B_element : 007"  # scripted group (container) (typed FeaturePython)
  n = 1
  ref = B_element
FEATURE [App::DocumentObjectGroupPython] G4_B  # scripted group (container) (typed FeaturePython)
  Dunit = g/cm3
  Dvalue = 2.37
  Group = -> [B_element007]
  conduct = 2
  density = 1
  expand = 3
  formula = B
  name = G4_B
  specific = 4
FEATURE [App::DocumentObjectGroupPython] C_element124  label="C_element : 070"  # scripted group (container) (typed FeaturePython)
  n = 1
  ref = C_element
FEATURE [App::DocumentObjectGroupPython] G4_C  # scripted group (container) (typed FeaturePython)
  Dunit = g/cm3
  Dvalue = 2
  Group = -> [C_element124]
  conduct = 2
  density = 1
  expand = 3
  formula = C
  name = G4_C
  specific = 4
FEATURE [App::DocumentObjectGroupPython] N_element048  label="N_element : 021"  # scripted group (container) (typed FeaturePython)
  n = 1
  ref = N_element
FEATURE [App::DocumentObjectGroupPython] G4_N  # scripted group (container) (typed FeaturePython)
  Dunit = g/cm3
  Dvalue = 0.0011652
  Group = -> [N_element048]
  conduct = 2
  density = 1
  expand = 3
  formula = N
  name = G4_N
  specific = 4
FEATURE [App::DocumentObjectGroupPython] O_element105  label="O_element : 059"  # scripted group (container) (typed FeaturePython)
  n = 1
  ref = O_element
FEATURE [App::DocumentObjectGroupPython] G4_O  # scripted group (container) (typed FeaturePython)
  Dunit = g/cm3
  Dvalue = 0.00133151
  Group = -> [O_element105]
  conduct = 2
  density = 1
  expand = 3
  formula = O
  name = G4_O
  specific = 4
FEATURE [App::DocumentObjectGroupPython] F_element019  label="F_element : 008"  # scripted group (container) (typed FeaturePython)
  n = 1
  ref = F_element
FEATURE [App::DocumentObjectGroupPython] G4_F  # scripted group (container) (typed FeaturePython)
  Dunit = g/cm3
  Dvalue = 0.00158029
  Group = -> [F_element019]
  conduct = 2
  density = 1
  expand = 3
  formula = F
  name = G4_F
  specific = 4
FEATURE [App::DocumentObjectGroupPython] Ne_element001  label="Ne_element : 1"  # scripted group (container) (typed FeaturePython)
  n = 1
  ref = Ne_element
FEATURE [App::DocumentObjectGroupPython] G4_Ne  # scripted group (container) (typed FeaturePython)
  Dunit = g/cm3
  Dvalue = 0.000838505
  Group = -> [Ne_element001]
  conduct = 2
  density = 1
  expand = 3
  formula = Ne
  name = G4_Ne
  specific = 4
FEATURE [App::DocumentObjectGroupPython] Na_element020  label="Na_element : 005"  # scripted group (container) (typed FeaturePython)
  n = 1
  ref = Na_element
FEATURE [App::DocumentObjectGroupPython] G4_Na  # scripted group (container) (typed FeaturePython)
  Dunit = g/cm3
  Dvalue = 0.971
  Group = -> [Na_element020]
  conduct = 2
  density = 1
  expand = 3
  formula = Na
  name = G4_Na
  specific = 4
FEATURE [App::DocumentObjectGroupPython] Mg_element011  label="Mg_element : 005"  # scripted group (container) (typed FeaturePython)
  n = 1
  ref = Mg_element
FEATURE [App::DocumentObjectGroupPython] G4_Mg  # scripted group (container) (typed FeaturePython)
  Dunit = g/cm3
  Dvalue = 1.74
  Group = -> [Mg_element011]
  conduct = 2
  density = 1
  expand = 3
  formula = Mg
  name = G4_Mg
  specific = 4
FEATURE [App::DocumentObjectGroupPython] Al_element004  label="Al_element : 1"  # scripted group (container) (typed FeaturePython)
  n = 1
  ref = Al_element
FEATURE [App::DocumentObjectGroupPython] G4_Al  # scripted group (container) (typed FeaturePython)
  Dunit = g/cm3
  Dvalue = 2.699
  Group = -> [Al_element004]
  conduct = 2
  density = 1
  expand = 3
  formula = Al
  name = G4_Al
  specific = 4
FEATURE [App::DocumentObjectGroupPython] Si_element007  label="Si_element : 002"  # scripted group (container) (typed FeaturePython)
  n = 1
  ref = Si_element
FEATURE [App::DocumentObjectGroupPython] G4_Si  # scripted group (container) (typed FeaturePython)
  Dunit = g/cm3
  Dvalue = 2.33
  Group = -> [Si_element007]
  conduct = 2
  density = 1
  expand = 3
  formula = Si
  name = G4_Si
  specific = 4
FEATURE [App::DocumentObjectGroupPython] P_element013  label="P_element : 002"  # scripted group (container) (typed FeaturePython)
  n = 1
  ref = P_element
FEATURE [App::DocumentObjectGroupPython] G4_P  # scripted group (container) (typed FeaturePython)
  Dunit = g/cm3
  Dvalue = 2.2
  Group = -> [P_element013]
  conduct = 2
  density = 1
  expand = 3
  formula = P
  name = G4_P
  specific = 4
FEATURE [App::DocumentObjectGroupPython] S_element023  label="S_element : 007"  # scripted group (container) (typed FeaturePython)
  n = 1
  ref = S_element
FEATURE [App::DocumentObjectGroupPython] G4_S  # scripted group (container) (typed FeaturePython)
  Dunit = g/cm3
  Dvalue = 2
  Group = -> [S_element023]
  conduct = 2
  density = 1
  expand = 3
  formula = S
  name = G4_S
  specific = 4
FEATURE [App::DocumentObjectGroupPython] Cl_element029  label="Cl_element : 015"  # scripted group (container) (typed FeaturePython)
  n = 1
  ref = Cl_element
FEATURE [App::DocumentObjectGroupPython] G4_Cl  # scripted group (container) (typed FeaturePython)
  Dunit = g/cm3
  Dvalue = 0.00299473
  Group = -> [Cl_element029]
  conduct = 2
  density = 1
  expand = 3
  formula = Cl
  name = G4_Cl
  specific = 4
FEATURE [App::DocumentObjectGroupPython] Ar_element002  label="Ar_element : 1"  # scripted group (container) (typed FeaturePython)
  n = 1
  ref = Ar_element
FEATURE [App::DocumentObjectGroupPython] G4_Ar  # scripted group (container) (typed FeaturePython)
  Dunit = g/cm3
  Dvalue = 0.00166201
  Group = -> [Ar_element002]
  conduct = 2
  density = 1
  expand = 3
  formula = Ar
  name = G4_Ar
  specific = 4
FEATURE [App::DocumentObjectGroupPython] K_element013  label="K_element : 003"  # scripted group (container) (typed FeaturePython)
  n = 1
  ref = K_element
FEATURE [App::DocumentObjectGroupPython] G4_K  # scripted group (container) (typed FeaturePython)
  Dunit = g/cm3
  Dvalue = 0.862
  Group = -> [K_element013]
  conduct = 2
  density = 1
  expand = 3
  formula = K
  name = G4_K
  specific = 4
FEATURE [App::DocumentObjectGroupPython] Ca_element014  label="Ca_element : 007"  # scripted group (container) (typed FeaturePython)
  n = 1
  ref = Ca_element
FEATURE [App::DocumentObjectGroupPython] G4_Ca  # scripted group (container) (typed FeaturePython)
  Dunit = g/cm3
  Dvalue = 1.55
  Group = -> [Ca_element014]
  conduct = 2
  density = 1
  expand = 3
  formula = Ca
  name = G4_Ca
  specific = 4
FEATURE [App::DocumentObjectGroupPython] Sc_element001  label="Sc_element : 1"  # scripted group (container) (typed FeaturePython)
  n = 1
  ref = Sc_element
FEATURE [App::DocumentObjectGroupPython] G4_Sc  # scripted group (container) (typed FeaturePython)
  Dunit = g/cm3
  Dvalue = 2.989
  Group = -> [Sc_element001]
  conduct = 2
  density = 1
  expand = 3
  formula = Sc
  name = G4_Sc
  specific = 4
FEATURE [App::DocumentObjectGroupPython] Ti_element004  label="Ti_element : 002"  # scripted group (container) (typed FeaturePython)
  n = 1
  ref = Ti_element
FEATURE [App::DocumentObjectGroupPython] G4_Ti  # scripted group (container) (typed FeaturePython)
  Dunit = g/cm3
  Dvalue = 4.54
  Group = -> [Ti_element004]
  conduct = 2
  density = 1
  expand = 3
  formula = Ti
  name = G4_Ti
  specific = 4
FEATURE [App::DocumentObjectGroupPython] V_element001  label="V_element : 1"  # scripted group (container) (typed FeaturePython)
  n = 1
  ref = V_element
FEATURE [App::DocumentObjectGroupPython] G4_V  # scripted group (container) (typed FeaturePython)
  Dunit = g/cm3
  Dvalue = 6.11
  Group = -> [V_element001]
  conduct = 2
  density = 1
  expand = 3
  formula = V
  name = G4_V
  specific = 4
FEATURE [App::DocumentObjectGroupPython] Cr_element001  label="Cr_element : 1"  # scripted group (container) (typed FeaturePython)
  n = 1
  ref = Cr_element
FEATURE [App::DocumentObjectGroupPython] G4_Cr  # scripted group (container) (typed FeaturePython)
  Dunit = g/cm3
  Dvalue = 7.18
  Group = -> [Cr_element001]
  conduct = 2
  density = 1
  expand = 3
  formula = Cr
  name = G4_Cr
  specific = 4
FEATURE [App::DocumentObjectGroupPython] Mn_element001  label="Mn_element : 1"  # scripted group (container) (typed FeaturePython)
  n = 1
  ref = Mn_element
FEATURE [App::DocumentObjectGroupPython] G4_Mn  # scripted group (container) (typed FeaturePython)
  Dunit = g/cm3
  Dvalue = 7.44
  Group = -> [Mn_element001]
  conduct = 2
  density = 1
  expand = 3
  formula = Mn
  name = G4_Mn
  specific = 4
FEATURE [App::DocumentObjectGroupPython] Fe_element007  label="Fe_element : 004"  # scripted group (container) (typed FeaturePython)
  n = 1
  ref = Fe_element
FEATURE [App::DocumentObjectGroupPython] G4_Fe  # scripted group (container) (typed FeaturePython)
  Dunit = g/cm3
  Dvalue = 7.874
  Group = -> [Fe_element007]
  conduct = 2
  density = 1
  expand = 3
  formula = Fe
  name = G4_Fe
  specific = 4
FEATURE [App::DocumentObjectGroupPython] Co_element001  label="Co_element : 1"  # scripted group (container) (typed FeaturePython)
  n = 1
  ref = Co_element
FEATURE [App::DocumentObjectGroupPython] G4_Co  # scripted group (container) (typed FeaturePython)
  Dunit = g/cm3
  Dvalue = 8.9
  Group = -> [Co_element001]
  conduct = 2
  density = 1
  expand = 3
  formula = Co
  name = G4_Co
  specific = 4
FEATURE [App::DocumentObjectGroupPython] Ni_element001  label="Ni_element : 1"  # scripted group (container) (typed FeaturePython)
  n = 1
  ref = Ni_element
FEATURE [App::DocumentObjectGroupPython] G4_Ni  # scripted group (container) (typed FeaturePython)
  Dunit = g/cm3
  Dvalue = 8.902
  Group = -> [Ni_element001]
  conduct = 2
  density = 1
  expand = 3
  formula = Ni
  name = G4_Ni
  specific = 4
FEATURE [App::DocumentObjectGroupPython] Cu_element001  label="Cu_element : 1"  # scripted group (container) (typed FeaturePython)
  n = 1
  ref = Cu_element
FEATURE [App::DocumentObjectGroupPython] G4_Cu  # scripted group (container) (typed FeaturePython)
  Dunit = g/cm3
  Dvalue = 8.96
  Group = -> [Cu_element001]
  conduct = 2
  density = 1
  expand = 3
  formula = Cu
  name = G4_Cu
  specific = 4
FEATURE [App::DocumentObjectGroupPython] Zn_element001  label="Zn_element : 1"  # scripted group (container) (typed FeaturePython)
  n = 1
  ref = Zn_element
FEATURE [App::DocumentObjectGroupPython] G4_Zn  # scripted group (container) (typed FeaturePython)
  Dunit = g/cm3
  Dvalue = 7.133
  Group = -> [Zn_element001]
  conduct = 2
  density = 1
  expand = 3
  formula = Zn
  name = G4_Zn
  specific = 4
FEATURE [App::DocumentObjectGroupPython] Ga_element002  label="Ga_element : 002"  # scripted group (container) (typed FeaturePython)
  n = 1
  ref = Ga_element
FEATURE [App::DocumentObjectGroupPython] G4_Ga  # scripted group (container) (typed FeaturePython)
  Dunit = g/cm3
  Dvalue = 5.904
  Group = -> [Ga_element002]
  conduct = 2
  density = 1
  expand = 3
  formula = Ga
  name = G4_Ga
  specific = 4
FEATURE [App::DocumentObjectGroupPython] Ge_element002  label="Ge_element : 1"  # scripted group (container) (typed FeaturePython)
  n = 1
  ref = Ge_element
FEATURE [App::DocumentObjectGroupPython] G4_Ge  # scripted group (container) (typed FeaturePython)
  Dunit = g/cm3
  Dvalue = 5.323
  Group = -> [Ge_element002]
  conduct = 2
  density = 1
  expand = 3
  formula = Ge
  name = G4_Ge
  specific = 4
FEATURE [App::DocumentObjectGroupPython] As_element003  label="As_element : 002"  # scripted group (container) (typed FeaturePython)
  n = 1
  ref = As_element
FEATURE [App::DocumentObjectGroupPython] G4_As  # scripted group (container) (typed FeaturePython)
  Dunit = g/cm3
  Dvalue = 5.73
  Group = -> [As_element003]
  conduct = 2
  density = 1
  expand = 3
  formula = As
  name = G4_As
  specific = 4
FEATURE [App::DocumentObjectGroupPython] Se_element001  label="Se_element : 1"  # scripted group (container) (typed FeaturePython)
  n = 1
  ref = Se_element
FEATURE [App::DocumentObjectGroupPython] G4_Se  # scripted group (container) (typed FeaturePython)
  Dunit = g/cm3
  Dvalue = 4.5
  Group = -> [Se_element001]
  conduct = 2
  density = 1
  expand = 3
  formula = Se
  name = G4_Se
  specific = 4
FEATURE [App::DocumentObjectGroupPython] Br_element007  label="Br_element : 004"  # scripted group (container) (typed FeaturePython)
  n = 1
  ref = Br_element
FEATURE [App::DocumentObjectGroupPython] G4_Br  # scripted group (container) (typed FeaturePython)
  Dunit = g/cm3
  Dvalue = 0.0070721
  Group = -> [Br_element007]
  conduct = 2
  density = 1
  expand = 3
  formula = Br
  name = G4_Br
  specific = 4
FEATURE [App::DocumentObjectGroupPython] Kr_element001  label="Kr_element : 1"  # scripted group (container) (typed FeaturePython)
  n = 1
  ref = Kr_element
FEATURE [App::DocumentObjectGroupPython] G4_Kr  # scripted group (container) (typed FeaturePython)
  Dunit = g/cm3
  Dvalue = 0.00347832
  Group = -> [Kr_element001]
  conduct = 2
  density = 1
  expand = 3
  formula = Kr
  name = G4_Kr
  specific = 4
FEATURE [App::DocumentObjectGroupPython] Rb_element001  label="Rb_element : 1"  # scripted group (container) (typed FeaturePython)
  n = 1
  ref = Rb_element
FEATURE [App::DocumentObjectGroupPython] G4_Rb  # scripted group (container) (typed FeaturePython)
  Dunit = g/cm3
  Dvalue = 1.532
  Group = -> [Rb_element001]
  conduct = 2
  density = 1
  expand = 3
  formula = Rb
  name = G4_Rb
  specific = 4
FEATURE [App::DocumentObjectGroupPython] Sr_element001  label="Sr_element : 1"  # scripted group (container) (typed FeaturePython)
  n = 1
  ref = Sr_element
FEATURE [App::DocumentObjectGroupPython] G4_Sr  # scripted group (container) (typed FeaturePython)
  Dunit = g/cm3
  Dvalue = 2.54
  Group = -> [Sr_element001]
  conduct = 2
  density = 1
  expand = 3
  formula = Sr
  name = G4_Sr
  specific = 4
FEATURE [App::DocumentObjectGroupPython] Y_element001  label="Y_element : 1"  # scripted group (container) (typed FeaturePython)
  n = 1
  ref = Y_element
FEATURE [App::DocumentObjectGroupPython] G4_Y  # scripted group (container) (typed FeaturePython)
  Dunit = g/cm3
  Dvalue = 4.469
  Group = -> [Y_element001]
  conduct = 2
  density = 1
  expand = 3
  formula = Y
  name = G4_Y
  specific = 4
FEATURE [App::DocumentObjectGroupPython] Zr_element001  label="Zr_element : 1"  # scripted group (container) (typed FeaturePython)
  n = 1
  ref = Zr_element
FEATURE [App::DocumentObjectGroupPython] G4_Zr  # scripted group (container) (typed FeaturePython)
  Dunit = g/cm3
  Dvalue = 6.506
  Group = -> [Zr_element001]
  conduct = 2
  density = 1
  expand = 3
  formula = Zr
  name = G4_Zr
  specific = 4
FEATURE [App::DocumentObjectGroupPython] Nb_element001  label="Nb_element : 1"  # scripted group (container) (typed FeaturePython)
  n = 1
  ref = Nb_element
FEATURE [App::DocumentObjectGroupPython] G4_Nb  # scripted group (container) (typed FeaturePython)
  Dunit = g/cm3
  Dvalue = 8.57
  Group = -> [Nb_element001]
  conduct = 2
  density = 1
  expand = 3
  formula = Nb
  name = G4_Nb
  specific = 4
FEATURE [App::DocumentObjectGroupPython] Mo_element001  label="Mo_element : 1"  # scripted group (container) (typed FeaturePython)
  n = 1
  ref = Mo_element
FEATURE [App::DocumentObjectGroupPython] G4_Mo  # scripted group (container) (typed FeaturePython)
  Dunit = g/cm3
  Dvalue = 10.22
  Group = -> [Mo_element001]
  conduct = 2
  density = 1
  expand = 3
  formula = Mo
  name = G4_Mo
  specific = 4
FEATURE [App::DocumentObjectGroupPython] Tc_element001  label="Tc_element : 1"  # scripted group (container) (typed FeaturePython)
  n = 1
  ref = Tc_element
FEATURE [App::DocumentObjectGroupPython] G4_Tc  # scripted group (container) (typed FeaturePython)
  Dunit = g/cm3
  Dvalue = 11.5
  Group = -> [Tc_element001]
  conduct = 2
  density = 1
  expand = 3
  formula = Tc
  name = G4_Tc
  specific = 4
FEATURE [App::DocumentObjectGroupPython] Ru_element001  label="Ru_element : 1"  # scripted group (container) (typed FeaturePython)
  n = 1
  ref = Ru_element
FEATURE [App::DocumentObjectGroupPython] G4_Ru  # scripted group (container) (typed FeaturePython)
  Dunit = g/cm3
  Dvalue = 12.41
  Group = -> [Ru_element001]
  conduct = 2
  density = 1
  expand = 3
  formula = Ru
  name = G4_Ru
  specific = 4
FEATURE [App::DocumentObjectGroupPython] Rh_element001  label="Rh_element : 1"  # scripted group (container) (typed FeaturePython)
  n = 1
  ref = Rh_element
FEATURE [App::DocumentObjectGroupPython] G4_Rh  # scripted group (container) (typed FeaturePython)
  Dunit = g/cm3
  Dvalue = 12.41
  Group = -> [Rh_element001]
  conduct = 2
  density = 1
  expand = 3
  formula = Rh
  name = G4_Rh
  specific = 4
FEATURE [App::DocumentObjectGroupPython] Pd_element001  label="Pd_element : 1"  # scripted group (container) (typed FeaturePython)
  n = 1
  ref = Pd_element
FEATURE [App::DocumentObjectGroupPython] G4_Pd  # scripted group (container) (typed FeaturePython)
  Dunit = g/cm3
  Dvalue = 12.02
  Group = -> [Pd_element001]
  conduct = 2
  density = 1
  expand = 3
  formula = Pd
  name = G4_Pd
  specific = 4
FEATURE [App::DocumentObjectGroupPython] Ag_element006  label="Ag_element : 004"  # scripted group (container) (typed FeaturePython)
  n = 1
  ref = Ag_element
FEATURE [App::DocumentObjectGroupPython] G4_Ag  # scripted group (container) (typed FeaturePython)
  Dunit = g/cm3
  Dvalue = 10.5
  Group = -> [Ag_element006]
  conduct = 2
  density = 1
  expand = 3
  formula = Ag
  name = G4_Ag
  specific = 4
FEATURE [App::DocumentObjectGroupPython] Cd_element003  label="Cd_element : 003"  # scripted group (container) (typed FeaturePython)
  n = 1
  ref = Cd_element
FEATURE [App::DocumentObjectGroupPython] G4_Cd  # scripted group (container) (typed FeaturePython)
  Dunit = g/cm3
  Dvalue = 8.65
  Group = -> [Cd_element003]
  conduct = 2
  density = 1
  expand = 3
  formula = Cd
  name = G4_Cd
  specific = 4
FEATURE [App::DocumentObjectGroupPython] In_element001  label="In_element : 1"  # scripted group (container) (typed FeaturePython)
  n = 1
  ref = In_element
FEATURE [App::DocumentObjectGroupPython] G4_In  # scripted group (container) (typed FeaturePython)
  Dunit = g/cm3
  Dvalue = 7.31
  Group = -> [In_element001]
  conduct = 2
  density = 1
  expand = 3
  formula = In
  name = G4_In
  specific = 4
FEATURE [App::DocumentObjectGroupPython] Sn_element001  label="Sn_element : 1"  # scripted group (container) (typed FeaturePython)
  n = 1
  ref = Sn_element
FEATURE [App::DocumentObjectGroupPython] G4_Sn  # scripted group (container) (typed FeaturePython)
  Dunit = g/cm3
  Dvalue = 7.31
  Group = -> [Sn_element001]
  conduct = 2
  density = 1
  expand = 3
  formula = Sn
  name = G4_Sn
  specific = 4
FEATURE [App::DocumentObjectGroupPython] Sb_element001  label="Sb_element : 1"  # scripted group (container) (typed FeaturePython)
  n = 1
  ref = Sb_element
FEATURE [App::DocumentObjectGroupPython] G4_Sb  # scripted group (container) (typed FeaturePython)
  Dunit = g/cm3
  Dvalue = 6.691
  Group = -> [Sb_element001]
  conduct = 2
  density = 1
  expand = 3
  formula = Sb
  name = G4_Sb
  specific = 4
FEATURE [App::DocumentObjectGroupPython] Te_element002  label="Te_element : 002"  # scripted group (container) (typed FeaturePython)
  n = 1
  ref = Te_element
FEATURE [App::DocumentObjectGroupPython] G4_Te  # scripted group (container) (typed FeaturePython)
  Dunit = g/cm3
  Dvalue = 6.24
  Group = -> [Te_element002]
  conduct = 2
  density = 1
  expand = 3
  formula = Te
  name = G4_Te
  specific = 4
FEATURE [App::DocumentObjectGroupPython] I_element010  label="I_element : 006"  # scripted group (container) (typed FeaturePython)
  n = 1
  ref = I_element
FEATURE [App::DocumentObjectGroupPython] G4_I  # scripted group (container) (typed FeaturePython)
  Dunit = g/cm3
  Dvalue = 4.93
  Group = -> [I_element010]
  conduct = 2
  density = 1
  expand = 3
  formula = I
  name = G4_I
  specific = 4
FEATURE [App::DocumentObjectGroupPython] Xe_element001  label="Xe_element : 1"  # scripted group (container) (typed FeaturePython)
  n = 1
  ref = Xe_element
FEATURE [App::DocumentObjectGroupPython] G4_Xe  # scripted group (container) (typed FeaturePython)
  Dunit = g/cm3
  Dvalue = 0.00548536
  Group = -> [Xe_element001]
  conduct = 2
  density = 1
  expand = 3
  formula = Xe
  name = G4_Xe
  specific = 4
FEATURE [App::DocumentObjectGroupPython] Cs_element003  label="Cs_element : 003"  # scripted group (container) (typed FeaturePython)
  n = 1
  ref = Cs_element
FEATURE [App::DocumentObjectGroupPython] G4_Cs  # scripted group (container) (typed FeaturePython)
  Dunit = g/cm3
  Dvalue = 1.873
  Group = -> [Cs_element003]
  conduct = 2
  density = 1
  expand = 3
  formula = Cs
  name = G4_Cs
  specific = 4
FEATURE [App::DocumentObjectGroupPython] Ba_element003  label="Ba_element : 003"  # scripted group (container) (typed FeaturePython)
  n = 1
  ref = Ba_element
FEATURE [App::DocumentObjectGroupPython] G4_Ba  # scripted group (container) (typed FeaturePython)
  Dunit = g/cm3
  Dvalue = 3.5
  Group = -> [Ba_element003]
  conduct = 2
  density = 1
  expand = 3
  formula = Ba
  name = G4_Ba
  specific = 4
FEATURE [App::DocumentObjectGroupPython] La_element003  label="La_element : 003"  # scripted group (container) (typed FeaturePython)
  n = 1
  ref = La_element
FEATURE [App::DocumentObjectGroupPython] G4_La  # scripted group (container) (typed FeaturePython)
  Dunit = g/cm3
  Dvalue = 6.154
  Group = -> [La_element003]
  conduct = 2
  density = 1
  expand = 3
  formula = La
  name = G4_La
  specific = 4
FEATURE [App::DocumentObjectGroupPython] Ce_element002  label="Ce_element : 1"  # scripted group (container) (typed FeaturePython)
  n = 1
  ref = Ce_element
FEATURE [App::DocumentObjectGroupPython] G4_Ce  # scripted group (container) (typed FeaturePython)
  Dunit = g/cm3
  Dvalue = 6.657
  Group = -> [Ce_element002]
  conduct = 2
  density = 1
  expand = 3
  formula = Ce
  name = G4_Ce
  specific = 4
FEATURE [App::DocumentObjectGroupPython] Pr_element001  label="Pr_element : 1"  # scripted group (container) (typed FeaturePython)
  n = 1
  ref = Pr_element
FEATURE [App::DocumentObjectGroupPython] G4_Pr  # scripted group (container) (typed FeaturePython)
  Dunit = g/cm3
  Dvalue = 6.71
  Group = -> [Pr_element001]
  conduct = 2
  density = 1
  expand = 3
  formula = Pr
  name = G4_Pr
  specific = 4
FEATURE [App::DocumentObjectGroupPython] Nd_element001  label="Nd_element : 1"  # scripted group (container) (typed FeaturePython)
  n = 1
  ref = Nd_element
FEATURE [App::DocumentObjectGroupPython] G4_Nd  # scripted group (container) (typed FeaturePython)
  Dunit = g/cm3
  Dvalue = 6.9
  Group = -> [Nd_element001]
  conduct = 2
  density = 1
  expand = 3
  formula = Nd
  name = G4_Nd
  specific = 4
FEATURE [App::DocumentObjectGroupPython] Pm_element001  label="Pm_element : 1"  # scripted group (container) (typed FeaturePython)
  n = 1
  ref = Pm_element
FEATURE [App::DocumentObjectGroupPython] G4_Pm  # scripted group (container) (typed FeaturePython)
  Dunit = g/cm3
  Dvalue = 7.22
  Group = -> [Pm_element001]
  conduct = 2
  density = 1
  expand = 3
  formula = Pm
  name = G4_Pm
  specific = 4
FEATURE [App::DocumentObjectGroupPython] Sm_element001  label="Sm_element : 1"  # scripted group (container) (typed FeaturePython)
  n = 1
  ref = Sm_element
FEATURE [App::DocumentObjectGroupPython] G4_Sm  # scripted group (container) (typed FeaturePython)
  Dunit = g/cm3
  Dvalue = 7.46
  Group = -> [Sm_element001]
  conduct = 2
  density = 1
  expand = 3
  formula = Sm
  name = G4_Sm
  specific = 4
FEATURE [App::DocumentObjectGroupPython] Eu_element001  label="Eu_element : 1"  # scripted group (container) (typed FeaturePython)
  n = 1
  ref = Eu_element
FEATURE [App::DocumentObjectGroupPython] G4_Eu  # scripted group (container) (typed FeaturePython)
  Dunit = g/cm3
  Dvalue = 5.243
  Group = -> [Eu_element001]
  conduct = 2
  density = 1
  expand = 3
  formula = Eu
  name = G4_Eu
  specific = 4
FEATURE [App::DocumentObjectGroupPython] Gd_element002  label="Gd_element : 1"  # scripted group (container) (typed FeaturePython)
  n = 1
  ref = Gd_element
FEATURE [App::DocumentObjectGroupPython] G4_Gd  # scripted group (container) (typed FeaturePython)
  Dunit = g/cm3
  Dvalue = 7.9004
  Group = -> [Gd_element002]
  conduct = 2
  density = 1
  expand = 3
  formula = Gd
  name = G4_Gd
  specific = 4
FEATURE [App::DocumentObjectGroupPython] Tb_element001  label="Tb_element : 1"  # scripted group (container) (typed FeaturePython)
  n = 1
  ref = Tb_element
FEATURE [App::DocumentObjectGroupPython] G4_Tb  # scripted group (container) (typed FeaturePython)
  Dunit = g/cm3
  Dvalue = 8.229
  Group = -> [Tb_element001]
  conduct = 2
  density = 1
  expand = 3
  formula = Tb
  name = G4_Tb
  specific = 4
FEATURE [App::DocumentObjectGroupPython] Dy_element001  label="Dy_element : 1"  # scripted group (container) (typed FeaturePython)
  n = 1
  ref = Dy_element
FEATURE [App::DocumentObjectGroupPython] G4_Dy  # scripted group (container) (typed FeaturePython)
  Dunit = g/cm3
  Dvalue = 8.55
  Group = -> [Dy_element001]
  conduct = 2
  density = 1
  expand = 3
  formula = Dy
  name = G4_Dy
  specific = 4
FEATURE [App::DocumentObjectGroupPython] Ho_element001  label="Ho_element : 1"  # scripted group (container) (typed FeaturePython)
  n = 1
  ref = Ho_element
FEATURE [App::DocumentObjectGroupPython] G4_Ho  # scripted group (container) (typed FeaturePython)
  Dunit = g/cm3
  Dvalue = 8.795
  Group = -> [Ho_element001]
  conduct = 2
  density = 1
  expand = 3
  formula = Ho
  name = G4_Ho
  specific = 4
FEATURE [App::DocumentObjectGroupPython] Er_element001  label="Er_element : 1"  # scripted group (container) (typed FeaturePython)
  n = 1
  ref = Er_element
FEATURE [App::DocumentObjectGroupPython] G4_Er  # scripted group (container) (typed FeaturePython)
  Dunit = g/cm3
  Dvalue = 9.066
  Group = -> [Er_element001]
  conduct = 2
  density = 1
  expand = 3
  formula = Er
  name = G4_Er
  specific = 4
FEATURE [App::DocumentObjectGroupPython] Tm_element001  label="Tm_element : 1"  # scripted group (container) (typed FeaturePython)
  n = 1
  ref = Tm_element
FEATURE [App::DocumentObjectGroupPython] G4_Tm  # scripted group (container) (typed FeaturePython)
  Dunit = g/cm3
  Dvalue = 9.321
  Group = -> [Tm_element001]
  conduct = 2
  density = 1
  expand = 3
  formula = Tm
  name = G4_Tm
  specific = 4
FEATURE [App::DocumentObjectGroupPython] Yb_element001  label="Yb_element : 1"  # scripted group (container) (typed FeaturePython)
  n = 1
  ref = Yb_element
FEATURE [App::DocumentObjectGroupPython] G4_Yb  # scripted group (container) (typed FeaturePython)
  Dunit = g/cm3
  Dvalue = 6.73
  Group = -> [Yb_element001]
  conduct = 2
  density = 1
  expand = 3
  formula = Yb
  name = G4_Yb
  specific = 4
FEATURE [App::DocumentObjectGroupPython] Lu_element001  label="Lu_element : 1"  # scripted group (container) (typed FeaturePython)
  n = 1
  ref = Lu_element
FEATURE [App::DocumentObjectGroupPython] G4_Lu  # scripted group (container) (typed FeaturePython)
  Dunit = g/cm3
  Dvalue = 9.84
  Group = -> [Lu_element001]
  conduct = 2
  density = 1
  expand = 3
  formula = Lu
  name = G4_Lu
  specific = 4
FEATURE [App::DocumentObjectGroupPython] Hf_element001  label="Hf_element : 1"  # scripted group (container) (typed FeaturePython)
  n = 1
  ref = Hf_element
FEATURE [App::DocumentObjectGroupPython] G4_Hf  # scripted group (container) (typed FeaturePython)
  Dunit = g/cm3
  Dvalue = 13.31
  Group = -> [Hf_element001]
  conduct = 2
  density = 1
  expand = 3
  formula = Hf
  name = G4_Hf
  specific = 4
FEATURE [App::DocumentObjectGroupPython] Ta_element001  label="Ta_element : 1"  # scripted group (container) (typed FeaturePython)
  n = 1
  ref = Ta_element
FEATURE [App::DocumentObjectGroupPython] G4_Ta  # scripted group (container) (typed FeaturePython)
  Dunit = g/cm3
  Dvalue = 16.654
  Group = -> [Ta_element001]
  conduct = 2
  density = 1
  expand = 3
  formula = Ta
  name = G4_Ta
  specific = 4
FEATURE [App::DocumentObjectGroupPython] W_element004  label="W_element : 004"  # scripted group (container) (typed FeaturePython)
  n = 1
  ref = W_element
FEATURE [App::DocumentObjectGroupPython] G4_W  # scripted group (container) (typed FeaturePython)
  Dunit = g/cm3
  Dvalue = 19.3
  Group = -> [W_element004]
  conduct = 2
  density = 1
  expand = 3
  formula = W
  name = G4_W
  specific = 4
FEATURE [App::DocumentObjectGroupPython] Re_element001  label="Re_element : 1"  # scripted group (container) (typed FeaturePython)
  n = 1
  ref = Re_element
FEATURE [App::DocumentObjectGroupPython] G4_Re  # scripted group (container) (typed FeaturePython)
  Dunit = g/cm3
  Dvalue = 21.02
  Group = -> [Re_element001]
  conduct = 2
  density = 1
  expand = 3
  formula = Re
  name = G4_Re
  specific = 4
FEATURE [App::DocumentObjectGroupPython] Os_element001  label="Os_element : 1"  # scripted group (container) (typed FeaturePython)
  n = 1
  ref = Os_element
FEATURE [App::DocumentObjectGroupPython] G4_Os  # scripted group (container) (typed FeaturePython)
  Dunit = g/cm3
  Dvalue = 22.57
  Group = -> [Os_element001]
  conduct = 2
  density = 1
  expand = 3
  formula = Os
  name = G4_Os
  specific = 4
FEATURE [App::DocumentObjectGroupPython] Ir_element001  label="Ir_element : 1"  # scripted group (container) (typed FeaturePython)
  n = 1
  ref = Ir_element
FEATURE [App::DocumentObjectGroupPython] G4_Ir  # scripted group (container) (typed FeaturePython)
  Dunit = g/cm3
  Dvalue = 22.42
  Group = -> [Ir_element001]
  conduct = 2
  density = 1
  expand = 3
  formula = Ir
  name = G4_Ir
  specific = 4
FEATURE [App::DocumentObjectGroupPython] Pt_element001  label="Pt_element : 1"  # scripted group (container) (typed FeaturePython)
  n = 1
  ref = Pt_element
FEATURE [App::DocumentObjectGroupPython] G4_Pt  # scripted group (container) (typed FeaturePython)
  Dunit = g/cm3
  Dvalue = 21.45
  Group = -> [Pt_element001]
  conduct = 2
  density = 1
  expand = 3
  formula = Pt
  name = G4_Pt
  specific = 4
FEATURE [App::DocumentObjectGroupPython] Au_element001  label="Au_element : 1"  # scripted group (container) (typed FeaturePython)
  n = 1
  ref = Au_element
FEATURE [App::DocumentObjectGroupPython] G4_Au  # scripted group (container) (typed FeaturePython)
  Dunit = g/cm3
  Dvalue = 19.32
  Group = -> [Au_element001]
  conduct = 2
  density = 1
  expand = 3
  formula = Au
  name = G4_Au
  specific = 4
FEATURE [App::DocumentObjectGroupPython] Hg_element002  label="Hg_element : 002"  # scripted group (container) (typed FeaturePython)
  n = 1
  ref = Hg_element
FEATURE [App::DocumentObjectGroupPython] G4_Hg  # scripted group (container) (typed FeaturePython)
  Dunit = g/cm3
  Dvalue = 13.546
  Group = -> [Hg_element002]
  conduct = 2
  density = 1
  expand = 3
  formula = Hg
  name = G4_Hg
  specific = 4
FEATURE [App::DocumentObjectGroupPython] Tl_element002  label="Tl_element : 002"  # scripted group (container) (typed FeaturePython)
  n = 1
  ref = Tl_element
FEATURE [App::DocumentObjectGroupPython] G4_Tl  # scripted group (container) (typed FeaturePython)
  Dunit = g/cm3
  Dvalue = 11.72
  Group = -> [Tl_element002]
  conduct = 2
  density = 1
  expand = 3
  formula = Tl
  name = G4_Tl
  specific = 4
FEATURE [App::DocumentObjectGroupPython] Pb_element003  label="Pb_element : 1"  # scripted group (container) (typed FeaturePython)
  n = 1
  ref = Pb_element
FEATURE [App::DocumentObjectGroupPython] G4_Pb  # scripted group (container) (typed FeaturePython)
  Dunit = g/cm3
  Dvalue = 11.35
  Group = -> [Pb_element003]
  conduct = 2
  density = 1
  expand = 3
  formula = Pb
  name = G4_Pb
  specific = 4
FEATURE [App::DocumentObjectGroupPython] Bi_element002  label="Bi_element : 1"  # scripted group (container) (typed FeaturePython)
  n = 1
  ref = Bi_element
FEATURE [App::DocumentObjectGroupPython] G4_Bi  # scripted group (container) (typed FeaturePython)
  Dunit = g/cm3
  Dvalue = 9.747
  Group = -> [Bi_element002]
  conduct = 2
  density = 1
  expand = 3
  formula = Bi
  name = G4_Bi
  specific = 4
FEATURE [App::DocumentObjectGroupPython] Po_element001  label="Po_element : 1"  # scripted group (container) (typed FeaturePython)
  n = 1
  ref = Po_element
FEATURE [App::DocumentObjectGroupPython] G4_Po  # scripted group (container) (typed FeaturePython)
  Dunit = g/cm3
  Dvalue = 9.32
  Group = -> [Po_element001]
  conduct = 2
  density = 1
  expand = 3
  formula = Po
  name = G4_Po
  specific = 4
FEATURE [App::DocumentObjectGroupPython] At_element001  label="At_element : 1"  # scripted group (container) (typed FeaturePython)
  n = 1
  ref = At_element
FEATURE [App::DocumentObjectGroupPython] G4_At  # scripted group (container) (typed FeaturePython)
  Dunit = g/cm3
  Dvalue = 9.32
  Group = -> [At_element001]
  conduct = 2
  density = 1
  expand = 3
  formula = At
  name = G4_At
  specific = 4
FEATURE [App::DocumentObjectGroupPython] Rn_element001  label="Rn_element : 1"  # scripted group (container) (typed FeaturePython)
  n = 1
  ref = Rn_element
FEATURE [App::DocumentObjectGroupPython] G4_Rn  # scripted group (container) (typed FeaturePython)
  Dunit = g/cm3
  Dvalue = 0.00900662
  Group = -> [Rn_element001]
  conduct = 2
  density = 1
  expand = 3
  formula = Rn
  name = G4_Rn
  specific = 4
FEATURE [App::DocumentObjectGroupPython] Fr_element001  label="Fr_element : 1"  # scripted group (container) (typed FeaturePython)
  n = 1
  ref = Fr_element
FEATURE [App::DocumentObjectGroupPython] G4_Fr  # scripted group (container) (typed FeaturePython)
  Dunit = g/cm3
  Dvalue = 1
  Group = -> [Fr_element001]
  conduct = 2
  density = 1
  expand = 3
  formula = Fr
  name = G4_Fr
  specific = 4
FEATURE [App::DocumentObjectGroupPython] Ra_element001  label="Ra_element : 1"  # scripted group (container) (typed FeaturePython)
  n = 1
  ref = Ra_element
FEATURE [App::DocumentObjectGroupPython] G4_Ra  # scripted group (container) (typed FeaturePython)
  Dunit = g/cm3
  Dvalue = 5
  Group = -> [Ra_element001]
  conduct = 2
  density = 1
  expand = 3
  formula = Ra
  name = G4_Ra
  specific = 4
FEATURE [App::DocumentObjectGroupPython] Ac_element001  label="Ac_element : 1"  # scripted group (container) (typed FeaturePython)
  n = 1
  ref = Ac_element
FEATURE [App::DocumentObjectGroupPython] G4_Ac  # scripted group (container) (typed FeaturePython)
  Dunit = g/cm3
  Dvalue = 10.07
  Group = -> [Ac_element001]
  conduct = 2
  density = 1
  expand = 3
  formula = Ac
  name = G4_Ac
  specific = 4
FEATURE [App::DocumentObjectGroupPython] Th_element001  label="Th_element : 1"  # scripted group (container) (typed FeaturePython)
  n = 1
  ref = Th_element
FEATURE [App::DocumentObjectGroupPython] G4_Th  # scripted group (container) (typed FeaturePython)
  Dunit = g/cm3
  Dvalue = 11.72
  Group = -> [Th_element001]
  conduct = 2
  density = 1
  expand = 3
  formula = Th
  name = G4_Th
  specific = 4
FEATURE [App::DocumentObjectGroupPython] Pa_element001  label="Pa_element : 1"  # scripted group (container) (typed FeaturePython)
  n = 1
  ref = Pa_element
FEATURE [App::DocumentObjectGroupPython] G4_Pa  # scripted group (container) (typed FeaturePython)
  Dunit = g/cm3
  Dvalue = 15.37
  Group = -> [Pa_element001]
  conduct = 2
  density = 1
  expand = 3
  formula = Pa
  name = G4_Pa
  specific = 4
FEATURE [App::DocumentObjectGroupPython] U_element004  label="U_element : 004"  # scripted group (container) (typed FeaturePython)
  n = 1
  ref = U_element
FEATURE [App::DocumentObjectGroupPython] G4_U  # scripted group (container) (typed FeaturePython)
  Dunit = g/cm3
  Dvalue = 18.95
  Group = -> [U_element004]
  conduct = 2
  density = 1
  expand = 3
  formula = U
  name = G4_U
  specific = 4
FEATURE [App::DocumentObjectGroupPython] Np_element001  label="Np_element : 1"  # scripted group (container) (typed FeaturePython)
  n = 1
  ref = Np_element
FEATURE [App::DocumentObjectGroupPython] G4_Np  # scripted group (container) (typed FeaturePython)
  Dunit = g/cm3
  Dvalue = 20.25
  Group = -> [Np_element001]
  conduct = 2
  density = 1
  expand = 3
  formula = Np
  name = G4_Np
  specific = 4
FEATURE [App::DocumentObjectGroupPython] Pu_element002  label="Pu_element : 002"  # scripted group (container) (typed FeaturePython)
  n = 1
  ref = Pu_element
FEATURE [App::DocumentObjectGroupPython] G4_Pu  # scripted group (container) (typed FeaturePython)
  Dunit = g/cm3
  Dvalue = 19.84
  Group = -> [Pu_element002]
  conduct = 2
  density = 1
  expand = 3
  formula = Pu
  name = G4_Pu
  specific = 4
FEATURE [App::DocumentObjectGroupPython] Am_element001  label="Am_element : 1"  # scripted group (container) (typed FeaturePython)
  n = 1
  ref = Am_element
FEATURE [App::DocumentObjectGroupPython] G4_Am  # scripted group (container) (typed FeaturePython)
  Dunit = g/cm3
  Dvalue = 13.67
  Group = -> [Am_element001]
  conduct = 2
  density = 1
  expand = 3
  formula = Am
  name = G4_Am
  specific = 4
FEATURE [App::DocumentObjectGroupPython] Cm_element001  label="Cm_element : 1"  # scripted group (container) (typed FeaturePython)
  n = 1
  ref = Cm_element
FEATURE [App::DocumentObjectGroupPython] G4_Cm  # scripted group (container) (typed FeaturePython)
  Dunit = g/cm3
  Dvalue = 13.51
  Group = -> [Cm_element001]
  conduct = 2
  density = 1
  expand = 3
  formula = Cm
  name = G4_Cm
  specific = 4
FEATURE [App::DocumentObjectGroupPython] Bk_element001  label="Bk_element : 1"  # scripted group (container) (typed FeaturePython)
  n = 1
  ref = Bk_element
FEATURE [App::DocumentObjectGroupPython] G4_Bk  # scripted group (container) (typed FeaturePython)
  Dunit = g/cm3
  Dvalue = 14
  Group = -> [Bk_element001]
  conduct = 2
  density = 1
  expand = 3
  formula = Bk
  name = G4_Bk
  specific = 4
FEATURE [App::DocumentObjectGroupPython] Cf_element001  label="Cf_element : 1"  # scripted group (container) (typed FeaturePython)
  n = 1
  ref = Cf_element
FEATURE [App::DocumentObjectGroupPython] G4_Cf  # scripted group (container) (typed FeaturePython)
  Dunit = g/cm3
  Dvalue = 10
  Group = -> [Cf_element001]
  conduct = 2
  density = 1
  expand = 3
  formula = Cf
  name = G4_Cf
  specific = 4
FEATURE [App::DocumentObjectGroupPython] Element  # scripted group (container) (typed FeaturePython)
  Group = -> [G4_H,G4_He,G4_Li,G4_Be,G4_B,G4_C,G4_N,G4_O,G4_F,G4_Ne,G4_Na,G4_Mg,G4_Al,G4_Si,G4_P,G4_S,G4_Cl,G4_Ar,G4_K,G4_Ca,G4_Sc,G4_Ti,G4_V,G4_Cr,G4_Mn,G4_Fe,G4_Co,G4_Ni,G4_Cu,G4_Zn,G4_Ga,G4_Ge,G4_As,G4_Se,G4_Br,G4_Kr,G4_Rb,G4_Sr,G4_Y,G4_Zr,G4_Nb,G4_Mo,G4_Tc,G4_Ru,G4_Rh,G4_Pd,G4_Ag,G4_Cd,G4_In,G4_Sn,G4_Sb,G4_Te,G4_I,G4_Xe,G4_Cs,G4_Ba,G4_La,G4_Ce,G4_Pr,G4_Nd,G4_Pm,G4_Sm,G4_Eu,G4_Gd,G4_Tb,G4_Dy,G4_Ho,G4_Er,+30 more]
FEATURE [App::DocumentObjectGroupPython] H_element114  label="H_element : 063"  # scripted group (container) (typed FeaturePython)
  n = 2
  ref = H_element
FEATURE [App::DocumentObjectGroupPython] G4_lH2  # scripted group (container) (typed FeaturePython)
  Dunit = g/cm3
  Dvalue = 0.0708
  Group = -> [H_element114]
  conduct = 2
  density = 1
  expand = 3
  formula = G4_lH2
  name = G4_lH2
  specific = 4
FEATURE [App::DocumentObjectGroupPython] N_element049  label="N_element : 022"  # scripted group (container) (typed FeaturePython)
  n = 2
  ref = N_element
FEATURE [App::DocumentObjectGroupPython] G4_lN2  # scripted group (container) (typed FeaturePython)
  Dunit = g/cm3
  Dvalue = 0.807
  Group = -> [N_element049]
  conduct = 2
  density = 1
  expand = 3
  formula = G4_lN2
  name = G4_lN2
  specific = 4
FEATURE [App::DocumentObjectGroupPython] O_element106  label="O_element : 060"  # scripted group (container) (typed FeaturePython)
  n = 2
  ref = O_element
FEATURE [App::DocumentObjectGroupPython] G4_lO2  # scripted group (container) (typed FeaturePython)
  Dunit = g/cm3
  Dvalue = 1.141
  Group = -> [O_element106]
  conduct = 2
  density = 1
  expand = 3
  formula = G4_lO2
  name = G4_lO2
  specific = 4
FEATURE [App::DocumentObjectGroupPython] Ar  label="Ar : 1"  # scripted group (container) (typed FeaturePython)
  n = 1
  ref = Ar
FEATURE [App::DocumentObjectGroupPython] G4_lAr  # scripted group (container) (typed FeaturePython)
  Dunit = g/cm3
  Dvalue = 1.396
  Group = -> [Ar]
  conduct = 2
  density = 1
  expand = 3
  formula = G4_lAr
  name = G4_lAr
  specific = 4
FEATURE [App::DocumentObjectGroupPython] Br  label="Br : 1"  # scripted group (container) (typed FeaturePython)
  n = 1
  ref = Br
FEATURE [App::DocumentObjectGroupPython] G4_lBr  # scripted group (container) (typed FeaturePython)
  Dunit = g/cm3
  Dvalue = 3.1028
  Group = -> [Br]
  conduct = 2
  density = 1
  expand = 3
  formula = G4_lBr
  name = G4_lBr
  specific = 4
FEATURE [App::DocumentObjectGroupPython] Kr  label="Kr : 1"  # scripted group (container) (typed FeaturePython)
  n = 1
  ref = Kr
FEATURE [App::DocumentObjectGroupPython] G4_lKr  # scripted group (container) (typed FeaturePython)
  Dunit = g/cm3
  Dvalue = 2.418
  Group = -> [Kr]
  conduct = 2
  density = 1
  expand = 3
  formula = G4_lKr
  name = G4_lKr
  specific = 4
FEATURE [App::DocumentObjectGroupPython] Xe  label="Xe : 1"  # scripted group (container) (typed FeaturePython)
  n = 1
  ref = Xe
FEATURE [App::DocumentObjectGroupPython] G4_lXe  # scripted group (container) (typed FeaturePython)
  Dunit = g/cm3
  Dvalue = 2.953
  Group = -> [Xe]
  conduct = 2
  density = 1
  expand = 3
  formula = G4_lXe
  name = G4_lXe
  specific = 4
FEATURE [App::DocumentObjectGroupPython] O_element107  label="O_element : 061"  # scripted group (container) (typed FeaturePython)
  n = 4
  ref = O_element
FEATURE [App::DocumentObjectGroupPython] Pb_element004  label="Pb_element : 002"  # scripted group (container) (typed FeaturePython)
  n = 1
  ref = Pb_element
FEATURE [App::DocumentObjectGroupPython] W_element005  label="W_element : 005"  # scripted group (container) (typed FeaturePython)
  n = 1
  ref = W_element
FEATURE [App::DocumentObjectGroupPython] G4_PbWO4  # scripted group (container) (typed FeaturePython)
  Dunit = g/cm3
  Dvalue = 8.28
  Group = -> [O_element107,Pb_element004,W_element005]
  conduct = 2
  density = 1
  expand = 3
  formula = G4_PbWO4
  name = G4_PbWO4
  specific = 4
FEATURE [App::DocumentObjectGroupPython] alactic  label="alactic : 1"  # scripted group (container) (typed FeaturePython)
  n = 1
  ref = alactic
FEATURE [App::DocumentObjectGroupPython] G4_Galactic  # scripted group (container) (typed FeaturePython)
  Dunit = g/cm3
  Dvalue = 0
  Group = -> [alactic]
  conduct = 2
  density = 1
  expand = 3
  formula = G4_Galactic
  name = G4_Galactic
  specific = 4
FEATURE [App::DocumentObjectGroupPython] RAPHITE_POROUS  label="RAPHITE_POROUS : 1"  # scripted group (container) (typed FeaturePython)
  n = 1
  ref = RAPHITE_POROUS
FEATURE [App::DocumentObjectGroupPython] G4_GRAPHITE_POROUS  # scripted group (container) (typed FeaturePython)
  Dunit = g/cm3
  Dvalue = 1.7
  Group = -> [RAPHITE_POROUS]
  conduct = 2
  density = 1
  expand = 3
  formula = G4_GRAPHITE_POROUS
  name = G4_GRAPHITE_POROUS
  specific = 4
FEATURE [App::DocumentObjectGroupPython] H_element115  label="H_element : 0.150"  # scripted group (container) (typed FeaturePython)
  n = 0.080538
FEATURE [App::DocumentObjectGroupPython] C_element125  label="C_element : 0.600"  # scripted group (container) (typed FeaturePython)
  n = 0.599848
FEATURE [App::DocumentObjectGroupPython] O_element108  label="O_element : 0.320"  # scripted group (container) (typed FeaturePython)
  n = 0.319614
FEATURE [App::DocumentObjectGroupPython] G4_LUCITE  # scripted group (container) (typed FeaturePython)
  Dunit = g/cm3
  Dvalue = 1.19
  Group = -> [H_element115,C_element125,O_element108]
  conduct = 2
  density = 1
  expand = 3
  formula = G4_LUCITE
  name = G4_LUCITE
  specific = 4
FEATURE [App::DocumentObjectGroupPython] Cu_element002  label="Cu_element : 62"  # scripted group (container) (typed FeaturePython)
  n = 62
  ref = Cu_element
FEATURE [App::DocumentObjectGroupPython] Zn_element002  label="Zn_element : 35"  # scripted group (container) (typed FeaturePython)
  n = 35
  ref = Zn_element
FEATURE [App::DocumentObjectGroupPython] Pb_element005  label="Pb_element : 3"  # scripted group (container) (typed FeaturePython)
  n = 3
  ref = Pb_element
FEATURE [App::DocumentObjectGroupPython] G4_BRASS  # scripted group (container) (typed FeaturePython)
  Dunit = g/cm3
  Dvalue = 8.52
  Group = -> [Cu_element002,Zn_element002,Pb_element005]
  conduct = 2
  density = 1
  expand = 3
  formula = G4_BRASS
  name = G4_BRASS
  specific = 4
FEATURE [App::DocumentObjectGroupPython] Cu_element003  label="Cu_element : 89"  # scripted group (container) (typed FeaturePython)
  n = 89
  ref = Cu_element
FEATURE [App::DocumentObjectGroupPython] Zn_element003  label="Zn_element : 9"  # scripted group (container) (typed FeaturePython)
  n = 9
  ref = Zn_element
FEATURE [App::DocumentObjectGroupPython] Pb_element006  label="Pb_element : 2"  # scripted group (container) (typed FeaturePython)
  n = 2
  ref = Pb_element
FEATURE [App::DocumentObjectGroupPython] G4_BRONZE  # scripted group (container) (typed FeaturePython)
  Dunit = g/cm3
  Dvalue = 8.82
  Group = -> [Cu_element003,Zn_element003,Pb_element006]
  conduct = 2
  density = 1
  expand = 3
  formula = G4_BRONZE
  name = G4_BRONZE
  specific = 4
FEATURE [App::DocumentObjectGroupPython] Fe_element008  label="Fe_element : 74"  # scripted group (container) (typed FeaturePython)
  n = 74
  ref = Fe_element
FEATURE [App::DocumentObjectGroupPython] Cr_element002  label="Cr_element : 18"  # scripted group (container) (typed FeaturePython)
  n = 18
  ref = Cr_element
FEATURE [App::DocumentObjectGroupPython] Ni_element002  label="Ni_element : 8"  # scripted group (container) (typed FeaturePython)
  n = 8
  ref = Ni_element
FEATURE [App::DocumentObjectGroupPython] G4_STAINLESS_STEEL  label="G4_STAINLESS-STEEL"  # scripted group (container) (typed FeaturePython)
  Dunit = g/cm3
  Dvalue = 8
  Group = -> [Fe_element008,Cr_element002,Ni_element002]
  conduct = 2
  density = 1
  expand = 3
  formula = G4_STAINLESS-STEEL
  name = G4_STAINLESS-STEEL
  specific = 4
FEATURE [App::DocumentObjectGroupPython] H_element116  label="H_element : 064"  # scripted group (container) (typed FeaturePython)
  n = 18
  ref = H_element
FEATURE [App::DocumentObjectGroupPython] C_element126  label="C_element : 071"  # scripted group (container) (typed FeaturePython)
  n = 12
  ref = C_element
FEATURE [App::DocumentObjectGroupPython] O_element109  label="O_element : 062"  # scripted group (container) (typed FeaturePython)
  n = 7
  ref = O_element
FEATURE [App::DocumentObjectGroupPython] G4_CR39  # scripted group (container) (typed FeaturePython)
  Dunit = g/cm3
  Dvalue = 1.32
  Group = -> [H_element116,C_element126,O_element109]
  conduct = 2
  density = 1
  expand = 3
  formula = G4_CR39
  name = G4_CR39
  specific = 4
FEATURE [App::DocumentObjectGroupPython] H_element117  label="H_element : 38"  # scripted group (container) (typed FeaturePython)
  n = 38
  ref = H_element
FEATURE [App::DocumentObjectGroupPython] C_element127  label="C_element : 072"  # scripted group (container) (typed FeaturePython)
  n = 18
  ref = C_element
FEATURE [App::DocumentObjectGroupPython] O_element110  label="O_element : 063"  # scripted group (container) (typed FeaturePython)
  n = 1
  ref = O_element
FEATURE [App::DocumentObjectGroupPython] G4_OCTADECANOL  # scripted group (container) (typed FeaturePython)
  Dunit = g/cm3
  Dvalue = 0.812
  Group = -> [H_element117,C_element127,O_element110]
  conduct = 2
  density = 1
  expand = 3
  formula = G4_OCTADECANOL
  name = G4_OCTADECANOL
  specific = 4
FEATURE [App::DocumentObjectGroupPython] HEP  # scripted group (container) (typed FeaturePython)
  Group = -> [G4_lH2,G4_lN2,G4_lO2,G4_lAr,G4_lBr,G4_lKr,G4_lXe,G4_PbWO4,G4_Galactic,G4_GRAPHITE_POROUS,G4_LUCITE,G4_BRASS,G4_BRONZE,G4_STAINLESS_STEEL,G4_CR39,G4_OCTADECANOL]
FEATURE [App::DocumentObjectGroupPython] C_element128  label="C_element : 073"  # scripted group (container) (typed FeaturePython)
  n = 14
  ref = C_element
FEATURE [App::DocumentObjectGroupPython] H_element118  label="H_element : 065"  # scripted group (container) (typed FeaturePython)
  n = 10
  ref = H_element
FEATURE [App::DocumentObjectGroupPython] O_element111  label="O_element : 064"  # scripted group (container) (typed FeaturePython)
  n = 2
  ref = O_element
FEATURE [App::DocumentObjectGroupPython] N_element050  label="N_element : 023"  # scripted group (container) (typed FeaturePython)
  n = 2
  ref = N_element
FEATURE [App::DocumentObjectGroupPython] G4_KEVLAR  # scripted group (container) (typed FeaturePython)
  Dunit = g/cm3
  Dvalue = 1.44
  Group = -> [C_element128,H_element118,O_element111,N_element050]
  conduct = 2
  density = 1
  expand = 3
  formula = G4_KEVLAR
  name = G4_KEVLAR
  specific = 4
FEATURE [App::DocumentObjectGroupPython] C_element129  label="C_element : 074"  # scripted group (container) (typed FeaturePython)
  n = 10
  ref = C_element
FEATURE [App::DocumentObjectGroupPython] H_element119  label="H_element : 066"  # scripted group (container) (typed FeaturePython)
  n = 8
  ref = H_element
FEATURE [App::DocumentObjectGroupPython] O_element112  label="O_element : 065"  # scripted group (container) (typed FeaturePython)
  n = 4
  ref = O_element
FEATURE [App::DocumentObjectGroupPython] G4_DACRON  # scripted group (container) (typed FeaturePython)
  Dunit = g/cm3
  Dvalue = 1.4
  Group = -> [C_element129,H_element119,O_element112]
  conduct = 2
  density = 1
  expand = 3
  formula = G4_DACRON
  name = G4_DACRON
  specific = 4
FEATURE [App::DocumentObjectGroupPython] C_element130  label="C_element : 075"  # scripted group (container) (typed FeaturePython)
  n = 4
  ref = C_element
FEATURE [App::DocumentObjectGroupPython] H_element120  label="H_element : 067"  # scripted group (container) (typed FeaturePython)
  n = 5
  ref = H_element
FEATURE [App::DocumentObjectGroupPython] Cl_element030  label="Cl_element : 016"  # scripted group (container) (typed FeaturePython)
  n = 1
  ref = Cl_element
FEATURE [App::DocumentObjectGroupPython] G4_NEOPRENE  # scripted group (container) (typed FeaturePython)
  Dunit = g/cm3
  Dvalue = 1.23
  Group = -> [C_element130,H_element120,Cl_element030]
  conduct = 2
  density = 1
  expand = 3
  formula = G4_NEOPRENE
  name = G4_NEOPRENE
  specific = 4
FEATURE [App::DocumentObjectGroupPython] Space  # scripted group (container) (typed FeaturePython)
  Group = -> [G4_KEVLAR,G4_DACRON,G4_NEOPRENE]
FEATURE [App::DocumentObjectGroupPython] H_element121  label="H_element : 068"  # scripted group (container) (typed FeaturePython)
  n = 5
  ref = H_element
FEATURE [App::DocumentObjectGroupPython] C_element131  label="C_element : 076"  # scripted group (container) (typed FeaturePython)
  n = 4
  ref = C_element
FEATURE [App::DocumentObjectGroupPython] N_element051  label="N_element : 3"  # scripted group (container) (typed FeaturePython)
  n = 3
  ref = N_element
FEATURE [App::DocumentObjectGroupPython] O_element113  label="O_element : 066"  # scripted group (container) (typed FeaturePython)
  n = 1
  ref = O_element
FEATURE [App::DocumentObjectGroupPython] G4_CYTOSINE  # scripted group (container) (typed FeaturePython)
  Dunit = g/cm3
  Dvalue = 1.55
  Group = -> [H_element121,C_element131,N_element051,O_element113]
  conduct = 2
  density = 1
  expand = 3
  formula = G4_CYTOSINE
  name = G4_CYTOSINE
  specific = 4
FEATURE [App::DocumentObjectGroupPython] H_element122  label="H_element : 069"  # scripted group (container) (typed FeaturePython)
  n = 6
  ref = H_element
FEATURE [App::DocumentObjectGroupPython] C_element132  label="C_element : 077"  # scripted group (container) (typed FeaturePython)
  n = 5
  ref = C_element
FEATURE [App::DocumentObjectGroupPython] N_element052  label="N_element : 024"  # scripted group (container) (typed FeaturePython)
  n = 2
  ref = N_element
FEATURE [App::DocumentObjectGroupPython] O_element114  label="O_element : 067"  # scripted group (container) (typed FeaturePython)
  n = 2
  ref = O_element
FEATURE [App::DocumentObjectGroupPython] G4_THYMINE  # scripted group (container) (typed FeaturePython)
  Dunit = g/cm3
  Dvalue = 1.23
  Group = -> [H_element122,C_element132,N_element052,O_element114]
  conduct = 2
  density = 1
  expand = 3
  formula = G4_THYMINE
  name = G4_THYMINE
  specific = 4
FEATURE [App::DocumentObjectGroupPython] H_element123  label="H_element : 070"  # scripted group (container) (typed FeaturePython)
  n = 4
  ref = H_element
FEATURE [App::DocumentObjectGroupPython] C_element133  label="C_element : 078"  # scripted group (container) (typed FeaturePython)
  n = 4
  ref = C_element
FEATURE [App::DocumentObjectGroupPython] N_element053  label="N_element : 025"  # scripted group (container) (typed FeaturePython)
  n = 2
  ref = N_element
FEATURE [App::DocumentObjectGroupPython] O_element115  label="O_element : 068"  # scripted group (container) (typed FeaturePython)
  n = 2
  ref = O_element
FEATURE [App::DocumentObjectGroupPython] G4_URACIL  # scripted group (container) (typed FeaturePython)
  Dunit = g/cm3
  Dvalue = 1.32
  Group = -> [H_element123,C_element133,N_element053,O_element115]
  conduct = 2
  density = 1
  expand = 3
  formula = G4_URACIL
  name = G4_URACIL
  specific = 4
FEATURE [App::DocumentObjectGroupPython] H_element124  label="H_element : 071"  # scripted group (container) (typed FeaturePython)
  n = 4
  ref = H_element
FEATURE [App::DocumentObjectGroupPython] C_element134  label="C_element : 079"  # scripted group (container) (typed FeaturePython)
  n = 5
  ref = C_element
FEATURE [App::DocumentObjectGroupPython] N_element054  label="N_element : 026"  # scripted group (container) (typed FeaturePython)
  n = 5
  ref = N_element
FEATURE [App::DocumentObjectGroupPython] G4_DNA_ADENINE  # scripted group (container) (typed FeaturePython)
  Dunit = g/cm3
  Dvalue = 1
  Group = -> [H_element124,C_element134,N_element054]
  conduct = 2
  density = 1
  expand = 3
  formula = G4_DNA_ADENINE
  name = G4_DNA_ADENINE
  specific = 4
FEATURE [App::DocumentObjectGroupPython] H_element125  label="H_element : 072"  # scripted group (container) (typed FeaturePython)
  n = 4
  ref = H_element
FEATURE [App::DocumentObjectGroupPython] C_element135  label="C_element : 080"  # scripted group (container) (typed FeaturePython)
  n = 5
  ref = C_element
FEATURE [App::DocumentObjectGroupPython] N_element055  label="N_element : 027"  # scripted group (container) (typed FeaturePython)
  n = 5
  ref = N_element
FEATURE [App::DocumentObjectGroupPython] O_element116  label="O_element : 069"  # scripted group (container) (typed FeaturePython)
  n = 1
  ref = O_element
FEATURE [App::DocumentObjectGroupPython] G4_DNA_GUANINE  # scripted group (container) (typed FeaturePython)
  Dunit = g/cm3
  Dvalue = 1
  Group = -> [H_element125,C_element135,N_element055,O_element116]
  conduct = 2
  density = 1
  expand = 3
  formula = G4_DNA_GUANINE
  name = G4_DNA_GUANINE
  specific = 4
FEATURE [App::DocumentObjectGroupPython] H_element126  label="H_element : 073"  # scripted group (container) (typed FeaturePython)
  n = 4
  ref = H_element
FEATURE [App::DocumentObjectGroupPython] C_element136  label="C_element : 081"  # scripted group (container) (typed FeaturePython)
  n = 4
  ref = C_element
FEATURE [App::DocumentObjectGroupPython] N_element056  label="N_element : 028"  # scripted group (container) (typed FeaturePython)
  n = 3
  ref = N_element
FEATURE [App::DocumentObjectGroupPython] O_element117  label="O_element : 070"  # scripted group (container) (typed FeaturePython)
  n = 1
  ref = O_element
FEATURE [App::DocumentObjectGroupPython] G4_DNA_CYTOSINE  # scripted group (container) (typed FeaturePython)
  Dunit = g/cm3
  Dvalue = 1
  Group = -> [H_element126,C_element136,N_element056,O_element117]
  conduct = 2
  density = 1
  expand = 3
  formula = G4_DNA_CYTOSINE
  name = G4_DNA_CYTOSINE
  specific = 4
FEATURE [App::DocumentObjectGroupPython] H_element127  label="H_element : 074"  # scripted group (container) (typed FeaturePython)
  n = 5
  ref = H_element
FEATURE [App::DocumentObjectGroupPython] C_element137  label="C_element : 082"  # scripted group (container) (typed FeaturePython)
  n = 5
  ref = C_element
FEATURE [App::DocumentObjectGroupPython] N_element057  label="N_element : 029"  # scripted group (container) (typed FeaturePython)
  n = 2
  ref = N_element
FEATURE [App::DocumentObjectGroupPython] O_element118  label="O_element : 071"  # scripted group (container) (typed FeaturePython)
  n = 2
  ref = O_element
FEATURE [App::DocumentObjectGroupPython] G4_DNA_THYMINE  # scripted group (container) (typed FeaturePython)
  Dunit = g/cm3
  Dvalue = 1
  Group = -> [H_element127,C_element137,N_element057,O_element118]
  conduct = 2
  density = 1
  expand = 3
  formula = G4_DNA_THYMINE
  name = G4_DNA_THYMINE
  specific = 4
FEATURE [App::DocumentObjectGroupPython] H_element128  label="H_element : 075"  # scripted group (container) (typed FeaturePython)
  n = 3
  ref = H_element
FEATURE [App::DocumentObjectGroupPython] C_element138  label="C_element : 083"  # scripted group (container) (typed FeaturePython)
  n = 4
  ref = C_element
FEATURE [App::DocumentObjectGroupPython] N_element058  label="N_element : 030"  # scripted group (container) (typed FeaturePython)
  n = 2
  ref = N_element
FEATURE [App::DocumentObjectGroupPython] O_element119  label="O_element : 072"  # scripted group (container) (typed FeaturePython)
  n = 2
  ref = O_element
FEATURE [App::DocumentObjectGroupPython] G4_DNA_URACIL  # scripted group (container) (typed FeaturePython)
  Dunit = g/cm3
  Dvalue = 1
  Group = -> [H_element128,C_element138,N_element058,O_element119]
  conduct = 2
  density = 1
  expand = 3
  formula = G4_DNA_URACIL
  name = G4_DNA_URACIL
  specific = 4
FEATURE [App::DocumentObjectGroupPython] H_element129  label="H_element : 076"  # scripted group (container) (typed FeaturePython)
  n = 10
  ref = H_element
FEATURE [App::DocumentObjectGroupPython] C_element139  label="C_element : 084"  # scripted group (container) (typed FeaturePython)
  n = 10
  ref = C_element
FEATURE [App::DocumentObjectGroupPython] N_element059  label="N_element : 031"  # scripted group (container) (typed FeaturePython)
  n = 5
  ref = N_element
FEATURE [App::DocumentObjectGroupPython] O_element120  label="O_element : 073"  # scripted group (container) (typed FeaturePython)
  n = 4
  ref = O_element
FEATURE [App::DocumentObjectGroupPython] G4_DNA_ADENOSINE  # scripted group (container) (typed FeaturePython)
  Dunit = g/cm3
  Dvalue = 1
  Group = -> [H_element129,C_element139,N_element059,O_element120]
  conduct = 2
  density = 1
  expand = 3
  formula = G4_DNA_ADENOSINE
  name = G4_DNA_ADENOSINE
  specific = 4
FEATURE [App::DocumentObjectGroupPython] H_element130  label="H_element : 077"  # scripted group (container) (typed FeaturePython)
  n = 10
  ref = H_element
FEATURE [App::DocumentObjectGroupPython] C_element140  label="C_element : 085"  # scripted group (container) (typed FeaturePython)
  n = 10
  ref = C_element
FEATURE [App::DocumentObjectGroupPython] N_element060  label="N_element : 032"  # scripted group (container) (typed FeaturePython)
  n = 5
  ref = N_element
FEATURE [App::DocumentObjectGroupPython] O_element121  label="O_element : 074"  # scripted group (container) (typed FeaturePython)
  n = 5
  ref = O_element
FEATURE [App::DocumentObjectGroupPython] G4_DNA_GUANOSINE  # scripted group (container) (typed FeaturePython)
  Dunit = g/cm3
  Dvalue = 1
  Group = -> [H_element130,C_element140,N_element060,O_element121]
  conduct = 2
  density = 1
  expand = 3
  formula = G4_DNA_GUANOSINE
  name = G4_DNA_GUANOSINE
  specific = 4
FEATURE [App::DocumentObjectGroupPython] H_element131  label="H_element : 078"  # scripted group (container) (typed FeaturePython)
  n = 10
  ref = H_element
FEATURE [App::DocumentObjectGroupPython] C_element141  label="C_element : 086"  # scripted group (container) (typed FeaturePython)
  n = 9
  ref = C_element
FEATURE [App::DocumentObjectGroupPython] N_element061  label="N_element : 033"  # scripted group (container) (typed FeaturePython)
  n = 3
  ref = N_element
FEATURE [App::DocumentObjectGroupPython] O_element122  label="O_element : 075"  # scripted group (container) (typed FeaturePython)
  n = 5
  ref = O_element
FEATURE [App::DocumentObjectGroupPython] G4_DNA_CYTIDINE  # scripted group (container) (typed FeaturePython)
  Dunit = g/cm3
  Dvalue = 1
  Group = -> [H_element131,C_element141,N_element061,O_element122]
  conduct = 2
  density = 1
  expand = 3
  formula = G4_DNA_CYTIDINE
  name = G4_DNA_CYTIDINE
  specific = 4
FEATURE [App::DocumentObjectGroupPython] H_element132  label="H_element : 079"  # scripted group (container) (typed FeaturePython)
  n = 9
  ref = H_element
FEATURE [App::DocumentObjectGroupPython] C_element142  label="C_element : 087"  # scripted group (container) (typed FeaturePython)
  n = 9
  ref = C_element
FEATURE [App::DocumentObjectGroupPython] N_element062  label="N_element : 034"  # scripted group (container) (typed FeaturePython)
  n = 2
  ref = N_element
FEATURE [App::DocumentObjectGroupPython] O_element123  label="O_element : 076"  # scripted group (container) (typed FeaturePython)
  n = 6
  ref = O_element
FEATURE [App::DocumentObjectGroupPython] G4_DNA_URIDINE  # scripted group (container) (typed FeaturePython)
  Dunit = g/cm3
  Dvalue = 1
  Group = -> [H_element132,C_element142,N_element062,O_element123]
  conduct = 2
  density = 1
  expand = 3
  formula = G4_DNA_URIDINE
  name = G4_DNA_URIDINE
  specific = 4
FEATURE [App::DocumentObjectGroupPython] H_element133  label="H_element : 080"  # scripted group (container) (typed FeaturePython)
  n = 11
  ref = H_element
FEATURE [App::DocumentObjectGroupPython] C_element143  label="C_element : 088"  # scripted group (container) (typed FeaturePython)
  n = 10
  ref = C_element
FEATURE [App::DocumentObjectGroupPython] N_element063  label="N_element : 035"  # scripted group (container) (typed FeaturePython)
  n = 2
  ref = N_element
FEATURE [App::DocumentObjectGroupPython] O_element124  label="O_element : 077"  # scripted group (container) (typed FeaturePython)
  n = 6
  ref = O_element
FEATURE [App::DocumentObjectGroupPython] G4_DNA_METHYLURIDINE  # scripted group (container) (typed FeaturePython)
  Dunit = g/cm3
  Dvalue = 1
  Group = -> [H_element133,C_element143,N_element063,O_element124]
  conduct = 2
  density = 1
  expand = 3
  formula = G4_DNA_METHYLURIDINE
  name = G4_DNA_METHYLURIDINE
  specific = 4
FEATURE [App::DocumentObjectGroupPython] P_element014  label="P_element : 003"  # scripted group (container) (typed FeaturePython)
  n = 1
  ref = P_element
FEATURE [App::DocumentObjectGroupPython] O_element125  label="O_element : 078"  # scripted group (container) (typed FeaturePython)
  n = 3
  ref = O_element
FEATURE [App::DocumentObjectGroupPython] G4_DNA_MONOPHOSPHATE  # scripted group (container) (typed FeaturePython)
  Dunit = g/cm3
  Dvalue = 1
  Group = -> [P_element014,O_element125]
  conduct = 2
  density = 1
  expand = 3
  formula = G4_DNA_MONOPHOSPHATE
  name = G4_DNA_MONOPHOSPHATE
  specific = 4
FEATURE [App::DocumentObjectGroupPython] H_element134  label="H_element : 081"  # scripted group (container) (typed FeaturePython)
  n = 10
  ref = H_element
FEATURE [App::DocumentObjectGroupPython] C_element144  label="C_element : 089"  # scripted group (container) (typed FeaturePython)
  n = 10
  ref = C_element
FEATURE [App::DocumentObjectGroupPython] N_element064  label="N_element : 036"  # scripted group (container) (typed FeaturePython)
  n = 5
  ref = N_element
FEATURE [App::DocumentObjectGroupPython] O_element126  label="O_element : 079"  # scripted group (container) (typed FeaturePython)
  n = 7
  ref = O_element
FEATURE [App::DocumentObjectGroupPython] P_element015  label="P_element : 004"  # scripted group (container) (typed FeaturePython)
  n = 1
  ref = P_element
FEATURE [App::DocumentObjectGroupPython] G4_DNA_A  # scripted group (container) (typed FeaturePython)
  Dunit = g/cm3
  Dvalue = 1
  Group = -> [H_element134,C_element144,N_element064,O_element126,P_element015]
  conduct = 2
  density = 1
  expand = 3
  formula = G4_DNA_A
  name = G4_DNA_A
  specific = 4
FEATURE [App::DocumentObjectGroupPython] H_element135  label="H_element : 082"  # scripted group (container) (typed FeaturePython)
  n = 10
  ref = H_element
FEATURE [App::DocumentObjectGroupPython] C_element145  label="C_element : 090"  # scripted group (container) (typed FeaturePython)
  n = 10
  ref = C_element
FEATURE [App::DocumentObjectGroupPython] N_element065  label="N_element : 037"  # scripted group (container) (typed FeaturePython)
  n = 5
  ref = N_element
FEATURE [App::DocumentObjectGroupPython] O_element127  label="O_element : 8"  # scripted group (container) (typed FeaturePython)
  n = 8
  ref = O_element
FEATURE [App::DocumentObjectGroupPython] P_element016  label="P_element : 005"  # scripted group (container) (typed FeaturePython)
  n = 1
  ref = P_element
FEATURE [App::DocumentObjectGroupPython] G4_DNA_G  # scripted group (container) (typed FeaturePython)
  Dunit = g/cm3
  Dvalue = 1
  Group = -> [H_element135,C_element145,N_element065,O_element127,P_element016]
  conduct = 2
  density = 1
  expand = 3
  formula = G4_DNA_G
  name = G4_DNA_G
  specific = 4
FEATURE [App::DocumentObjectGroupPython] H_element136  label="H_element : 083"  # scripted group (container) (typed FeaturePython)
  n = 10
  ref = H_element
FEATURE [App::DocumentObjectGroupPython] C_element146  label="C_element : 091"  # scripted group (container) (typed FeaturePython)
  n = 9
  ref = C_element
FEATURE [App::DocumentObjectGroupPython] N_element066  label="N_element : 038"  # scripted group (container) (typed FeaturePython)
  n = 3
  ref = N_element
FEATURE [App::DocumentObjectGroupPython] O_element128  label="O_element : 080"  # scripted group (container) (typed FeaturePython)
  n = 8
  ref = O_element
FEATURE [App::DocumentObjectGroupPython] P_element017  label="P_element : 006"  # scripted group (container) (typed FeaturePython)
  n = 1
  ref = P_element
FEATURE [App::DocumentObjectGroupPython] G4_DNA_C  # scripted group (container) (typed FeaturePython)
  Dunit = g/cm3
  Dvalue = 1
  Group = -> [H_element136,C_element146,N_element066,O_element128,P_element017]
  conduct = 2
  density = 1
  expand = 3
  formula = G4_DNA_C
  name = G4_DNA_C
  specific = 4
FEATURE [App::DocumentObjectGroupPython] H_element137  label="H_element : 084"  # scripted group (container) (typed FeaturePython)
  n = 9
  ref = H_element
FEATURE [App::DocumentObjectGroupPython] C_element147  label="C_element : 092"  # scripted group (container) (typed FeaturePython)
  n = 9
  ref = C_element
FEATURE [App::DocumentObjectGroupPython] N_element067  label="N_element : 039"  # scripted group (container) (typed FeaturePython)
  n = 2
  ref = N_element
FEATURE [App::DocumentObjectGroupPython] O_element129  label="O_element : 9"  # scripted group (container) (typed FeaturePython)
  n = 9
  ref = O_element
FEATURE [App::DocumentObjectGroupPython] P_element018  label="P_element : 007"  # scripted group (container) (typed FeaturePython)
  n = 1
  ref = P_element
FEATURE [App::DocumentObjectGroupPython] G4_DNA_U  # scripted group (container) (typed FeaturePython)
  Dunit = g/cm3
  Dvalue = 1
  Group = -> [H_element137,C_element147,N_element067,O_element129,P_element018]
  conduct = 2
  density = 1
  expand = 3
  formula = G4_DNA_U
  name = G4_DNA_U
  specific = 4
FEATURE [App::DocumentObjectGroupPython] H_element138  label="H_element : 085"  # scripted group (container) (typed FeaturePython)
  n = 11
  ref = H_element
FEATURE [App::DocumentObjectGroupPython] C_element148  label="C_element : 093"  # scripted group (container) (typed FeaturePython)
  n = 10
  ref = C_element
FEATURE [App::DocumentObjectGroupPython] N_element068  label="N_element : 040"  # scripted group (container) (typed FeaturePython)
  n = 2
  ref = N_element
FEATURE [App::DocumentObjectGroupPython] O_element130  label="O_element : 081"  # scripted group (container) (typed FeaturePython)
  n = 9
  ref = O_element
FEATURE [App::DocumentObjectGroupPython] P_element019  label="P_element : 008"  # scripted group (container) (typed FeaturePython)
  n = 1
  ref = P_element
FEATURE [App::DocumentObjectGroupPython] G4_DNA_MU  # scripted group (container) (typed FeaturePython)
  Dunit = g/cm3
  Dvalue = 1
  Group = -> [H_element138,C_element148,N_element068,O_element130,P_element019]
  conduct = 2
  density = 1
  expand = 3
  formula = G4_DNA_MU
  name = G4_DNA_MU
  specific = 4
FEATURE [App::DocumentObjectGroupPython] BioChemical  # scripted group (container) (typed FeaturePython)
  Group = -> [G4_CYTOSINE,G4_THYMINE,G4_URACIL,G4_DNA_ADENINE,G4_DNA_GUANINE,G4_DNA_CYTOSINE,G4_DNA_THYMINE,G4_DNA_URACIL,G4_DNA_ADENOSINE,G4_DNA_GUANOSINE,G4_DNA_CYTIDINE,G4_DNA_URIDINE,G4_DNA_METHYLURIDINE,G4_DNA_MONOPHOSPHATE,G4_DNA_A,G4_DNA_G,G4_DNA_C,G4_DNA_U,G4_DNA_MU]
FEATURE [App::DocumentObjectGroupPython] G4Materials  # scripted group (container) (typed FeaturePython)
  Group = -> [NIST,Element,HEP,Space,BioChemical]
  version = 1
FEATURE [App::DocumentObjectGroupPython] Geant4  # scripted group (container) (typed FeaturePython)
  Group = -> [G4Isotopes,G4Elements,G4Materials]
FEATURE [App::DocumentObjectGroupPython] Materials  # scripted group (container) (typed FeaturePython)
  Group = -> [Geant4]
FEATURE [Part::FeaturePython] GDMLBox_WorldBox  # WARN: FeaturePython — macro-defined, semantics opaque (R4)
  lunit = 2
  material = 5
  x = 273
  y = 273
  z = 130
FEATURE [Part::FeaturePython] GDMLBox_Box  # WARN: FeaturePython — macro-defined, semantics opaque (R4)
  lunit = 2
  material = 0
  x = 10
  y = 10
  z = 10
FEATURE [Part::FeaturePython] GDMLTube  # WARN: FeaturePython — macro-defined, semantics opaque (R4)
  aunit = 1
  deltaphi = 90
  lunit = 2
  material = 0
  rmax = 7
  rmin = 5
  startphi = 0
  z = 7
FEATURE [App::Part] LV_Tube
  Group = -> [GDMLTube]
  Origin = -> Origin003
  SkinSurface = 0
FEATURE [App::Part] LV_Box
  Group = -> [GDMLBox_Box,LV_Tube]
  Origin = -> Origin002
  Placement = pos=(20,0,0) rot=(0,0,1;0rad)
FEATURE [Part::FeaturePython] Array  # Draft array (typed FeaturePython)
  AlwaysSyncPlacement = false
  Angle = 180
  ArrayType = 1
  Axis = (0,0,1)
  Base = -> LV_Box
  Center = (0,0,0)
  Count = 5
  ExpandArray = false
  Fuse = false
  IntervalAxis = (0,0,0)
  IntervalX = (100,0,0)
  IntervalY = (0,100,0)
  IntervalZ = (0,0,100)
  NumberCircles = 3
  NumberPolar = 5
  NumberX = 2
  NumberY = 2
  NumberZ = 1
  PlacementList = 5 placements: [(20,0,0),(14.1421,14.1421,0),(3.55271e-15,20,0),(-14.1421,14.1421,0),(-20,2.44929e-15,0)]
  RadialDistance = 50
  ScaleList = (5) [(1,1,1),(1,1,1),(1,1,1),(1,1,1),(1,1,1)]
  Symmetry = 1
  TangentialDistance = 25
FEATURE [App::Part] Part  label="experiment"
  Group = -> [LV_Box,Array]
  Origin = -> Origin001
FEATURE [App::Part] worldVOL
  Group = -> [GDMLBox_WorldBox,Part]
  Origin = -> Origin
